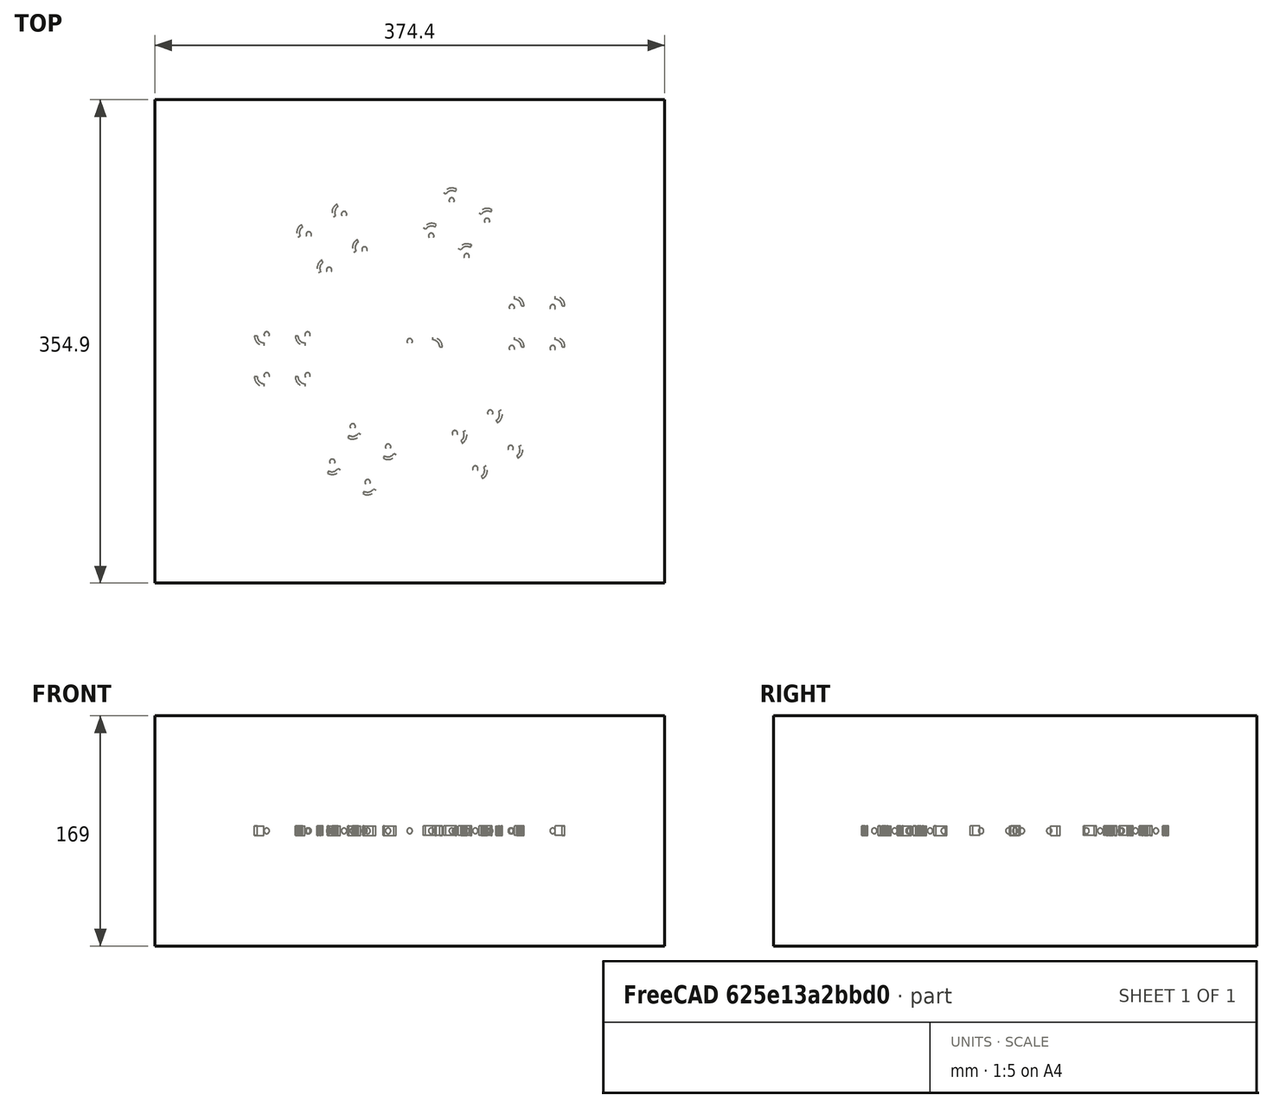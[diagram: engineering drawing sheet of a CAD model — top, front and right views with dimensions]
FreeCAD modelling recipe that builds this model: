
FCSTD DOCUMENT  (FreeCAD 1.0R39109 (Git))
Label: polarArrray-of-orthoArray-of-Assembly
License: All rights reserved
LicenseURL: http://en.wikipedia.org/wiki/All_rights_reserved
objects: App::DocumentObjectGroupPython×1251, App::Part×6, Part::FeaturePython×5
note: 5 computed .brp shape members not serialized (recipe doc carries the construction recipe); baked Part::Feature solids carry a one-line shape summary decoded from their .brp

FEATURE [App::DocumentObjectGroupPython] HALFPI  # scripted group (container) (typed FeaturePython)
  name = HALFPI
  value = pi/2.
FEATURE [App::DocumentObjectGroupPython] PI  # scripted group (container) (typed FeaturePython)
  name = PI
  value = 1.*pi
FEATURE [App::DocumentObjectGroupPython] TWOPI  # scripted group (container) (typed FeaturePython)
  name = TWOPI
  value = 2.*pi
FEATURE [App::DocumentObjectGroupPython] Constants  # scripted group (container) (typed FeaturePython)
  Group = -> [HALFPI,PI,TWOPI]
FEATURE [App::DocumentObjectGroupPython] Variables  # scripted group (container) (typed FeaturePython)
FEATURE [App::DocumentObjectGroupPython] Quantities  # scripted group (container) (typed FeaturePython)
FEATURE [App::DocumentObjectGroupPython] Isotopes  # scripted group (container) (typed FeaturePython)
FEATURE [App::DocumentObjectGroupPython] Elements  # scripted group (container) (typed FeaturePython)
FEATURE [App::DocumentObjectGroupPython] Matrix  # scripted group (container) (typed FeaturePython)
FEATURE [App::DocumentObjectGroupPython] Surfaces  # scripted group (container) (typed FeaturePython)
FEATURE [App::DocumentObjectGroupPython] Opticals  # scripted group (container) (typed FeaturePython)
  Group = -> [Matrix,Surfaces]
FEATURE [App::DocumentObjectGroupPython] G4Isotopes  # scripted group (container) (typed FeaturePython)
FEATURE [App::DocumentObjectGroupPython] H_element  # scripted group (container) (typed FeaturePython)
  Z = 1
  atom_value = 1.008
  formula = H
  name = H_element
FEATURE [App::DocumentObjectGroupPython] He_element  # scripted group (container) (typed FeaturePython)
  Z = 2
  atom_value = 4.0026
  formula = He
  name = He_element
FEATURE [App::DocumentObjectGroupPython] Li_element  # scripted group (container) (typed FeaturePython)
  Z = 3
  atom_value = 6.94
  formula = Li
  name = Li_element
FEATURE [App::DocumentObjectGroupPython] Be_element  # scripted group (container) (typed FeaturePython)
  Z = 4
  atom_value = 9.01218
  formula = Be
  name = Be_element
FEATURE [App::DocumentObjectGroupPython] B_element  # scripted group (container) (typed FeaturePython)
  Z = 5
  atom_value = 10.81
  formula = B
  name = B_element
FEATURE [App::DocumentObjectGroupPython] C_element  # scripted group (container) (typed FeaturePython)
  Z = 6
  atom_value = 12.011
  formula = C
  name = C_element
FEATURE [App::DocumentObjectGroupPython] N_element  # scripted group (container) (typed FeaturePython)
  Z = 7
  atom_value = 14.007
  formula = N
  name = N_element
FEATURE [App::DocumentObjectGroupPython] O_element  # scripted group (container) (typed FeaturePython)
  Z = 8
  atom_value = 15.999
  formula = O
  name = O_element
FEATURE [App::DocumentObjectGroupPython] F_element  # scripted group (container) (typed FeaturePython)
  Z = 9
  atom_value = 18.9984
  formula = F
  name = F_element
FEATURE [App::DocumentObjectGroupPython] Ne_element  # scripted group (container) (typed FeaturePython)
  Z = 10
  atom_value = 20.1797
  formula = Ne
  name = Ne_element
FEATURE [App::DocumentObjectGroupPython] Na_element  # scripted group (container) (typed FeaturePython)
  Z = 11
  atom_value = 22.9898
  formula = Na
  name = Na_element
FEATURE [App::DocumentObjectGroupPython] Mg_element  # scripted group (container) (typed FeaturePython)
  Z = 12
  atom_value = 24.305
  formula = Mg
  name = Mg_element
FEATURE [App::DocumentObjectGroupPython] Al_element  # scripted group (container) (typed FeaturePython)
  Z = 13
  atom_value = 26.9815
  formula = Al
  name = Al_element
FEATURE [App::DocumentObjectGroupPython] Si_element  # scripted group (container) (typed FeaturePython)
  Z = 14
  atom_value = 28.085
  formula = Si
  name = Si_element
FEATURE [App::DocumentObjectGroupPython] P_element  # scripted group (container) (typed FeaturePython)
  Z = 15
  atom_value = 30.9738
  formula = P
  name = P_element
FEATURE [App::DocumentObjectGroupPython] S_element  # scripted group (container) (typed FeaturePython)
  Z = 16
  atom_value = 32.06
  formula = S
  name = S_element
FEATURE [App::DocumentObjectGroupPython] Cl_element  # scripted group (container) (typed FeaturePython)
  Z = 17
  atom_value = 35.45
  formula = Cl
  name = Cl_element
FEATURE [App::DocumentObjectGroupPython] Ar_element  # scripted group (container) (typed FeaturePython)
  Z = 18
  atom_value = 39.95
  formula = Ar
  name = Ar_element
FEATURE [App::DocumentObjectGroupPython] K_element  # scripted group (container) (typed FeaturePython)
  Z = 19
  atom_value = 39.0983
  formula = K
  name = K_element
FEATURE [App::DocumentObjectGroupPython] Ca_element  # scripted group (container) (typed FeaturePython)
  Z = 20
  atom_value = 40.078
  formula = Ca
  name = Ca_element
FEATURE [App::DocumentObjectGroupPython] Sc_element  # scripted group (container) (typed FeaturePython)
  Z = 21
  atom_value = 44.9559
  formula = Sc
  name = Sc_element
FEATURE [App::DocumentObjectGroupPython] Ti_element  # scripted group (container) (typed FeaturePython)
  Z = 22
  atom_value = 47.867
  formula = Ti
  name = Ti_element
FEATURE [App::DocumentObjectGroupPython] V_element  # scripted group (container) (typed FeaturePython)
  Z = 23
  atom_value = 50.9415
  formula = V
  name = V_element
FEATURE [App::DocumentObjectGroupPython] Cr_element  # scripted group (container) (typed FeaturePython)
  Z = 24
  atom_value = 51.9961
  formula = Cr
  name = Cr_element
FEATURE [App::DocumentObjectGroupPython] Mn_element  # scripted group (container) (typed FeaturePython)
  Z = 25
  atom_value = 54.938
  formula = Mn
  name = Mn_element
FEATURE [App::DocumentObjectGroupPython] Fe_element  # scripted group (container) (typed FeaturePython)
  Z = 26
  atom_value = 55.845
  formula = Fe
  name = Fe_element
FEATURE [App::DocumentObjectGroupPython] Co_element  # scripted group (container) (typed FeaturePython)
  Z = 27
  atom_value = 58.9332
  formula = Co
  name = Co_element
FEATURE [App::DocumentObjectGroupPython] Ni_element  # scripted group (container) (typed FeaturePython)
  Z = 28
  atom_value = 58.6934
  formula = Ni
  name = Ni_element
FEATURE [App::DocumentObjectGroupPython] Cu_element  # scripted group (container) (typed FeaturePython)
  Z = 29
  atom_value = 63.546
  formula = Cu
  name = Cu_element
FEATURE [App::DocumentObjectGroupPython] Zn_element  # scripted group (container) (typed FeaturePython)
  Z = 30
  atom_value = 65.38
  formula = Zn
  name = Zn_element
FEATURE [App::DocumentObjectGroupPython] Ga_element  # scripted group (container) (typed FeaturePython)
  Z = 31
  atom_value = 69.723
  formula = Ga
  name = Ga_element
FEATURE [App::DocumentObjectGroupPython] Ge_element  # scripted group (container) (typed FeaturePython)
  Z = 32
  atom_value = 72.63
  formula = Ge
  name = Ge_element
FEATURE [App::DocumentObjectGroupPython] As_element  # scripted group (container) (typed FeaturePython)
  Z = 33
  atom_value = 74.9216
  formula = As
  name = As_element
FEATURE [App::DocumentObjectGroupPython] Se_element  # scripted group (container) (typed FeaturePython)
  Z = 34
  atom_value = 78.971
  formula = Se
  name = Se_element
FEATURE [App::DocumentObjectGroupPython] Br_element  # scripted group (container) (typed FeaturePython)
  Z = 35
  atom_value = 79.904
  formula = Br
  name = Br_element
FEATURE [App::DocumentObjectGroupPython] Kr_element  # scripted group (container) (typed FeaturePython)
  Z = 36
  atom_value = 83.798
  formula = Kr
  name = Kr_element
FEATURE [App::DocumentObjectGroupPython] Rb_element  # scripted group (container) (typed FeaturePython)
  Z = 37
  atom_value = 85.4678
  formula = Rb
  name = Rb_element
FEATURE [App::DocumentObjectGroupPython] Sr_element  # scripted group (container) (typed FeaturePython)
  Z = 38
  atom_value = 87.62
  formula = Sr
  name = Sr_element
FEATURE [App::DocumentObjectGroupPython] Y_element  # scripted group (container) (typed FeaturePython)
  Z = 39
  atom_value = 88.9058
  formula = Y
  name = Y_element
FEATURE [App::DocumentObjectGroupPython] Zr_element  # scripted group (container) (typed FeaturePython)
  Z = 40
  atom_value = 91.224
  formula = Zr
  name = Zr_element
FEATURE [App::DocumentObjectGroupPython] Nb_element  # scripted group (container) (typed FeaturePython)
  Z = 41
  atom_value = 92.9064
  formula = Nb
  name = Nb_element
FEATURE [App::DocumentObjectGroupPython] Mo_element  # scripted group (container) (typed FeaturePython)
  Z = 42
  atom_value = 95.95
  formula = Mo
  name = Mo_element
FEATURE [App::DocumentObjectGroupPython] Tc_element  # scripted group (container) (typed FeaturePython)
  Z = 43
  atom_value = 97
  formula = Tc
  name = Tc_element
FEATURE [App::DocumentObjectGroupPython] Ru_element  # scripted group (container) (typed FeaturePython)
  Z = 44
  atom_value = 101.07
  formula = Ru
  name = Ru_element
FEATURE [App::DocumentObjectGroupPython] Rh_element  # scripted group (container) (typed FeaturePython)
  Z = 45
  atom_value = 102.905
  formula = Rh
  name = Rh_element
FEATURE [App::DocumentObjectGroupPython] Pd_element  # scripted group (container) (typed FeaturePython)
  Z = 46
  atom_value = 106.42
  formula = Pd
  name = Pd_element
FEATURE [App::DocumentObjectGroupPython] Ag_element  # scripted group (container) (typed FeaturePython)
  Z = 47
  atom_value = 107.868
  formula = Ag
  name = Ag_element
FEATURE [App::DocumentObjectGroupPython] Cd_element  # scripted group (container) (typed FeaturePython)
  Z = 48
  atom_value = 112.414
  formula = Cd
  name = Cd_element
FEATURE [App::DocumentObjectGroupPython] In_element  # scripted group (container) (typed FeaturePython)
  Z = 49
  atom_value = 114.818
  formula = In
  name = In_element
FEATURE [App::DocumentObjectGroupPython] Sn_element  # scripted group (container) (typed FeaturePython)
  Z = 50
  atom_value = 118.71
  formula = Sn
  name = Sn_element
FEATURE [App::DocumentObjectGroupPython] Sb_element  # scripted group (container) (typed FeaturePython)
  Z = 51
  atom_value = 121.76
  formula = Sb
  name = Sb_element
FEATURE [App::DocumentObjectGroupPython] Te_element  # scripted group (container) (typed FeaturePython)
  Z = 52
  atom_value = 127.6
  formula = Te
  name = Te_element
FEATURE [App::DocumentObjectGroupPython] I_element  # scripted group (container) (typed FeaturePython)
  Z = 53
  atom_value = 126.904
  formula = I
  name = I_element
FEATURE [App::DocumentObjectGroupPython] Xe_element  # scripted group (container) (typed FeaturePython)
  Z = 54
  atom_value = 131.293
  formula = Xe
  name = Xe_element
FEATURE [App::DocumentObjectGroupPython] Cs_element  # scripted group (container) (typed FeaturePython)
  Z = 55
  atom_value = 132.905
  formula = Cs
  name = Cs_element
FEATURE [App::DocumentObjectGroupPython] Ba_element  # scripted group (container) (typed FeaturePython)
  Z = 56
  atom_value = 137.327
  formula = Ba
  name = Ba_element
FEATURE [App::DocumentObjectGroupPython] La_element  # scripted group (container) (typed FeaturePython)
  Z = 57
  atom_value = 138.905
  formula = La
  name = La_element
FEATURE [App::DocumentObjectGroupPython] Ce_element  # scripted group (container) (typed FeaturePython)
  Z = 58
  atom_value = 140.116
  formula = Ce
  name = Ce_element
FEATURE [App::DocumentObjectGroupPython] Pr_element  # scripted group (container) (typed FeaturePython)
  Z = 59
  atom_value = 140.908
  formula = Pr
  name = Pr_element
FEATURE [App::DocumentObjectGroupPython] Nd_element  # scripted group (container) (typed FeaturePython)
  Z = 60
  atom_value = 144.242
  formula = Nd
  name = Nd_element
FEATURE [App::DocumentObjectGroupPython] Pm_element  # scripted group (container) (typed FeaturePython)
  Z = 61
  atom_value = 145
  formula = Pm
  name = Pm_element
FEATURE [App::DocumentObjectGroupPython] Sm_element  # scripted group (container) (typed FeaturePython)
  Z = 62
  atom_value = 150.36
  formula = Sm
  name = Sm_element
FEATURE [App::DocumentObjectGroupPython] Eu_element  # scripted group (container) (typed FeaturePython)
  Z = 63
  atom_value = 151.964
  formula = Eu
  name = Eu_element
FEATURE [App::DocumentObjectGroupPython] Gd_element  # scripted group (container) (typed FeaturePython)
  Z = 64
  atom_value = 157.25
  formula = Gd
  name = Gd_element
FEATURE [App::DocumentObjectGroupPython] Tb_element  # scripted group (container) (typed FeaturePython)
  Z = 65
  atom_value = 158.925
  formula = Tb
  name = Tb_element
FEATURE [App::DocumentObjectGroupPython] Dy_element  # scripted group (container) (typed FeaturePython)
  Z = 66
  atom_value = 162.5
  formula = Dy
  name = Dy_element
FEATURE [App::DocumentObjectGroupPython] Ho_element  # scripted group (container) (typed FeaturePython)
  Z = 67
  atom_value = 164.93
  formula = Ho
  name = Ho_element
FEATURE [App::DocumentObjectGroupPython] Er_element  # scripted group (container) (typed FeaturePython)
  Z = 68
  atom_value = 167.259
  formula = Er
  name = Er_element
FEATURE [App::DocumentObjectGroupPython] Tm_element  # scripted group (container) (typed FeaturePython)
  Z = 69
  atom_value = 168.934
  formula = Tm
  name = Tm_element
FEATURE [App::DocumentObjectGroupPython] Yb_element  # scripted group (container) (typed FeaturePython)
  Z = 70
  atom_value = 173.045
  formula = Yb
  name = Yb_element
FEATURE [App::DocumentObjectGroupPython] Lu_element  # scripted group (container) (typed FeaturePython)
  Z = 71
  atom_value = 174.967
  formula = Lu
  name = Lu_element
FEATURE [App::DocumentObjectGroupPython] Hf_element  # scripted group (container) (typed FeaturePython)
  Z = 72
  atom_value = 178.49
  formula = Hf
  name = Hf_element
FEATURE [App::DocumentObjectGroupPython] Ta_element  # scripted group (container) (typed FeaturePython)
  Z = 73
  atom_value = 180.948
  formula = Ta
  name = Ta_element
FEATURE [App::DocumentObjectGroupPython] W_element  # scripted group (container) (typed FeaturePython)
  Z = 74
  atom_value = 183.84
  formula = W
  name = W_element
FEATURE [App::DocumentObjectGroupPython] Re_element  # scripted group (container) (typed FeaturePython)
  Z = 75
  atom_value = 186.207
  formula = Re
  name = Re_element
FEATURE [App::DocumentObjectGroupPython] Os_element  # scripted group (container) (typed FeaturePython)
  Z = 76
  atom_value = 190.23
  formula = Os
  name = Os_element
FEATURE [App::DocumentObjectGroupPython] Ir_element  # scripted group (container) (typed FeaturePython)
  Z = 77
  atom_value = 192.217
  formula = Ir
  name = Ir_element
FEATURE [App::DocumentObjectGroupPython] Pt_element  # scripted group (container) (typed FeaturePython)
  Z = 78
  atom_value = 195.084
  formula = Pt
  name = Pt_element
FEATURE [App::DocumentObjectGroupPython] Au_element  # scripted group (container) (typed FeaturePython)
  Z = 79
  atom_value = 196.967
  formula = Au
  name = Au_element
FEATURE [App::DocumentObjectGroupPython] Hg_element  # scripted group (container) (typed FeaturePython)
  Z = 80
  atom_value = 200.592
  formula = Hg
  name = Hg_element
FEATURE [App::DocumentObjectGroupPython] Tl_element  # scripted group (container) (typed FeaturePython)
  Z = 81
  atom_value = 204.38
  formula = Tl
  name = Tl_element
FEATURE [App::DocumentObjectGroupPython] Pb_element  # scripted group (container) (typed FeaturePython)
  Z = 82
  atom_value = 207.2
  formula = Pb
  name = Pb_element
FEATURE [App::DocumentObjectGroupPython] Bi_element  # scripted group (container) (typed FeaturePython)
  Z = 83
  atom_value = 208.98
  formula = Bi
  name = Bi_element
FEATURE [App::DocumentObjectGroupPython] Po_element  # scripted group (container) (typed FeaturePython)
  Z = 84
  atom_value = 209
  formula = Po
  name = Po_element
FEATURE [App::DocumentObjectGroupPython] At_element  # scripted group (container) (typed FeaturePython)
  Z = 85
  atom_value = 210
  formula = At
  name = At_element
FEATURE [App::DocumentObjectGroupPython] Rn_element  # scripted group (container) (typed FeaturePython)
  Z = 86
  atom_value = 222
  formula = Rn
  name = Rn_element
FEATURE [App::DocumentObjectGroupPython] Fr_element  # scripted group (container) (typed FeaturePython)
  Z = 87
  atom_value = 223
  formula = Fr
  name = Fr_element
FEATURE [App::DocumentObjectGroupPython] Ra_element  # scripted group (container) (typed FeaturePython)
  Z = 88
  atom_value = 226
  formula = Ra
  name = Ra_element
FEATURE [App::DocumentObjectGroupPython] Ac_element  # scripted group (container) (typed FeaturePython)
  Z = 89
  atom_value = 227
  formula = Ac
  name = Ac_element
FEATURE [App::DocumentObjectGroupPython] Th_element  # scripted group (container) (typed FeaturePython)
  Z = 90
  atom_value = 232.038
  formula = Th
  name = Th_element
FEATURE [App::DocumentObjectGroupPython] Pa_element  # scripted group (container) (typed FeaturePython)
  Z = 91
  atom_value = 231.036
  formula = Pa
  name = Pa_element
FEATURE [App::DocumentObjectGroupPython] U_element  # scripted group (container) (typed FeaturePython)
  Z = 92
  atom_value = 238.029
  formula = U
  name = U_element
FEATURE [App::DocumentObjectGroupPython] Np_element  # scripted group (container) (typed FeaturePython)
  Z = 93
  atom_value = 237
  formula = Np
  name = Np_element
FEATURE [App::DocumentObjectGroupPython] Pu_element  # scripted group (container) (typed FeaturePython)
  Z = 94
  atom_value = 244
  formula = Pu
  name = Pu_element
FEATURE [App::DocumentObjectGroupPython] Am_element  # scripted group (container) (typed FeaturePython)
  Z = 95
  atom_value = 243
  formula = Am
  name = Am_element
FEATURE [App::DocumentObjectGroupPython] Cm_element  # scripted group (container) (typed FeaturePython)
  Z = 96
  atom_value = 247
  formula = Cm
  name = Cm_element
FEATURE [App::DocumentObjectGroupPython] Bk_element  # scripted group (container) (typed FeaturePython)
  Z = 97
  atom_value = 247
  formula = Bk
  name = Bk_element
FEATURE [App::DocumentObjectGroupPython] Cf_element  # scripted group (container) (typed FeaturePython)
  Z = 98
  atom_value = 251
  formula = Cf
  name = Cf_element
FEATURE [App::DocumentObjectGroupPython] G4Elements  # scripted group (container) (typed FeaturePython)
  Group = -> [H_element,He_element,Li_element,Be_element,B_element,C_element,N_element,O_element,F_element,Ne_element,Na_element,Mg_element,Al_element,Si_element,P_element,S_element,Cl_element,Ar_element,K_element,Ca_element,Sc_element,Ti_element,V_element,Cr_element,Mn_element,Fe_element,Co_element,Ni_element,Cu_element,Zn_element,Ga_element,Ge_element,As_element,Se_element,Br_element,Kr_element,Rb_element,+61 more]
FEATURE [App::DocumentObjectGroupPython] H_element001  label="H_element : 0.101"  # scripted group (container) (typed FeaturePython)
  n = 0.101327
FEATURE [App::DocumentObjectGroupPython] C_element001  label="C_element : 0.775"  # scripted group (container) (typed FeaturePython)
  n = 0.7755
FEATURE [App::DocumentObjectGroupPython] N_element001  label="N_element : 0.035"  # scripted group (container) (typed FeaturePython)
  n = 0.035057
FEATURE [App::DocumentObjectGroupPython] O_element001  label="O_element : 0.052"  # scripted group (container) (typed FeaturePython)
  n = 0.0523159
FEATURE [App::DocumentObjectGroupPython] F_element001  label="F_element : 0.017"  # scripted group (container) (typed FeaturePython)
  n = 0.017422
FEATURE [App::DocumentObjectGroupPython] Ca_element001  label="Ca_element : 0.018"  # scripted group (container) (typed FeaturePython)
  n = 0.018378
FEATURE [App::DocumentObjectGroupPython] G4_A_150_TISSUE  label="G4_A-150_TISSUE"  # scripted group (container) (typed FeaturePython)
  Dunit = g/cm3
  Dvalue = 1.127
  Group = -> [H_element001,C_element001,N_element001,O_element001,F_element001,Ca_element001]
  conduct = 2
  density = 1
  expand = 3
  formula = G4_A-150_TISSUE
  name = G4_A-150_TISSUE
  specific = 4
FEATURE [App::DocumentObjectGroupPython] C_element002  label="C_element : 3"  # scripted group (container) (typed FeaturePython)
  n = 3
  ref = C_element
FEATURE [App::DocumentObjectGroupPython] H_element002  label="H_element : 6"  # scripted group (container) (typed FeaturePython)
  n = 6
  ref = H_element
FEATURE [App::DocumentObjectGroupPython] O_element002  label="O_element : 1"  # scripted group (container) (typed FeaturePython)
  n = 1
  ref = O_element
FEATURE [App::DocumentObjectGroupPython] G4_ACETONE  # scripted group (container) (typed FeaturePython)
  Dunit = g/cm3
  Dvalue = 0.7899
  Group = -> [C_element002,H_element002,O_element002]
  conduct = 2
  density = 1
  expand = 3
  formula = G4_ACETONE
  name = G4_ACETONE
  specific = 4
FEATURE [App::DocumentObjectGroupPython] C_element003  label="C_element : 2"  # scripted group (container) (typed FeaturePython)
  n = 2
  ref = C_element
FEATURE [App::DocumentObjectGroupPython] H_element003  label="H_element : 2"  # scripted group (container) (typed FeaturePython)
  n = 2
  ref = H_element
FEATURE [App::DocumentObjectGroupPython] G4_ACETYLENE  # scripted group (container) (typed FeaturePython)
  Dunit = g/cm3
  Dvalue = 0.0010967
  Group = -> [C_element003,H_element003]
  conduct = 2
  density = 1
  expand = 3
  formula = G4_ACETYLENE
  name = G4_ACETYLENE
  specific = 4
FEATURE [App::DocumentObjectGroupPython] C_element004  label="C_element : 5"  # scripted group (container) (typed FeaturePython)
  n = 5
  ref = C_element
FEATURE [App::DocumentObjectGroupPython] H_element004  label="H_element : 5"  # scripted group (container) (typed FeaturePython)
  n = 5
  ref = H_element
FEATURE [App::DocumentObjectGroupPython] N_element002  label="N_element : 5"  # scripted group (container) (typed FeaturePython)
  n = 5
  ref = N_element
FEATURE [App::DocumentObjectGroupPython] G4_ADENINE  # scripted group (container) (typed FeaturePython)
  Dunit = g/cm3
  Dvalue = 1.6
  Group = -> [C_element004,H_element004,N_element002]
  conduct = 2
  density = 1
  expand = 3
  formula = G4_ADENINE
  name = G4_ADENINE
  specific = 4
FEATURE [App::DocumentObjectGroupPython] H_element005  label="H_element : 0.114"  # scripted group (container) (typed FeaturePython)
  n = 0.114
FEATURE [App::DocumentObjectGroupPython] C_element005  label="C_element : 0.598"  # scripted group (container) (typed FeaturePython)
  n = 0.598
FEATURE [App::DocumentObjectGroupPython] N_element003  label="N_element : 0.007"  # scripted group (container) (typed FeaturePython)
  n = 0.007
FEATURE [App::DocumentObjectGroupPython] O_element003  label="O_element : 0.278"  # scripted group (container) (typed FeaturePython)
  n = 0.278
FEATURE [App::DocumentObjectGroupPython] Na_element001  label="Na_element : 0.001"  # scripted group (container) (typed FeaturePython)
  n = 0.001
FEATURE [App::DocumentObjectGroupPython] S_element001  label="S_element : 0.001"  # scripted group (container) (typed FeaturePython)
  n = 0.001
FEATURE [App::DocumentObjectGroupPython] Cl_element001  label="Cl_element : 0.001"  # scripted group (container) (typed FeaturePython)
  n = 0.001
FEATURE [App::DocumentObjectGroupPython] G4_ADIPOSE_TISSUE_ICRP  # scripted group (container) (typed FeaturePython)
  Dunit = g/cm3
  Dvalue = 0.95
  Group = -> [H_element005,C_element005,N_element003,O_element003,Na_element001,S_element001,Cl_element001]
  conduct = 2
  density = 1
  expand = 3
  formula = G4_ADIPOSE_TISSUE_ICRP
  name = G4_ADIPOSE_TISSUE_ICRP
  specific = 4
FEATURE [App::DocumentObjectGroupPython] C_element006  label="C_element : 0.000"  # scripted group (container) (typed FeaturePython)
  n = 0.000124
FEATURE [App::DocumentObjectGroupPython] N_element004  label="N_element : 0.755"  # scripted group (container) (typed FeaturePython)
  n = 0.755268
FEATURE [App::DocumentObjectGroupPython] O_element004  label="O_element : 0.232"  # scripted group (container) (typed FeaturePython)
  n = 0.231781
FEATURE [App::DocumentObjectGroupPython] Ar_element001  label="Ar_element : 0.013"  # scripted group (container) (typed FeaturePython)
  n = 0.012827
FEATURE [App::DocumentObjectGroupPython] G4_AIR  # scripted group (container) (typed FeaturePython)
  Dunit = g/cm3
  Dvalue = 0.00120479
  Group = -> [C_element006,N_element004,O_element004,Ar_element001]
  conduct = 2
  density = 1
  expand = 3
  formula = G4_AIR
  name = G4_AIR
  specific = 4
FEATURE [App::DocumentObjectGroupPython] C_element007  label="C_element : 006"  # scripted group (container) (typed FeaturePython)
  n = 3
  ref = C_element
FEATURE [App::DocumentObjectGroupPython] H_element006  label="H_element : 7"  # scripted group (container) (typed FeaturePython)
  n = 7
  ref = H_element
FEATURE [App::DocumentObjectGroupPython] N_element005  label="N_element : 1"  # scripted group (container) (typed FeaturePython)
  n = 1
  ref = N_element
FEATURE [App::DocumentObjectGroupPython] O_element005  label="O_element : 2"  # scripted group (container) (typed FeaturePython)
  n = 2
  ref = O_element
FEATURE [App::DocumentObjectGroupPython] G4_ALANINE  # scripted group (container) (typed FeaturePython)
  Dunit = g/cm3
  Dvalue = 1.42
  Group = -> [C_element007,H_element006,N_element005,O_element005]
  conduct = 2
  density = 1
  expand = 3
  formula = G4_ALANINE
  name = G4_ALANINE
  specific = 4
FEATURE [App::DocumentObjectGroupPython] Al_element001  label="Al_element : 2"  # scripted group (container) (typed FeaturePython)
  n = 2
  ref = Al_element
FEATURE [App::DocumentObjectGroupPython] O_element006  label="O_element : 3"  # scripted group (container) (typed FeaturePython)
  n = 3
  ref = O_element
FEATURE [App::DocumentObjectGroupPython] G4_ALUMINUM_OXIDE  # scripted group (container) (typed FeaturePython)
  Dunit = g/cm3
  Dvalue = 3.97
  Group = -> [Al_element001,O_element006]
  conduct = 2
  density = 1
  expand = 3
  formula = G4_ALUMINUM_OXIDE
  name = G4_ALUMINUM_OXIDE
  specific = 4
FEATURE [App::DocumentObjectGroupPython] H_element007  label="H_element : 0.106"  # scripted group (container) (typed FeaturePython)
  n = 0.10593
FEATURE [App::DocumentObjectGroupPython] C_element008  label="C_element : 0.789"  # scripted group (container) (typed FeaturePython)
  n = 0.788974
FEATURE [App::DocumentObjectGroupPython] O_element007  label="O_element : 0.105"  # scripted group (container) (typed FeaturePython)
  n = 0.105096
FEATURE [App::DocumentObjectGroupPython] G4_AMBER  # scripted group (container) (typed FeaturePython)
  Dunit = g/cm3
  Dvalue = 1.1
  Group = -> [H_element007,C_element008,O_element007]
  conduct = 2
  density = 1
  expand = 3
  formula = G4_AMBER
  name = G4_AMBER
  specific = 4
FEATURE [App::DocumentObjectGroupPython] N_element006  label="N_element : 006"  # scripted group (container) (typed FeaturePython)
  n = 1
  ref = N_element
FEATURE [App::DocumentObjectGroupPython] H_element008  label="H_element : 3"  # scripted group (container) (typed FeaturePython)
  n = 3
  ref = H_element
FEATURE [App::DocumentObjectGroupPython] G4_AMMONIA  # scripted group (container) (typed FeaturePython)
  Dunit = g/cm3
  Dvalue = 0.000826019
  Group = -> [N_element006,H_element008]
  conduct = 2
  density = 1
  expand = 3
  formula = G4_AMMONIA
  name = G4_AMMONIA
  specific = 4
FEATURE [App::DocumentObjectGroupPython] C_element009  label="C_element : 6"  # scripted group (container) (typed FeaturePython)
  n = 6
  ref = C_element
FEATURE [App::DocumentObjectGroupPython] H_element009  label="H_element : 008"  # scripted group (container) (typed FeaturePython)
  n = 7
  ref = H_element
FEATURE [App::DocumentObjectGroupPython] N_element007  label="N_element : 007"  # scripted group (container) (typed FeaturePython)
  n = 1
  ref = N_element
FEATURE [App::DocumentObjectGroupPython] G4_ANILINE  # scripted group (container) (typed FeaturePython)
  Dunit = g/cm3
  Dvalue = 1.0235
  Group = -> [C_element009,H_element009,N_element007]
  conduct = 2
  density = 1
  expand = 3
  formula = G4_ANILINE
  name = G4_ANILINE
  specific = 4
FEATURE [App::DocumentObjectGroupPython] C_element010  label="C_element : 14"  # scripted group (container) (typed FeaturePython)
  n = 14
  ref = C_element
FEATURE [App::DocumentObjectGroupPython] H_element010  label="H_element : 10"  # scripted group (container) (typed FeaturePython)
  n = 10
  ref = H_element
FEATURE [App::DocumentObjectGroupPython] G4_ANTHRACENE  # scripted group (container) (typed FeaturePython)
  Dunit = g/cm3
  Dvalue = 1.283
  Group = -> [C_element010,H_element010]
  conduct = 2
  density = 1
  expand = 3
  formula = G4_ANTHRACENE
  name = G4_ANTHRACENE
  specific = 4
FEATURE [App::DocumentObjectGroupPython] H_element011  label="H_element : 0.065"  # scripted group (container) (typed FeaturePython)
  n = 0.0654709
FEATURE [App::DocumentObjectGroupPython] C_element011  label="C_element : 0.537"  # scripted group (container) (typed FeaturePython)
  n = 0.536944
FEATURE [App::DocumentObjectGroupPython] N_element008  label="N_element : 0.021"  # scripted group (container) (typed FeaturePython)
  n = 0.0215
FEATURE [App::DocumentObjectGroupPython] O_element008  label="O_element : 0.032"  # scripted group (container) (typed FeaturePython)
  n = 0.032085
FEATURE [App::DocumentObjectGroupPython] F_element002  label="F_element : 0.167"  # scripted group (container) (typed FeaturePython)
  n = 0.167411
FEATURE [App::DocumentObjectGroupPython] Ca_element002  label="Ca_element : 0.177"  # scripted group (container) (typed FeaturePython)
  n = 0.176589
FEATURE [App::DocumentObjectGroupPython] G4_B_100_BONE  label="G4_B-100_BONE"  # scripted group (container) (typed FeaturePython)
  Dunit = g/cm3
  Dvalue = 1.45
  Group = -> [H_element011,C_element011,N_element008,O_element008,F_element002,Ca_element002]
  conduct = 2
  density = 1
  expand = 3
  formula = G4_B-100_BONE
  name = G4_B-100_BONE
  specific = 4
FEATURE [App::DocumentObjectGroupPython] H_element012  label="H_element : 0.057"  # scripted group (container) (typed FeaturePython)
  n = 0.057441
FEATURE [App::DocumentObjectGroupPython] C_element012  label="C_element : 0.790"  # scripted group (container) (typed FeaturePython)
  n = 0.774591
FEATURE [App::DocumentObjectGroupPython] O_element009  label="O_element : 0.168"  # scripted group (container) (typed FeaturePython)
  n = 0.167968
FEATURE [App::DocumentObjectGroupPython] G4_BAKELITE  # scripted group (container) (typed FeaturePython)
  Dunit = g/cm3
  Dvalue = 1.25
  Group = -> [H_element012,C_element012,O_element009]
  conduct = 2
  density = 1
  expand = 3
  formula = G4_BAKELITE
  name = G4_BAKELITE
  specific = 4
FEATURE [App::DocumentObjectGroupPython] Ba_element001  label="Ba_element : 1"  # scripted group (container) (typed FeaturePython)
  n = 1
  ref = Ba_element
FEATURE [App::DocumentObjectGroupPython] F_element003  label="F_element : 2"  # scripted group (container) (typed FeaturePython)
  n = 2
  ref = F_element
FEATURE [App::DocumentObjectGroupPython] G4_BARIUM_FLUORIDE  # scripted group (container) (typed FeaturePython)
  Dunit = g/cm3
  Dvalue = 4.89
  Group = -> [Ba_element001,F_element003]
  conduct = 2
  density = 1
  expand = 3
  formula = G4_BARIUM_FLUORIDE
  name = G4_BARIUM_FLUORIDE
  specific = 4
FEATURE [App::DocumentObjectGroupPython] Ba_element002  label="Ba_element : 002"  # scripted group (container) (typed FeaturePython)
  n = 1
  ref = Ba_element
FEATURE [App::DocumentObjectGroupPython] S_element002  label="S_element : 1"  # scripted group (container) (typed FeaturePython)
  n = 1
  ref = S_element
FEATURE [App::DocumentObjectGroupPython] O_element010  label="O_element : 4"  # scripted group (container) (typed FeaturePython)
  n = 4
  ref = O_element
FEATURE [App::DocumentObjectGroupPython] G4_BARIUM_SULFATE  # scripted group (container) (typed FeaturePython)
  Dunit = g/cm3
  Dvalue = 4.5
  Group = -> [Ba_element002,S_element002,O_element010]
  conduct = 2
  density = 1
  expand = 3
  formula = G4_BARIUM_SULFATE
  name = G4_BARIUM_SULFATE
  specific = 4
FEATURE [App::DocumentObjectGroupPython] C_element013  label="C_element : 007"  # scripted group (container) (typed FeaturePython)
  n = 6
  ref = C_element
FEATURE [App::DocumentObjectGroupPython] H_element013  label="H_element : 009"  # scripted group (container) (typed FeaturePython)
  n = 6
  ref = H_element
FEATURE [App::DocumentObjectGroupPython] G4_BENZENE  # scripted group (container) (typed FeaturePython)
  Dunit = g/cm3
  Dvalue = 0.87865
  Group = -> [C_element013,H_element013]
  conduct = 2
  density = 1
  expand = 3
  formula = G4_BENZENE
  name = G4_BENZENE
  specific = 4
FEATURE [App::DocumentObjectGroupPython] Be_element001  label="Be_element : 1"  # scripted group (container) (typed FeaturePython)
  n = 1
  ref = Be_element
FEATURE [App::DocumentObjectGroupPython] O_element011  label="O_element : 005"  # scripted group (container) (typed FeaturePython)
  n = 1
  ref = O_element
FEATURE [App::DocumentObjectGroupPython] G4_BERYLLIUM_OXIDE  # scripted group (container) (typed FeaturePython)
  Dunit = g/cm3
  Dvalue = 3.01
  Group = -> [Be_element001,O_element011]
  conduct = 2
  density = 1
  expand = 3
  formula = G4_BERYLLIUM_OXIDE
  name = G4_BERYLLIUM_OXIDE
  specific = 4
FEATURE [App::DocumentObjectGroupPython] Bi_element001  label="Bi_element : 4"  # scripted group (container) (typed FeaturePython)
  n = 4
  ref = Bi_element
FEATURE [App::DocumentObjectGroupPython] Ge_element001  label="Ge_element : 3"  # scripted group (container) (typed FeaturePython)
  n = 3
  ref = Ge_element
FEATURE [App::DocumentObjectGroupPython] O_element012  label="O_element : 12"  # scripted group (container) (typed FeaturePython)
  n = 12
  ref = O_element
FEATURE [App::DocumentObjectGroupPython] G4_BGO  # scripted group (container) (typed FeaturePython)
  Dunit = g/cm3
  Dvalue = 7.13
  Group = -> [Bi_element001,Ge_element001,O_element012]
  conduct = 2
  density = 1
  expand = 3
  formula = G4_BGO
  name = G4_BGO
  specific = 4
FEATURE [App::DocumentObjectGroupPython] H_element014  label="H_element : 0.102"  # scripted group (container) (typed FeaturePython)
  n = 0.102
FEATURE [App::DocumentObjectGroupPython] C_element014  label="C_element : 0.110"  # scripted group (container) (typed FeaturePython)
  n = 0.11
FEATURE [App::DocumentObjectGroupPython] N_element009  label="N_element : 0.033"  # scripted group (container) (typed FeaturePython)
  n = 0.033
FEATURE [App::DocumentObjectGroupPython] O_element013  label="O_element : 0.745"  # scripted group (container) (typed FeaturePython)
  n = 0.745
FEATURE [App::DocumentObjectGroupPython] Na_element002  label="Na_element : 0.002"  # scripted group (container) (typed FeaturePython)
  n = 0.001
FEATURE [App::DocumentObjectGroupPython] P_element001  label="P_element : 0.001"  # scripted group (container) (typed FeaturePython)
  n = 0.001
FEATURE [App::DocumentObjectGroupPython] S_element003  label="S_element : 0.002"  # scripted group (container) (typed FeaturePython)
  n = 0.002
FEATURE [App::DocumentObjectGroupPython] Cl_element002  label="Cl_element : 0.003"  # scripted group (container) (typed FeaturePython)
  n = 0.003
FEATURE [App::DocumentObjectGroupPython] K_element001  label="K_element : 0.002"  # scripted group (container) (typed FeaturePython)
  n = 0.002
FEATURE [App::DocumentObjectGroupPython] Fe_element001  label="Fe_element : 0.001"  # scripted group (container) (typed FeaturePython)
  n = 0.001
FEATURE [App::DocumentObjectGroupPython] G4_BLOOD_ICRP  # scripted group (container) (typed FeaturePython)
  Dunit = g/cm3
  Dvalue = 1.06
  Group = -> [H_element014,C_element014,N_element009,O_element013,Na_element002,P_element001,S_element003,Cl_element002,K_element001,Fe_element001]
  conduct = 2
  density = 1
  expand = 3
  formula = G4_BLOOD_ICRP
  name = G4_BLOOD_ICRP
  specific = 4
FEATURE [App::DocumentObjectGroupPython] H_element015  label="H_element : 0.064"  # scripted group (container) (typed FeaturePython)
  n = 0.064
FEATURE [App::DocumentObjectGroupPython] C_element015  label="C_element : 0.278"  # scripted group (container) (typed FeaturePython)
  n = 0.278
FEATURE [App::DocumentObjectGroupPython] N_element010  label="N_element : 0.027"  # scripted group (container) (typed FeaturePython)
  n = 0.027
FEATURE [App::DocumentObjectGroupPython] O_element014  label="O_element : 0.410"  # scripted group (container) (typed FeaturePython)
  n = 0.41
FEATURE [App::DocumentObjectGroupPython] Mg_element001  label="Mg_element : 0.002"  # scripted group (container) (typed FeaturePython)
  n = 0.002
FEATURE [App::DocumentObjectGroupPython] P_element002  label="P_element : 0.070"  # scripted group (container) (typed FeaturePython)
  n = 0.07
FEATURE [App::DocumentObjectGroupPython] S_element004  label="S_element : 0.003"  # scripted group (container) (typed FeaturePython)
  n = 0.002
FEATURE [App::DocumentObjectGroupPython] Ca_element003  label="Ca_element : 0.147"  # scripted group (container) (typed FeaturePython)
  n = 0.147
FEATURE [App::DocumentObjectGroupPython] G4_BONE_COMPACT_ICRU  # scripted group (container) (typed FeaturePython)
  Dunit = g/cm3
  Dvalue = 1.85
  Group = -> [H_element015,C_element015,N_element010,O_element014,Mg_element001,P_element002,S_element004,Ca_element003]
  conduct = 2
  density = 1
  expand = 3
  formula = G4_BONE_COMPACT_ICRU
  name = G4_BONE_COMPACT_ICRU
  specific = 4
FEATURE [App::DocumentObjectGroupPython] H_element016  label="H_element : 0.034"  # scripted group (container) (typed FeaturePython)
  n = 0.034
FEATURE [App::DocumentObjectGroupPython] C_element016  label="C_element : 0.155"  # scripted group (container) (typed FeaturePython)
  n = 0.155
FEATURE [App::DocumentObjectGroupPython] N_element011  label="N_element : 0.042"  # scripted group (container) (typed FeaturePython)
  n = 0.042
FEATURE [App::DocumentObjectGroupPython] O_element015  label="O_element : 0.435"  # scripted group (container) (typed FeaturePython)
  n = 0.435
FEATURE [App::DocumentObjectGroupPython] Na_element003  label="Na_element : 0.003"  # scripted group (container) (typed FeaturePython)
  n = 0.001
FEATURE [App::DocumentObjectGroupPython] Mg_element002  label="Mg_element : 0.003"  # scripted group (container) (typed FeaturePython)
  n = 0.002
FEATURE [App::DocumentObjectGroupPython] P_element003  label="P_element : 0.103"  # scripted group (container) (typed FeaturePython)
  n = 0.103
FEATURE [App::DocumentObjectGroupPython] S_element005  label="S_element : 0.004"  # scripted group (container) (typed FeaturePython)
  n = 0.003
FEATURE [App::DocumentObjectGroupPython] Ca_element004  label="Ca_element : 0.225"  # scripted group (container) (typed FeaturePython)
  n = 0.225
FEATURE [App::DocumentObjectGroupPython] G4_BONE_CORTICAL_ICRP  # scripted group (container) (typed FeaturePython)
  Dunit = g/cm3
  Dvalue = 1.92
  Group = -> [H_element016,C_element016,N_element011,O_element015,Na_element003,Mg_element002,P_element003,S_element005,Ca_element004]
  conduct = 2
  density = 1
  expand = 3
  formula = G4_BONE_CORTICAL_ICRP
  name = G4_BONE_CORTICAL_ICRP
  specific = 4
FEATURE [App::DocumentObjectGroupPython] B_element001  label="B_element : 4"  # scripted group (container) (typed FeaturePython)
  n = 4
  ref = B_element
FEATURE [App::DocumentObjectGroupPython] C_element017  label="C_element : 1"  # scripted group (container) (typed FeaturePython)
  n = 1
  ref = C_element
FEATURE [App::DocumentObjectGroupPython] G4_BORON_CARBIDE  # scripted group (container) (typed FeaturePython)
  Dunit = g/cm3
  Dvalue = 2.52
  Group = -> [B_element001,C_element017]
  conduct = 2
  density = 1
  expand = 3
  formula = G4_BORON_CARBIDE
  name = G4_BORON_CARBIDE
  specific = 4
FEATURE [App::DocumentObjectGroupPython] B_element002  label="B_element : 2"  # scripted group (container) (typed FeaturePython)
  n = 2
  ref = B_element
FEATURE [App::DocumentObjectGroupPython] O_element016  label="O_element : 006"  # scripted group (container) (typed FeaturePython)
  n = 3
  ref = O_element
FEATURE [App::DocumentObjectGroupPython] G4_BORON_OXIDE  # scripted group (container) (typed FeaturePython)
  Dunit = g/cm3
  Dvalue = 1.812
  Group = -> [B_element002,O_element016]
  conduct = 2
  density = 1
  expand = 3
  formula = G4_BORON_OXIDE
  name = G4_BORON_OXIDE
  specific = 4
FEATURE [App::DocumentObjectGroupPython] H_element017  label="H_element : 0.107"  # scripted group (container) (typed FeaturePython)
  n = 0.107
FEATURE [App::DocumentObjectGroupPython] C_element018  label="C_element : 0.145"  # scripted group (container) (typed FeaturePython)
  n = 0.145
FEATURE [App::DocumentObjectGroupPython] N_element012  label="N_element : 0.022"  # scripted group (container) (typed FeaturePython)
  n = 0.022
FEATURE [App::DocumentObjectGroupPython] O_element017  label="O_element : 0.712"  # scripted group (container) (typed FeaturePython)
  n = 0.712
FEATURE [App::DocumentObjectGroupPython] Na_element004  label="Na_element : 0.004"  # scripted group (container) (typed FeaturePython)
  n = 0.002
FEATURE [App::DocumentObjectGroupPython] P_element004  label="P_element : 0.004"  # scripted group (container) (typed FeaturePython)
  n = 0.004
FEATURE [App::DocumentObjectGroupPython] S_element006  label="S_element : 0.005"  # scripted group (container) (typed FeaturePython)
  n = 0.002
FEATURE [App::DocumentObjectGroupPython] Cl_element003  label="Cl_element : 0.004"  # scripted group (container) (typed FeaturePython)
  n = 0.003
FEATURE [App::DocumentObjectGroupPython] K_element002  label="K_element : 0.003"  # scripted group (container) (typed FeaturePython)
  n = 0.003
FEATURE [App::DocumentObjectGroupPython] G4_BRAIN_ICRP  # scripted group (container) (typed FeaturePython)
  Dunit = g/cm3
  Dvalue = 1.04
  Group = -> [H_element017,C_element018,N_element012,O_element017,Na_element004,P_element004,S_element006,Cl_element003,K_element002]
  conduct = 2
  density = 1
  expand = 3
  formula = G4_BRAIN_ICRP
  name = G4_BRAIN_ICRP
  specific = 4
FEATURE [App::DocumentObjectGroupPython] C_element019  label="C_element : 4"  # scripted group (container) (typed FeaturePython)
  n = 4
  ref = C_element
FEATURE [App::DocumentObjectGroupPython] H_element018  label="H_element : 010"  # scripted group (container) (typed FeaturePython)
  n = 10
  ref = H_element
FEATURE [App::DocumentObjectGroupPython] G4_BUTANE  # scripted group (container) (typed FeaturePython)
  Dunit = g/cm3
  Dvalue = 0.00249343
  Group = -> [C_element019,H_element018]
  conduct = 2
  density = 1
  expand = 3
  formula = G4_BUTANE
  name = G4_BUTANE
  specific = 4
FEATURE [App::DocumentObjectGroupPython] C_element020  label="C_element : 008"  # scripted group (container) (typed FeaturePython)
  n = 4
  ref = C_element
FEATURE [App::DocumentObjectGroupPython] H_element019  label="H_element : 011"  # scripted group (container) (typed FeaturePython)
  n = 10
  ref = H_element
FEATURE [App::DocumentObjectGroupPython] O_element018  label="O_element : 007"  # scripted group (container) (typed FeaturePython)
  n = 1
  ref = O_element
FEATURE [App::DocumentObjectGroupPython] G4_N_BUTYL_ALCOHOL  label="G4_N-BUTYL_ALCOHOL"  # scripted group (container) (typed FeaturePython)
  Dunit = g/cm3
  Dvalue = 0.8098
  Group = -> [C_element020,H_element019,O_element018]
  conduct = 2
  density = 1
  expand = 3
  formula = G4_N-BUTYL_ALCOHOL
  name = G4_N-BUTYL_ALCOHOL
  specific = 4
FEATURE [App::DocumentObjectGroupPython] H_element020  label="H_element : 0.025"  # scripted group (container) (typed FeaturePython)
  n = 0.02468
FEATURE [App::DocumentObjectGroupPython] C_element021  label="C_element : 0.502"  # scripted group (container) (typed FeaturePython)
  n = 0.501611
FEATURE [App::DocumentObjectGroupPython] O_element019  label="O_element : 0.005"  # scripted group (container) (typed FeaturePython)
  n = 0.004527
FEATURE [App::DocumentObjectGroupPython] F_element004  label="F_element : 0.465"  # scripted group (container) (typed FeaturePython)
  n = 0.465209
FEATURE [App::DocumentObjectGroupPython] Si_element001  label="Si_element : 0.004"  # scripted group (container) (typed FeaturePython)
  n = 0.003973
FEATURE [App::DocumentObjectGroupPython] G4_C_552  label="G4_C-552"  # scripted group (container) (typed FeaturePython)
  Dunit = g/cm3
  Dvalue = 1.76
  Group = -> [H_element020,C_element021,O_element019,F_element004,Si_element001]
  conduct = 2
  density = 1
  expand = 3
  formula = G4_C-552
  name = G4_C-552
  specific = 4
FEATURE [App::DocumentObjectGroupPython] Cd_element001  label="Cd_element : 1"  # scripted group (container) (typed FeaturePython)
  n = 1
  ref = Cd_element
FEATURE [App::DocumentObjectGroupPython] Te_element001  label="Te_element : 1"  # scripted group (container) (typed FeaturePython)
  n = 1
  ref = Te_element
FEATURE [App::DocumentObjectGroupPython] G4_CADMIUM_TELLURIDE  # scripted group (container) (typed FeaturePython)
  Dunit = g/cm3
  Dvalue = 6.2
  Group = -> [Cd_element001,Te_element001]
  conduct = 2
  density = 1
  expand = 3
  formula = G4_CADMIUM_TELLURIDE
  name = G4_CADMIUM_TELLURIDE
  specific = 4
FEATURE [App::DocumentObjectGroupPython] Cd_element002  label="Cd_element : 002"  # scripted group (container) (typed FeaturePython)
  n = 1
  ref = Cd_element
FEATURE [App::DocumentObjectGroupPython] W_element001  label="W_element : 1"  # scripted group (container) (typed FeaturePython)
  n = 1
  ref = W_element
FEATURE [App::DocumentObjectGroupPython] O_element020  label="O_element : 008"  # scripted group (container) (typed FeaturePython)
  n = 4
  ref = O_element
FEATURE [App::DocumentObjectGroupPython] G4_CADMIUM_TUNGSTATE  # scripted group (container) (typed FeaturePython)
  Dunit = g/cm3
  Dvalue = 7.9
  Group = -> [Cd_element002,W_element001,O_element020]
  conduct = 2
  density = 1
  expand = 3
  formula = G4_CADMIUM_TUNGSTATE
  name = G4_CADMIUM_TUNGSTATE
  specific = 4
FEATURE [App::DocumentObjectGroupPython] Ca_element005  label="Ca_element : 1"  # scripted group (container) (typed FeaturePython)
  n = 1
  ref = Ca_element
FEATURE [App::DocumentObjectGroupPython] C_element022  label="C_element : 009"  # scripted group (container) (typed FeaturePython)
  n = 1
  ref = C_element
FEATURE [App::DocumentObjectGroupPython] O_element021  label="O_element : 009"  # scripted group (container) (typed FeaturePython)
  n = 3
  ref = O_element
FEATURE [App::DocumentObjectGroupPython] G4_CALCIUM_CARBONATE  # scripted group (container) (typed FeaturePython)
  Dunit = g/cm3
  Dvalue = 2.8
  Group = -> [Ca_element005,C_element022,O_element021]
  conduct = 2
  density = 1
  expand = 3
  formula = G4_CALCIUM_CARBONATE
  name = G4_CALCIUM_CARBONATE
  specific = 4
FEATURE [App::DocumentObjectGroupPython] Ca_element006  label="Ca_element : 002"  # scripted group (container) (typed FeaturePython)
  n = 1
  ref = Ca_element
FEATURE [App::DocumentObjectGroupPython] F_element005  label="F_element : 003"  # scripted group (container) (typed FeaturePython)
  n = 2
  ref = F_element
FEATURE [App::DocumentObjectGroupPython] G4_CALCIUM_FLUORIDE  # scripted group (container) (typed FeaturePython)
  Dunit = g/cm3
  Dvalue = 3.18
  Group = -> [Ca_element006,F_element005]
  conduct = 2
  density = 1
  expand = 3
  formula = G4_CALCIUM_FLUORIDE
  name = G4_CALCIUM_FLUORIDE
  specific = 4
FEATURE [App::DocumentObjectGroupPython] Ca_element007  label="Ca_element : 003"  # scripted group (container) (typed FeaturePython)
  n = 1
  ref = Ca_element
FEATURE [App::DocumentObjectGroupPython] O_element022  label="O_element : 010"  # scripted group (container) (typed FeaturePython)
  n = 1
  ref = O_element
FEATURE [App::DocumentObjectGroupPython] G4_CALCIUM_OXIDE  # scripted group (container) (typed FeaturePython)
  Dunit = g/cm3
  Dvalue = 3.3
  Group = -> [Ca_element007,O_element022]
  conduct = 2
  density = 1
  expand = 3
  formula = G4_CALCIUM_OXIDE
  name = G4_CALCIUM_OXIDE
  specific = 4
FEATURE [App::DocumentObjectGroupPython] Ca_element008  label="Ca_element : 004"  # scripted group (container) (typed FeaturePython)
  n = 1
  ref = Ca_element
FEATURE [App::DocumentObjectGroupPython] S_element007  label="S_element : 002"  # scripted group (container) (typed FeaturePython)
  n = 1
  ref = S_element
FEATURE [App::DocumentObjectGroupPython] O_element023  label="O_element : 011"  # scripted group (container) (typed FeaturePython)
  n = 4
  ref = O_element
FEATURE [App::DocumentObjectGroupPython] G4_CALCIUM_SULFATE  # scripted group (container) (typed FeaturePython)
  Dunit = g/cm3
  Dvalue = 2.96
  Group = -> [Ca_element008,S_element007,O_element023]
  conduct = 2
  density = 1
  expand = 3
  formula = G4_CALCIUM_SULFATE
  name = G4_CALCIUM_SULFATE
  specific = 4
FEATURE [App::DocumentObjectGroupPython] Ca_element009  label="Ca_element : 005"  # scripted group (container) (typed FeaturePython)
  n = 1
  ref = Ca_element
FEATURE [App::DocumentObjectGroupPython] W_element002  label="W_element : 002"  # scripted group (container) (typed FeaturePython)
  n = 1
  ref = W_element
FEATURE [App::DocumentObjectGroupPython] O_element024  label="O_element : 012"  # scripted group (container) (typed FeaturePython)
  n = 4
  ref = O_element
FEATURE [App::DocumentObjectGroupPython] G4_CALCIUM_TUNGSTATE  # scripted group (container) (typed FeaturePython)
  Dunit = g/cm3
  Dvalue = 6.062
  Group = -> [Ca_element009,W_element002,O_element024]
  conduct = 2
  density = 1
  expand = 3
  formula = G4_CALCIUM_TUNGSTATE
  name = G4_CALCIUM_TUNGSTATE
  specific = 4
FEATURE [App::DocumentObjectGroupPython] C_element023  label="C_element : 010"  # scripted group (container) (typed FeaturePython)
  n = 1
  ref = C_element
FEATURE [App::DocumentObjectGroupPython] O_element025  label="O_element : 013"  # scripted group (container) (typed FeaturePython)
  n = 2
  ref = O_element
FEATURE [App::DocumentObjectGroupPython] G4_CARBON_DIOXIDE  # scripted group (container) (typed FeaturePython)
  Dunit = g/cm3
  Dvalue = 0.00184212
  Group = -> [C_element023,O_element025]
  conduct = 2
  density = 1
  expand = 3
  formula = G4_CARBON_DIOXIDE
  name = G4_CARBON_DIOXIDE
  specific = 4
FEATURE [App::DocumentObjectGroupPython] C_element024  label="C_element : 011"  # scripted group (container) (typed FeaturePython)
  n = 1
  ref = C_element
FEATURE [App::DocumentObjectGroupPython] Cl_element004  label="Cl_element : 4"  # scripted group (container) (typed FeaturePython)
  n = 4
  ref = Cl_element
FEATURE [App::DocumentObjectGroupPython] G4_CARBON_TETRACHLORIDE  # scripted group (container) (typed FeaturePython)
  Dunit = g/cm3
  Dvalue = 1.594
  Group = -> [C_element024,Cl_element004]
  conduct = 2
  density = 1
  expand = 3
  formula = G4_CARBON_TETRACHLORIDE
  name = G4_CARBON_TETRACHLORIDE
  specific = 4
FEATURE [App::DocumentObjectGroupPython] C_element025  label="C_element : 012"  # scripted group (container) (typed FeaturePython)
  n = 6
  ref = C_element
FEATURE [App::DocumentObjectGroupPython] H_element021  label="H_element : 012"  # scripted group (container) (typed FeaturePython)
  n = 10
  ref = H_element
FEATURE [App::DocumentObjectGroupPython] O_element026  label="O_element : 5"  # scripted group (container) (typed FeaturePython)
  n = 5
  ref = O_element
FEATURE [App::DocumentObjectGroupPython] G4_CELLULOSE_CELLOPHANE  # scripted group (container) (typed FeaturePython)
  Dunit = g/cm3
  Dvalue = 1.42
  Group = -> [C_element025,H_element021,O_element026]
  conduct = 2
  density = 1
  expand = 3
  formula = G4_CELLULOSE_CELLOPHANE
  name = G4_CELLULOSE_CELLOPHANE
  specific = 4
FEATURE [App::DocumentObjectGroupPython] H_element022  label="H_element : 0.067"  # scripted group (container) (typed FeaturePython)
  n = 0.067125
FEATURE [App::DocumentObjectGroupPython] C_element026  label="C_element : 0.545"  # scripted group (container) (typed FeaturePython)
  n = 0.545403
FEATURE [App::DocumentObjectGroupPython] O_element027  label="O_element : 0.387"  # scripted group (container) (typed FeaturePython)
  n = 0.387472
FEATURE [App::DocumentObjectGroupPython] G4_CELLULOSE_BUTYRATE  # scripted group (container) (typed FeaturePython)
  Dunit = g/cm3
  Dvalue = 1.2
  Group = -> [H_element022,C_element026,O_element027]
  conduct = 2
  density = 1
  expand = 3
  formula = G4_CELLULOSE_BUTYRATE
  name = G4_CELLULOSE_BUTYRATE
  specific = 4
FEATURE [App::DocumentObjectGroupPython] H_element023  label="H_element : 0.029"  # scripted group (container) (typed FeaturePython)
  n = 0.029216
FEATURE [App::DocumentObjectGroupPython] C_element027  label="C_element : 0.271"  # scripted group (container) (typed FeaturePython)
  n = 0.271296
FEATURE [App::DocumentObjectGroupPython] N_element013  label="N_element : 0.121"  # scripted group (container) (typed FeaturePython)
  n = 0.121276
FEATURE [App::DocumentObjectGroupPython] O_element028  label="O_element : 0.578"  # scripted group (container) (typed FeaturePython)
  n = 0.578212
FEATURE [App::DocumentObjectGroupPython] G4_CELLULOSE_NITRATE  # scripted group (container) (typed FeaturePython)
  Dunit = g/cm3
  Dvalue = 1.49
  Group = -> [H_element023,C_element027,N_element013,O_element028]
  conduct = 2
  density = 1
  expand = 3
  formula = G4_CELLULOSE_NITRATE
  name = G4_CELLULOSE_NITRATE
  specific = 4
FEATURE [App::DocumentObjectGroupPython] H_element024  label="H_element : 0.108"  # scripted group (container) (typed FeaturePython)
  n = 0.107596
FEATURE [App::DocumentObjectGroupPython] N_element014  label="N_element : 0.001"  # scripted group (container) (typed FeaturePython)
  n = 0.0008
FEATURE [App::DocumentObjectGroupPython] O_element029  label="O_element : 0.875"  # scripted group (container) (typed FeaturePython)
  n = 0.874976
FEATURE [App::DocumentObjectGroupPython] S_element008  label="S_element : 0.015"  # scripted group (container) (typed FeaturePython)
  n = 0.014627
FEATURE [App::DocumentObjectGroupPython] Ce_element001  label="Ce_element : 0.002"  # scripted group (container) (typed FeaturePython)
  n = 0.002001
FEATURE [App::DocumentObjectGroupPython] G4_CERIC_SULFATE  # scripted group (container) (typed FeaturePython)
  Dunit = g/cm3
  Dvalue = 1.03
  Group = -> [H_element024,N_element014,O_element029,S_element008,Ce_element001]
  conduct = 2
  density = 1
  expand = 3
  formula = G4_CERIC_SULFATE
  name = G4_CERIC_SULFATE
  specific = 4
FEATURE [App::DocumentObjectGroupPython] Cs_element001  label="Cs_element : 1"  # scripted group (container) (typed FeaturePython)
  n = 1
  ref = Cs_element
FEATURE [App::DocumentObjectGroupPython] F_element006  label="F_element : 1"  # scripted group (container) (typed FeaturePython)
  n = 1
  ref = F_element
FEATURE [App::DocumentObjectGroupPython] G4_CESIUM_FLUORIDE  # scripted group (container) (typed FeaturePython)
  Dunit = g/cm3
  Dvalue = 4.115
  Group = -> [Cs_element001,F_element006]
  conduct = 2
  density = 1
  expand = 3
  formula = G4_CESIUM_FLUORIDE
  name = G4_CESIUM_FLUORIDE
  specific = 4
FEATURE [App::DocumentObjectGroupPython] Cs_element002  label="Cs_element : 002"  # scripted group (container) (typed FeaturePython)
  n = 1
  ref = Cs_element
FEATURE [App::DocumentObjectGroupPython] I_element001  label="I_element : 1"  # scripted group (container) (typed FeaturePython)
  n = 1
  ref = I_element
FEATURE [App::DocumentObjectGroupPython] G4_CESIUM_IODIDE  # scripted group (container) (typed FeaturePython)
  Dunit = g/cm3
  Dvalue = 4.51
  Group = -> [Cs_element002,I_element001]
  conduct = 2
  density = 1
  expand = 3
  formula = G4_CESIUM_IODIDE
  name = G4_CESIUM_IODIDE
  specific = 4
FEATURE [App::DocumentObjectGroupPython] C_element028  label="C_element : 013"  # scripted group (container) (typed FeaturePython)
  n = 6
  ref = C_element
FEATURE [App::DocumentObjectGroupPython] H_element025  label="H_element : 013"  # scripted group (container) (typed FeaturePython)
  n = 5
  ref = H_element
FEATURE [App::DocumentObjectGroupPython] Cl_element005  label="Cl_element : 1"  # scripted group (container) (typed FeaturePython)
  n = 1
  ref = Cl_element
FEATURE [App::DocumentObjectGroupPython] G4_CHLOROBENZENE  # scripted group (container) (typed FeaturePython)
  Dunit = g/cm3
  Dvalue = 1.1058
  Group = -> [C_element028,H_element025,Cl_element005]
  conduct = 2
  density = 1
  expand = 3
  formula = G4_CHLOROBENZENE
  name = G4_CHLOROBENZENE
  specific = 4
FEATURE [App::DocumentObjectGroupPython] C_element029  label="C_element : 014"  # scripted group (container) (typed FeaturePython)
  n = 1
  ref = C_element
FEATURE [App::DocumentObjectGroupPython] H_element026  label="H_element : 1"  # scripted group (container) (typed FeaturePython)
  n = 1
  ref = H_element
FEATURE [App::DocumentObjectGroupPython] Cl_element006  label="Cl_element : 3"  # scripted group (container) (typed FeaturePython)
  n = 3
  ref = Cl_element
FEATURE [App::DocumentObjectGroupPython] G4_CHLOROFORM  # scripted group (container) (typed FeaturePython)
  Dunit = g/cm3
  Dvalue = 1.4832
  Group = -> [C_element029,H_element026,Cl_element006]
  conduct = 2
  density = 1
  expand = 3
  formula = G4_CHLOROFORM
  name = G4_CHLOROFORM
  specific = 4
FEATURE [App::DocumentObjectGroupPython] H_element027  label="H_element : 0.010"  # scripted group (container) (typed FeaturePython)
  n = 0.01
FEATURE [App::DocumentObjectGroupPython] C_element030  label="C_element : 0.001"  # scripted group (container) (typed FeaturePython)
  n = 0.001
FEATURE [App::DocumentObjectGroupPython] O_element030  label="O_element : 0.529"  # scripted group (container) (typed FeaturePython)
  n = 0.529107
FEATURE [App::DocumentObjectGroupPython] Na_element005  label="Na_element : 0.016"  # scripted group (container) (typed FeaturePython)
  n = 0.016
FEATURE [App::DocumentObjectGroupPython] Mg_element003  label="Mg_element : 0.004"  # scripted group (container) (typed FeaturePython)
  n = 0.002
FEATURE [App::DocumentObjectGroupPython] Al_element002  label="Al_element : 0.034"  # scripted group (container) (typed FeaturePython)
  n = 0.033872
FEATURE [App::DocumentObjectGroupPython] Si_element002  label="Si_element : 0.337"  # scripted group (container) (typed FeaturePython)
  n = 0.337021
FEATURE [App::DocumentObjectGroupPython] K_element003  label="K_element : 0.013"  # scripted group (container) (typed FeaturePython)
  n = 0.013
FEATURE [App::DocumentObjectGroupPython] Ca_element010  label="Ca_element : 0.044"  # scripted group (container) (typed FeaturePython)
  n = 0.044
FEATURE [App::DocumentObjectGroupPython] Fe_element002  label="Fe_element : 0.014"  # scripted group (container) (typed FeaturePython)
  n = 0.014
FEATURE [App::DocumentObjectGroupPython] G4_CONCRETE  # scripted group (container) (typed FeaturePython)
  Dunit = g/cm3
  Dvalue = 2.3
  Group = -> [H_element027,C_element030,O_element030,Na_element005,Mg_element003,Al_element002,Si_element002,K_element003,Ca_element010,Fe_element002]
  conduct = 2
  density = 1
  expand = 3
  formula = G4_CONCRETE
  name = G4_CONCRETE
  specific = 4
FEATURE [App::DocumentObjectGroupPython] C_element031  label="C_element : 015"  # scripted group (container) (typed FeaturePython)
  n = 6
  ref = C_element
FEATURE [App::DocumentObjectGroupPython] H_element028  label="H_element : 12"  # scripted group (container) (typed FeaturePython)
  n = 12
  ref = H_element
FEATURE [App::DocumentObjectGroupPython] G4_CYCLOHEXANE  # scripted group (container) (typed FeaturePython)
  Dunit = g/cm3
  Dvalue = 0.779
  Group = -> [C_element031,H_element028]
  conduct = 2
  density = 1
  expand = 3
  formula = G4_CYCLOHEXANE
  name = G4_CYCLOHEXANE
  specific = 4
FEATURE [App::DocumentObjectGroupPython] C_element032  label="C_element : 016"  # scripted group (container) (typed FeaturePython)
  n = 6
  ref = C_element
FEATURE [App::DocumentObjectGroupPython] H_element029  label="H_element : 4"  # scripted group (container) (typed FeaturePython)
  n = 4
  ref = H_element
FEATURE [App::DocumentObjectGroupPython] Cl_element007  label="Cl_element : 2"  # scripted group (container) (typed FeaturePython)
  n = 2
  ref = Cl_element
FEATURE [App::DocumentObjectGroupPython] G4_1_2_DICHLOROBENZENE  label="G4_1.2-DICHLOROBENZENE"  # scripted group (container) (typed FeaturePython)
  Dunit = g/cm3
  Dvalue = 1.3048
  Group = -> [C_element032,H_element029,Cl_element007]
  conduct = 2
  density = 1
  expand = 3
  formula = G4_1.2-DICHLOROBENZENE
  name = G4_1.2-DICHLOROBENZENE
  specific = 4
FEATURE [App::DocumentObjectGroupPython] C_element033  label="C_element : 017"  # scripted group (container) (typed FeaturePython)
  n = 4
  ref = C_element
FEATURE [App::DocumentObjectGroupPython] H_element030  label="H_element : 8"  # scripted group (container) (typed FeaturePython)
  n = 8
  ref = H_element
FEATURE [App::DocumentObjectGroupPython] O_element031  label="O_element : 014"  # scripted group (container) (typed FeaturePython)
  n = 1
  ref = O_element
FEATURE [App::DocumentObjectGroupPython] Cl_element008  label="Cl_element : 005"  # scripted group (container) (typed FeaturePython)
  n = 2
  ref = Cl_element
FEATURE [App::DocumentObjectGroupPython] G4_DICHLORODIETHYL_ETHER  # scripted group (container) (typed FeaturePython)
  Dunit = g/cm3
  Dvalue = 1.2199
  Group = -> [C_element033,H_element030,O_element031,Cl_element008]
  conduct = 2
  density = 1
  expand = 3
  formula = G4_DICHLORODIETHYL_ETHER
  name = G4_DICHLORODIETHYL_ETHER
  specific = 4
FEATURE [App::DocumentObjectGroupPython] C_element034  label="C_element : 018"  # scripted group (container) (typed FeaturePython)
  n = 2
  ref = C_element
FEATURE [App::DocumentObjectGroupPython] H_element031  label="H_element : 014"  # scripted group (container) (typed FeaturePython)
  n = 4
  ref = H_element
FEATURE [App::DocumentObjectGroupPython] Cl_element009  label="Cl_element : 006"  # scripted group (container) (typed FeaturePython)
  n = 2
  ref = Cl_element
FEATURE [App::DocumentObjectGroupPython] G4_1_2_DICHLOROETHANE  label="G4_1.2-DICHLOROETHANE"  # scripted group (container) (typed FeaturePython)
  Dunit = g/cm3
  Dvalue = 1.2351
  Group = -> [C_element034,H_element031,Cl_element009]
  conduct = 2
  density = 1
  expand = 3
  formula = G4_1.2-DICHLOROETHANE
  name = G4_1.2-DICHLOROETHANE
  specific = 4
FEATURE [App::DocumentObjectGroupPython] C_element035  label="C_element : 019"  # scripted group (container) (typed FeaturePython)
  n = 4
  ref = C_element
FEATURE [App::DocumentObjectGroupPython] H_element032  label="H_element : 015"  # scripted group (container) (typed FeaturePython)
  n = 10
  ref = H_element
FEATURE [App::DocumentObjectGroupPython] O_element032  label="O_element : 015"  # scripted group (container) (typed FeaturePython)
  n = 1
  ref = O_element
FEATURE [App::DocumentObjectGroupPython] G4_DIETHYL_ETHER  # scripted group (container) (typed FeaturePython)
  Dunit = g/cm3
  Dvalue = 0.71378
  Group = -> [C_element035,H_element032,O_element032]
  conduct = 2
  density = 1
  expand = 3
  formula = G4_DIETHYL_ETHER
  name = G4_DIETHYL_ETHER
  specific = 4
FEATURE [App::DocumentObjectGroupPython] C_element036  label="C_element : 020"  # scripted group (container) (typed FeaturePython)
  n = 3
  ref = C_element
FEATURE [App::DocumentObjectGroupPython] H_element033  label="H_element : 016"  # scripted group (container) (typed FeaturePython)
  n = 7
  ref = H_element
FEATURE [App::DocumentObjectGroupPython] N_element015  label="N_element : 008"  # scripted group (container) (typed FeaturePython)
  n = 1
  ref = N_element
FEATURE [App::DocumentObjectGroupPython] O_element033  label="O_element : 016"  # scripted group (container) (typed FeaturePython)
  n = 1
  ref = O_element
FEATURE [App::DocumentObjectGroupPython] G4_N_N_DIMETHYL_FORMAMIDE  label="G4_N.N-DIMETHYL_FORMAMIDE"  # scripted group (container) (typed FeaturePython)
  Dunit = g/cm3
  Dvalue = 0.9487
  Group = -> [C_element036,H_element033,N_element015,O_element033]
  conduct = 2
  density = 1
  expand = 3
  formula = G4_N.N-DIMETHYL_FORMAMIDE
  name = G4_N.N-DIMETHYL_FORMAMIDE
  specific = 4
FEATURE [App::DocumentObjectGroupPython] C_element037  label="C_element : 021"  # scripted group (container) (typed FeaturePython)
  n = 2
  ref = C_element
FEATURE [App::DocumentObjectGroupPython] H_element034  label="H_element : 017"  # scripted group (container) (typed FeaturePython)
  n = 6
  ref = H_element
FEATURE [App::DocumentObjectGroupPython] O_element034  label="O_element : 017"  # scripted group (container) (typed FeaturePython)
  n = 1
  ref = O_element
FEATURE [App::DocumentObjectGroupPython] S_element009  label="S_element : 003"  # scripted group (container) (typed FeaturePython)
  n = 1
  ref = S_element
FEATURE [App::DocumentObjectGroupPython] G4_DIMETHYL_SULFOXIDE  # scripted group (container) (typed FeaturePython)
  Dunit = g/cm3
  Dvalue = 1.1014
  Group = -> [C_element037,H_element034,O_element034,S_element009]
  conduct = 2
  density = 1
  expand = 3
  formula = G4_DIMETHYL_SULFOXIDE
  name = G4_DIMETHYL_SULFOXIDE
  specific = 4
FEATURE [App::DocumentObjectGroupPython] C_element038  label="C_element : 022"  # scripted group (container) (typed FeaturePython)
  n = 2
  ref = C_element
FEATURE [App::DocumentObjectGroupPython] H_element035  label="H_element : 018"  # scripted group (container) (typed FeaturePython)
  n = 6
  ref = H_element
FEATURE [App::DocumentObjectGroupPython] G4_ETHANE  # scripted group (container) (typed FeaturePython)
  Dunit = g/cm3
  Dvalue = 0.00125324
  Group = -> [C_element038,H_element035]
  conduct = 2
  density = 1
  expand = 3
  formula = G4_ETHANE
  name = G4_ETHANE
  specific = 4
FEATURE [App::DocumentObjectGroupPython] C_element039  label="C_element : 023"  # scripted group (container) (typed FeaturePython)
  n = 2
  ref = C_element
FEATURE [App::DocumentObjectGroupPython] H_element036  label="H_element : 019"  # scripted group (container) (typed FeaturePython)
  n = 6
  ref = H_element
FEATURE [App::DocumentObjectGroupPython] O_element035  label="O_element : 018"  # scripted group (container) (typed FeaturePython)
  n = 1
  ref = O_element
FEATURE [App::DocumentObjectGroupPython] G4_ETHYL_ALCOHOL  # scripted group (container) (typed FeaturePython)
  Dunit = g/cm3
  Dvalue = 0.7893
  Group = -> [C_element039,H_element036,O_element035]
  conduct = 2
  density = 1
  expand = 3
  formula = G4_ETHYL_ALCOHOL
  name = G4_ETHYL_ALCOHOL
  specific = 4
FEATURE [App::DocumentObjectGroupPython] H_element037  label="H_element : 0.090"  # scripted group (container) (typed FeaturePython)
  n = 0.090027
FEATURE [App::DocumentObjectGroupPython] C_element040  label="C_element : 0.585"  # scripted group (container) (typed FeaturePython)
  n = 0.585182
FEATURE [App::DocumentObjectGroupPython] O_element036  label="O_element : 0.325"  # scripted group (container) (typed FeaturePython)
  n = 0.324791
FEATURE [App::DocumentObjectGroupPython] G4_ETHYL_CELLULOSE  # scripted group (container) (typed FeaturePython)
  Dunit = g/cm3
  Dvalue = 1.13
  Group = -> [H_element037,C_element040,O_element036]
  conduct = 2
  density = 1
  expand = 3
  formula = G4_ETHYL_CELLULOSE
  name = G4_ETHYL_CELLULOSE
  specific = 4
FEATURE [App::DocumentObjectGroupPython] C_element041  label="C_element : 024"  # scripted group (container) (typed FeaturePython)
  n = 2
  ref = C_element
FEATURE [App::DocumentObjectGroupPython] H_element038  label="H_element : 020"  # scripted group (container) (typed FeaturePython)
  n = 4
  ref = H_element
FEATURE [App::DocumentObjectGroupPython] G4_ETHYLENE  # scripted group (container) (typed FeaturePython)
  Dunit = g/cm3
  Dvalue = 0.00117497
  Group = -> [C_element041,H_element038]
  conduct = 2
  density = 1
  expand = 3
  formula = G4_ETHYLENE
  name = G4_ETHYLENE
  specific = 4
FEATURE [App::DocumentObjectGroupPython] H_element039  label="H_element : 0.096"  # scripted group (container) (typed FeaturePython)
  n = 0.096
FEATURE [App::DocumentObjectGroupPython] C_element042  label="C_element : 0.195"  # scripted group (container) (typed FeaturePython)
  n = 0.195
FEATURE [App::DocumentObjectGroupPython] N_element016  label="N_element : 0.057"  # scripted group (container) (typed FeaturePython)
  n = 0.057
FEATURE [App::DocumentObjectGroupPython] O_element037  label="O_element : 0.646"  # scripted group (container) (typed FeaturePython)
  n = 0.646
FEATURE [App::DocumentObjectGroupPython] Na_element006  label="Na_element : 0.017"  # scripted group (container) (typed FeaturePython)
  n = 0.001
FEATURE [App::DocumentObjectGroupPython] P_element005  label="P_element : 0.104"  # scripted group (container) (typed FeaturePython)
  n = 0.001
FEATURE [App::DocumentObjectGroupPython] S_element010  label="S_element : 0.016"  # scripted group (container) (typed FeaturePython)
  n = 0.003
FEATURE [App::DocumentObjectGroupPython] Cl_element010  label="Cl_element : 0.005"  # scripted group (container) (typed FeaturePython)
  n = 0.001
FEATURE [App::DocumentObjectGroupPython] G4_EYE_LENS_ICRP  # scripted group (container) (typed FeaturePython)
  Dunit = g/cm3
  Dvalue = 1.07
  Group = -> [H_element039,C_element042,N_element016,O_element037,Na_element006,P_element005,S_element010,Cl_element010]
  conduct = 2
  density = 1
  expand = 3
  formula = G4_EYE_LENS_ICRP
  name = G4_EYE_LENS_ICRP
  specific = 4
FEATURE [App::DocumentObjectGroupPython] Fe_element003  label="Fe_element : 2"  # scripted group (container) (typed FeaturePython)
  n = 2
  ref = Fe_element
FEATURE [App::DocumentObjectGroupPython] O_element038  label="O_element : 019"  # scripted group (container) (typed FeaturePython)
  n = 3
  ref = O_element
FEATURE [App::DocumentObjectGroupPython] G4_FERRIC_OXIDE  # scripted group (container) (typed FeaturePython)
  Dunit = g/cm3
  Dvalue = 5.2
  Group = -> [Fe_element003,O_element038]
  conduct = 2
  density = 1
  expand = 3
  formula = G4_FERRIC_OXIDE
  name = G4_FERRIC_OXIDE
  specific = 4
FEATURE [App::DocumentObjectGroupPython] Fe_element004  label="Fe_element : 1"  # scripted group (container) (typed FeaturePython)
  n = 1
  ref = Fe_element
FEATURE [App::DocumentObjectGroupPython] B_element003  label="B_element : 1"  # scripted group (container) (typed FeaturePython)
  n = 1
  ref = B_element
FEATURE [App::DocumentObjectGroupPython] G4_FERROBORIDE  # scripted group (container) (typed FeaturePython)
  Dunit = g/cm3
  Dvalue = 7.15
  Group = -> [Fe_element004,B_element003]
  conduct = 2
  density = 1
  expand = 3
  formula = G4_FERROBORIDE
  name = G4_FERROBORIDE
  specific = 4
FEATURE [App::DocumentObjectGroupPython] Fe_element005  label="Fe_element : 003"  # scripted group (container) (typed FeaturePython)
  n = 1
  ref = Fe_element
FEATURE [App::DocumentObjectGroupPython] O_element039  label="O_element : 020"  # scripted group (container) (typed FeaturePython)
  n = 1
  ref = O_element
FEATURE [App::DocumentObjectGroupPython] G4_FERROUS_OXIDE  # scripted group (container) (typed FeaturePython)
  Dunit = g/cm3
  Dvalue = 5.7
  Group = -> [Fe_element005,O_element039]
  conduct = 2
  density = 1
  expand = 3
  formula = G4_FERROUS_OXIDE
  name = G4_FERROUS_OXIDE
  specific = 4
FEATURE [App::DocumentObjectGroupPython] H_element040  label="H_element : 0.115"  # scripted group (container) (typed FeaturePython)
  n = 0.108259
FEATURE [App::DocumentObjectGroupPython] N_element017  label="N_element : 0.000"  # scripted group (container) (typed FeaturePython)
  n = 2.7e-05
FEATURE [App::DocumentObjectGroupPython] O_element040  label="O_element : 0.879"  # scripted group (container) (typed FeaturePython)
  n = 0.878636
FEATURE [App::DocumentObjectGroupPython] Na_element007  label="Na_element : 0.000"  # scripted group (container) (typed FeaturePython)
  n = 2.2e-05
FEATURE [App::DocumentObjectGroupPython] S_element011  label="S_element : 0.013"  # scripted group (container) (typed FeaturePython)
  n = 0.012968
FEATURE [App::DocumentObjectGroupPython] Cl_element011  label="Cl_element : 0.000"  # scripted group (container) (typed FeaturePython)
  n = 3.4e-05
FEATURE [App::DocumentObjectGroupPython] Fe_element006  label="Fe_element : 0.000"  # scripted group (container) (typed FeaturePython)
  n = 5.4e-05
FEATURE [App::DocumentObjectGroupPython] G4_FERROUS_SULFATE  # scripted group (container) (typed FeaturePython)
  Dunit = g/cm3
  Dvalue = 1.024
  Group = -> [H_element040,N_element017,O_element040,Na_element007,S_element011,Cl_element011,Fe_element006]
  conduct = 2
  density = 1
  expand = 3
  formula = G4_FERROUS_SULFATE
  name = G4_FERROUS_SULFATE
  specific = 4
FEATURE [App::DocumentObjectGroupPython] C_element043  label="C_element : 0.099"  # scripted group (container) (typed FeaturePython)
  n = 0.099335
FEATURE [App::DocumentObjectGroupPython] F_element007  label="F_element : 0.314"  # scripted group (container) (typed FeaturePython)
  n = 0.314247
FEATURE [App::DocumentObjectGroupPython] Cl_element012  label="Cl_element : 0.586"  # scripted group (container) (typed FeaturePython)
  n = 0.586418
FEATURE [App::DocumentObjectGroupPython] G4_FREON_12  label="G4_FREON-12"  # scripted group (container) (typed FeaturePython)
  Dunit = g/cm3
  Dvalue = 1.12
  Group = -> [C_element043,F_element007,Cl_element012]
  conduct = 2
  density = 1
  expand = 3
  formula = G4_FREON-12
  name = G4_FREON-12
  specific = 4
FEATURE [App::DocumentObjectGroupPython] C_element044  label="C_element : 0.057"  # scripted group (container) (typed FeaturePython)
  n = 0.057245
FEATURE [App::DocumentObjectGroupPython] F_element008  label="F_element : 0.181"  # scripted group (container) (typed FeaturePython)
  n = 0.181096
FEATURE [App::DocumentObjectGroupPython] Br_element001  label="Br_element : 0.762"  # scripted group (container) (typed FeaturePython)
  n = 0.761659
FEATURE [App::DocumentObjectGroupPython] G4_FREON_12B2  label="G4_FREON-12B2"  # scripted group (container) (typed FeaturePython)
  Dunit = g/cm3
  Dvalue = 1.8
  Group = -> [C_element044,F_element008,Br_element001]
  conduct = 2
  density = 1
  expand = 3
  formula = G4_FREON-12B2
  name = G4_FREON-12B2
  specific = 4
FEATURE [App::DocumentObjectGroupPython] C_element045  label="C_element : 0.115"  # scripted group (container) (typed FeaturePython)
  n = 0.114983
FEATURE [App::DocumentObjectGroupPython] F_element009  label="F_element : 0.546"  # scripted group (container) (typed FeaturePython)
  n = 0.545621
FEATURE [App::DocumentObjectGroupPython] Cl_element013  label="Cl_element : 0.339"  # scripted group (container) (typed FeaturePython)
  n = 0.339396
FEATURE [App::DocumentObjectGroupPython] G4_FREON_13  label="G4_FREON-13"  # scripted group (container) (typed FeaturePython)
  Dunit = g/cm3
  Dvalue = 0.95
  Group = -> [C_element045,F_element009,Cl_element013]
  conduct = 2
  density = 1
  expand = 3
  formula = G4_FREON-13
  name = G4_FREON-13
  specific = 4
FEATURE [App::DocumentObjectGroupPython] C_element046  label="C_element : 025"  # scripted group (container) (typed FeaturePython)
  n = 1
  ref = C_element
FEATURE [App::DocumentObjectGroupPython] F_element010  label="F_element : 3"  # scripted group (container) (typed FeaturePython)
  n = 3
  ref = F_element
FEATURE [App::DocumentObjectGroupPython] Br_element002  label="Br_element : 1"  # scripted group (container) (typed FeaturePython)
  n = 1
  ref = Br_element
FEATURE [App::DocumentObjectGroupPython] G4_FREON_13B1  label="G4_FREON-13B1"  # scripted group (container) (typed FeaturePython)
  Dunit = g/cm3
  Dvalue = 1.5
  Group = -> [C_element046,F_element010,Br_element002]
  conduct = 2
  density = 1
  expand = 3
  formula = G4_FREON-13B1
  name = G4_FREON-13B1
  specific = 4
FEATURE [App::DocumentObjectGroupPython] C_element047  label="C_element : 0.061"  # scripted group (container) (typed FeaturePython)
  n = 0.061309
FEATURE [App::DocumentObjectGroupPython] F_element011  label="F_element : 0.291"  # scripted group (container) (typed FeaturePython)
  n = 0.290924
FEATURE [App::DocumentObjectGroupPython] I_element002  label="I_element : 0.648"  # scripted group (container) (typed FeaturePython)
  n = 0.647767
FEATURE [App::DocumentObjectGroupPython] G4_FREON_13I1  label="G4_FREON-13I1"  # scripted group (container) (typed FeaturePython)
  Dunit = g/cm3
  Dvalue = 1.8
  Group = -> [C_element047,F_element011,I_element002]
  conduct = 2
  density = 1
  expand = 3
  formula = G4_FREON-13I1
  name = G4_FREON-13I1
  specific = 4
FEATURE [App::DocumentObjectGroupPython] Gd_element001  label="Gd_element : 2"  # scripted group (container) (typed FeaturePython)
  n = 2
  ref = Gd_element
FEATURE [App::DocumentObjectGroupPython] O_element041  label="O_element : 021"  # scripted group (container) (typed FeaturePython)
  n = 2
  ref = O_element
FEATURE [App::DocumentObjectGroupPython] S_element012  label="S_element : 004"  # scripted group (container) (typed FeaturePython)
  n = 1
  ref = S_element
FEATURE [App::DocumentObjectGroupPython] G4_GADOLINIUM_OXYSULFIDE  # scripted group (container) (typed FeaturePython)
  Dunit = g/cm3
  Dvalue = 7.44
  Group = -> [Gd_element001,O_element041,S_element012]
  conduct = 2
  density = 1
  expand = 3
  formula = G4_GADOLINIUM_OXYSULFIDE
  name = G4_GADOLINIUM_OXYSULFIDE
  specific = 4
FEATURE [App::DocumentObjectGroupPython] Ga_element001  label="Ga_element : 1"  # scripted group (container) (typed FeaturePython)
  n = 1
  ref = Ga_element
FEATURE [App::DocumentObjectGroupPython] As_element001  label="As_element : 1"  # scripted group (container) (typed FeaturePython)
  n = 1
  ref = As_element
FEATURE [App::DocumentObjectGroupPython] G4_GALLIUM_ARSENIDE  # scripted group (container) (typed FeaturePython)
  Dunit = g/cm3
  Dvalue = 5.31
  Group = -> [Ga_element001,As_element001]
  conduct = 2
  density = 1
  expand = 3
  formula = G4_GALLIUM_ARSENIDE
  name = G4_GALLIUM_ARSENIDE
  specific = 4
FEATURE [App::DocumentObjectGroupPython] H_element041  label="H_element : 0.081"  # scripted group (container) (typed FeaturePython)
  n = 0.08118
FEATURE [App::DocumentObjectGroupPython] C_element048  label="C_element : 0.416"  # scripted group (container) (typed FeaturePython)
  n = 0.41606
FEATURE [App::DocumentObjectGroupPython] N_element018  label="N_element : 0.111"  # scripted group (container) (typed FeaturePython)
  n = 0.11124
FEATURE [App::DocumentObjectGroupPython] O_element042  label="O_element : 0.381"  # scripted group (container) (typed FeaturePython)
  n = 0.38064
FEATURE [App::DocumentObjectGroupPython] S_element013  label="S_element : 0.011"  # scripted group (container) (typed FeaturePython)
  n = 0.01088
FEATURE [App::DocumentObjectGroupPython] G4_GEL_PHOTO_EMULSION  # scripted group (container) (typed FeaturePython)
  Dunit = g/cm3
  Dvalue = 1.2914
  Group = -> [H_element041,C_element048,N_element018,O_element042,S_element013]
  conduct = 2
  density = 1
  expand = 3
  formula = G4_GEL_PHOTO_EMULSION
  name = G4_GEL_PHOTO_EMULSION
  specific = 4
FEATURE [App::DocumentObjectGroupPython] B_element004  label="B_element : 0.040"  # scripted group (container) (typed FeaturePython)
  n = 0.0400639
FEATURE [App::DocumentObjectGroupPython] O_element043  label="O_element : 0.540"  # scripted group (container) (typed FeaturePython)
  n = 0.539561
FEATURE [App::DocumentObjectGroupPython] Na_element008  label="Na_element : 0.028"  # scripted group (container) (typed FeaturePython)
  n = 0.0281909
FEATURE [App::DocumentObjectGroupPython] Al_element003  label="Al_element : 0.012"  # scripted group (container) (typed FeaturePython)
  n = 0.011644
FEATURE [App::DocumentObjectGroupPython] Si_element003  label="Si_element : 0.377"  # scripted group (container) (typed FeaturePython)
  n = 0.377219
FEATURE [App::DocumentObjectGroupPython] K_element004  label="K_element : 0.014"  # scripted group (container) (typed FeaturePython)
  n = 0.00332099
FEATURE [App::DocumentObjectGroupPython] G4_Pyrex_Glass  # scripted group (container) (typed FeaturePython)
  Dunit = g/cm3
  Dvalue = 2.23
  Group = -> [B_element004,O_element043,Na_element008,Al_element003,Si_element003,K_element004]
  conduct = 2
  density = 1
  expand = 3
  formula = G4_Pyrex_Glass
  name = G4_Pyrex_Glass
  specific = 4
FEATURE [App::DocumentObjectGroupPython] O_element044  label="O_element : 0.156"  # scripted group (container) (typed FeaturePython)
  n = 0.156453
FEATURE [App::DocumentObjectGroupPython] Si_element004  label="Si_element : 0.081"  # scripted group (container) (typed FeaturePython)
  n = 0.080866
FEATURE [App::DocumentObjectGroupPython] Ti_element001  label="Ti_element : 0.008"  # scripted group (container) (typed FeaturePython)
  n = 0.008092
FEATURE [App::DocumentObjectGroupPython] As_element002  label="As_element : 0.003"  # scripted group (container) (typed FeaturePython)
  n = 0.002651
FEATURE [App::DocumentObjectGroupPython] Pb_element001  label="Pb_element : 0.752"  # scripted group (container) (typed FeaturePython)
  n = 0.751938
FEATURE [App::DocumentObjectGroupPython] G4_GLASS_LEAD  # scripted group (container) (typed FeaturePython)
  Dunit = g/cm3
  Dvalue = 6.22
  Group = -> [O_element044,Si_element004,Ti_element001,As_element002,Pb_element001]
  conduct = 2
  density = 1
  expand = 3
  formula = G4_GLASS_LEAD
  name = G4_GLASS_LEAD
  specific = 4
FEATURE [App::DocumentObjectGroupPython] O_element045  label="O_element : 0.460"  # scripted group (container) (typed FeaturePython)
  n = 0.4598
FEATURE [App::DocumentObjectGroupPython] Na_element009  label="Na_element : 0.096"  # scripted group (container) (typed FeaturePython)
  n = 0.0964411
FEATURE [App::DocumentObjectGroupPython] Si_element005  label="Si_element : 0.378"  # scripted group (container) (typed FeaturePython)
  n = 0.336553
FEATURE [App::DocumentObjectGroupPython] Ca_element011  label="Ca_element : 0.107"  # scripted group (container) (typed FeaturePython)
  n = 0.107205
FEATURE [App::DocumentObjectGroupPython] G4_GLASS_PLATE  # scripted group (container) (typed FeaturePython)
  Dunit = g/cm3
  Dvalue = 2.4
  Group = -> [O_element045,Na_element009,Si_element005,Ca_element011]
  conduct = 2
  density = 1
  expand = 3
  formula = G4_GLASS_PLATE
  name = G4_GLASS_PLATE
  specific = 4
FEATURE [App::DocumentObjectGroupPython] C_element049  label="C_element : 026"  # scripted group (container) (typed FeaturePython)
  n = 5
  ref = C_element
FEATURE [App::DocumentObjectGroupPython] H_element042  label="H_element : 021"  # scripted group (container) (typed FeaturePython)
  n = 10
  ref = H_element
FEATURE [App::DocumentObjectGroupPython] N_element019  label="N_element : 2"  # scripted group (container) (typed FeaturePython)
  n = 2
  ref = N_element
FEATURE [App::DocumentObjectGroupPython] O_element046  label="O_element : 022"  # scripted group (container) (typed FeaturePython)
  n = 3
  ref = O_element
FEATURE [App::DocumentObjectGroupPython] G4_GLUTAMINE  # scripted group (container) (typed FeaturePython)
  Dunit = g/cm3
  Dvalue = 1.46
  Group = -> [C_element049,H_element042,N_element019,O_element046]
  conduct = 2
  density = 1
  expand = 3
  formula = G4_GLUTAMINE
  name = G4_GLUTAMINE
  specific = 4
FEATURE [App::DocumentObjectGroupPython] C_element050  label="C_element : 027"  # scripted group (container) (typed FeaturePython)
  n = 3
  ref = C_element
FEATURE [App::DocumentObjectGroupPython] H_element043  label="H_element : 022"  # scripted group (container) (typed FeaturePython)
  n = 8
  ref = H_element
FEATURE [App::DocumentObjectGroupPython] O_element047  label="O_element : 023"  # scripted group (container) (typed FeaturePython)
  n = 3
  ref = O_element
FEATURE [App::DocumentObjectGroupPython] G4_GLYCEROL  # scripted group (container) (typed FeaturePython)
  Dunit = g/cm3
  Dvalue = 1.2613
  Group = -> [C_element050,H_element043,O_element047]
  conduct = 2
  density = 1
  expand = 3
  formula = G4_GLYCEROL
  name = G4_GLYCEROL
  specific = 4
FEATURE [App::DocumentObjectGroupPython] C_element051  label="C_element : 028"  # scripted group (container) (typed FeaturePython)
  n = 5
  ref = C_element
FEATURE [App::DocumentObjectGroupPython] H_element044  label="H_element : 023"  # scripted group (container) (typed FeaturePython)
  n = 5
  ref = H_element
FEATURE [App::DocumentObjectGroupPython] N_element020  label="N_element : 009"  # scripted group (container) (typed FeaturePython)
  n = 5
  ref = N_element
FEATURE [App::DocumentObjectGroupPython] O_element048  label="O_element : 024"  # scripted group (container) (typed FeaturePython)
  n = 1
  ref = O_element
FEATURE [App::DocumentObjectGroupPython] G4_GUANINE  # scripted group (container) (typed FeaturePython)
  Dunit = g/cm3
  Dvalue = 2.2
  Group = -> [C_element051,H_element044,N_element020,O_element048]
  conduct = 2
  density = 1
  expand = 3
  formula = G4_GUANINE
  name = G4_GUANINE
  specific = 4
FEATURE [App::DocumentObjectGroupPython] Ca_element012  label="Ca_element : 006"  # scripted group (container) (typed FeaturePython)
  n = 1
  ref = Ca_element
FEATURE [App::DocumentObjectGroupPython] S_element014  label="S_element : 005"  # scripted group (container) (typed FeaturePython)
  n = 1
  ref = S_element
FEATURE [App::DocumentObjectGroupPython] O_element049  label="O_element : 6"  # scripted group (container) (typed FeaturePython)
  n = 6
  ref = O_element
FEATURE [App::DocumentObjectGroupPython] H_element045  label="H_element : 024"  # scripted group (container) (typed FeaturePython)
  n = 4
  ref = H_element
FEATURE [App::DocumentObjectGroupPython] G4_GYPSUM  # scripted group (container) (typed FeaturePython)
  Dunit = g/cm3
  Dvalue = 2.32
  Group = -> [Ca_element012,S_element014,O_element049,H_element045]
  conduct = 2
  density = 1
  expand = 3
  formula = G4_GYPSUM
  name = G4_GYPSUM
  specific = 4
FEATURE [App::DocumentObjectGroupPython] C_element052  label="C_element : 7"  # scripted group (container) (typed FeaturePython)
  n = 7
  ref = C_element
FEATURE [App::DocumentObjectGroupPython] H_element046  label="H_element : 16"  # scripted group (container) (typed FeaturePython)
  n = 16
  ref = H_element
FEATURE [App::DocumentObjectGroupPython] G4_N_HEPTANE  label="G4_N-HEPTANE"  # scripted group (container) (typed FeaturePython)
  Dunit = g/cm3
  Dvalue = 0.68376
  Group = -> [C_element052,H_element046]
  conduct = 2
  density = 1
  expand = 3
  formula = G4_N-HEPTANE
  name = G4_N-HEPTANE
  specific = 4
FEATURE [App::DocumentObjectGroupPython] C_element053  label="C_element : 029"  # scripted group (container) (typed FeaturePython)
  n = 6
  ref = C_element
FEATURE [App::DocumentObjectGroupPython] H_element047  label="H_element : 14"  # scripted group (container) (typed FeaturePython)
  n = 14
  ref = H_element
FEATURE [App::DocumentObjectGroupPython] G4_N_HEXANE  label="G4_N-HEXANE"  # scripted group (container) (typed FeaturePython)
  Dunit = g/cm3
  Dvalue = 0.6603
  Group = -> [C_element053,H_element047]
  conduct = 2
  density = 1
  expand = 3
  formula = G4_N-HEXANE
  name = G4_N-HEXANE
  specific = 4
FEATURE [App::DocumentObjectGroupPython] C_element054  label="C_element : 22"  # scripted group (container) (typed FeaturePython)
  n = 22
  ref = C_element
FEATURE [App::DocumentObjectGroupPython] H_element048  label="H_element : 025"  # scripted group (container) (typed FeaturePython)
  n = 10
  ref = H_element
FEATURE [App::DocumentObjectGroupPython] N_element021  label="N_element : 010"  # scripted group (container) (typed FeaturePython)
  n = 2
  ref = N_element
FEATURE [App::DocumentObjectGroupPython] O_element050  label="O_element : 025"  # scripted group (container) (typed FeaturePython)
  n = 5
  ref = O_element
FEATURE [App::DocumentObjectGroupPython] G4_KAPTON  # scripted group (container) (typed FeaturePython)
  Dunit = g/cm3
  Dvalue = 1.42
  Group = -> [C_element054,H_element048,N_element021,O_element050]
  conduct = 2
  density = 1
  expand = 3
  formula = G4_KAPTON
  name = G4_KAPTON
  specific = 4
FEATURE [App::DocumentObjectGroupPython] La_element001  label="La_element : 1"  # scripted group (container) (typed FeaturePython)
  n = 1
  ref = La_element
FEATURE [App::DocumentObjectGroupPython] Br_element003  label="Br_element : 002"  # scripted group (container) (typed FeaturePython)
  n = 1
  ref = Br_element
FEATURE [App::DocumentObjectGroupPython] O_element051  label="O_element : 026"  # scripted group (container) (typed FeaturePython)
  n = 1
  ref = O_element
FEATURE [App::DocumentObjectGroupPython] G4_LANTHANUM_OXYBROMIDE  # scripted group (container) (typed FeaturePython)
  Dunit = g/cm3
  Dvalue = 6.28
  Group = -> [La_element001,Br_element003,O_element051]
  conduct = 2
  density = 1
  expand = 3
  formula = G4_LANTHANUM_OXYBROMIDE
  name = G4_LANTHANUM_OXYBROMIDE
  specific = 4
FEATURE [App::DocumentObjectGroupPython] La_element002  label="La_element : 2"  # scripted group (container) (typed FeaturePython)
  n = 2
  ref = La_element
FEATURE [App::DocumentObjectGroupPython] O_element052  label="O_element : 027"  # scripted group (container) (typed FeaturePython)
  n = 2
  ref = O_element
FEATURE [App::DocumentObjectGroupPython] S_element015  label="S_element : 006"  # scripted group (container) (typed FeaturePython)
  n = 1
  ref = S_element
FEATURE [App::DocumentObjectGroupPython] G4_LANTHANUM_OXYSULFIDE  # scripted group (container) (typed FeaturePython)
  Dunit = g/cm3
  Dvalue = 5.86
  Group = -> [La_element002,O_element052,S_element015]
  conduct = 2
  density = 1
  expand = 3
  formula = G4_LANTHANUM_OXYSULFIDE
  name = G4_LANTHANUM_OXYSULFIDE
  specific = 4
FEATURE [App::DocumentObjectGroupPython] O_element053  label="O_element : 0.072"  # scripted group (container) (typed FeaturePython)
  n = 0.071682
FEATURE [App::DocumentObjectGroupPython] Pb_element002  label="Pb_element : 0.928"  # scripted group (container) (typed FeaturePython)
  n = 0.928318
FEATURE [App::DocumentObjectGroupPython] G4_LEAD_OXIDE  # scripted group (container) (typed FeaturePython)
  Dunit = g/cm3
  Dvalue = 9.53
  Group = -> [O_element053,Pb_element002]
  conduct = 2
  density = 1
  expand = 3
  formula = G4_LEAD_OXIDE
  name = G4_LEAD_OXIDE
  specific = 4
FEATURE [App::DocumentObjectGroupPython] Li_element001  label="Li_element : 1"  # scripted group (container) (typed FeaturePython)
  n = 1
  ref = Li_element
FEATURE [App::DocumentObjectGroupPython] N_element022  label="N_element : 011"  # scripted group (container) (typed FeaturePython)
  n = 1
  ref = N_element
FEATURE [App::DocumentObjectGroupPython] H_element049  label="H_element : 026"  # scripted group (container) (typed FeaturePython)
  n = 2
  ref = H_element
FEATURE [App::DocumentObjectGroupPython] G4_LITHIUM_AMIDE  # scripted group (container) (typed FeaturePython)
  Dunit = g/cm3
  Dvalue = 1.178
  Group = -> [Li_element001,N_element022,H_element049]
  conduct = 2
  density = 1
  expand = 3
  formula = G4_LITHIUM_AMIDE
  name = G4_LITHIUM_AMIDE
  specific = 4
FEATURE [App::DocumentObjectGroupPython] Li_element002  label="Li_element : 2"  # scripted group (container) (typed FeaturePython)
  n = 2
  ref = Li_element
FEATURE [App::DocumentObjectGroupPython] C_element055  label="C_element : 030"  # scripted group (container) (typed FeaturePython)
  n = 1
  ref = C_element
FEATURE [App::DocumentObjectGroupPython] O_element054  label="O_element : 028"  # scripted group (container) (typed FeaturePython)
  n = 3
  ref = O_element
FEATURE [App::DocumentObjectGroupPython] G4_LITHIUM_CARBONATE  # scripted group (container) (typed FeaturePython)
  Dunit = g/cm3
  Dvalue = 2.11
  Group = -> [Li_element002,C_element055,O_element054]
  conduct = 2
  density = 1
  expand = 3
  formula = G4_LITHIUM_CARBONATE
  name = G4_LITHIUM_CARBONATE
  specific = 4
FEATURE [App::DocumentObjectGroupPython] Li_element003  label="Li_element : 003"  # scripted group (container) (typed FeaturePython)
  n = 1
  ref = Li_element
FEATURE [App::DocumentObjectGroupPython] F_element012  label="F_element : 004"  # scripted group (container) (typed FeaturePython)
  n = 1
  ref = F_element
FEATURE [App::DocumentObjectGroupPython] G4_LITHIUM_FLUORIDE  # scripted group (container) (typed FeaturePython)
  Dunit = g/cm3
  Dvalue = 2.635
  Group = -> [Li_element003,F_element012]
  conduct = 2
  density = 1
  expand = 3
  formula = G4_LITHIUM_FLUORIDE
  name = G4_LITHIUM_FLUORIDE
  specific = 4
FEATURE [App::DocumentObjectGroupPython] Li_element004  label="Li_element : 004"  # scripted group (container) (typed FeaturePython)
  n = 1
  ref = Li_element
FEATURE [App::DocumentObjectGroupPython] H_element050  label="H_element : 027"  # scripted group (container) (typed FeaturePython)
  n = 1
  ref = H_element
FEATURE [App::DocumentObjectGroupPython] G4_LITHIUM_HYDRIDE  # scripted group (container) (typed FeaturePython)
  Dunit = g/cm3
  Dvalue = 0.82
  Group = -> [Li_element004,H_element050]
  conduct = 2
  density = 1
  expand = 3
  formula = G4_LITHIUM_HYDRIDE
  name = G4_LITHIUM_HYDRIDE
  specific = 4
FEATURE [App::DocumentObjectGroupPython] Li_element005  label="Li_element : 005"  # scripted group (container) (typed FeaturePython)
  n = 1
  ref = Li_element
FEATURE [App::DocumentObjectGroupPython] I_element003  label="I_element : 002"  # scripted group (container) (typed FeaturePython)
  n = 1
  ref = I_element
FEATURE [App::DocumentObjectGroupPython] G4_LITHIUM_IODIDE  # scripted group (container) (typed FeaturePython)
  Dunit = g/cm3
  Dvalue = 3.494
  Group = -> [Li_element005,I_element003]
  conduct = 2
  density = 1
  expand = 3
  formula = G4_LITHIUM_IODIDE
  name = G4_LITHIUM_IODIDE
  specific = 4
FEATURE [App::DocumentObjectGroupPython] Li_element006  label="Li_element : 006"  # scripted group (container) (typed FeaturePython)
  n = 2
  ref = Li_element
FEATURE [App::DocumentObjectGroupPython] O_element055  label="O_element : 029"  # scripted group (container) (typed FeaturePython)
  n = 1
  ref = O_element
FEATURE [App::DocumentObjectGroupPython] G4_LITHIUM_OXIDE  # scripted group (container) (typed FeaturePython)
  Dunit = g/cm3
  Dvalue = 2.013
  Group = -> [Li_element006,O_element055]
  conduct = 2
  density = 1
  expand = 3
  formula = G4_LITHIUM_OXIDE
  name = G4_LITHIUM_OXIDE
  specific = 4
FEATURE [App::DocumentObjectGroupPython] Li_element007  label="Li_element : 007"  # scripted group (container) (typed FeaturePython)
  n = 2
  ref = Li_element
FEATURE [App::DocumentObjectGroupPython] B_element005  label="B_element : 005"  # scripted group (container) (typed FeaturePython)
  n = 4
  ref = B_element
FEATURE [App::DocumentObjectGroupPython] O_element056  label="O_element : 7"  # scripted group (container) (typed FeaturePython)
  n = 7
  ref = O_element
FEATURE [App::DocumentObjectGroupPython] G4_LITHIUM_TETRABORATE  # scripted group (container) (typed FeaturePython)
  Dunit = g/cm3
  Dvalue = 2.44
  Group = -> [Li_element007,B_element005,O_element056]
  conduct = 2
  density = 1
  expand = 3
  formula = G4_LITHIUM_TETRABORATE
  name = G4_LITHIUM_TETRABORATE
  specific = 4
FEATURE [App::DocumentObjectGroupPython] H_element051  label="H_element : 0.105"  # scripted group (container) (typed FeaturePython)
  n = 0.105
FEATURE [App::DocumentObjectGroupPython] C_element056  label="C_element : 0.083"  # scripted group (container) (typed FeaturePython)
  n = 0.083
FEATURE [App::DocumentObjectGroupPython] N_element023  label="N_element : 0.023"  # scripted group (container) (typed FeaturePython)
  n = 0.023
FEATURE [App::DocumentObjectGroupPython] O_element057  label="O_element : 0.779"  # scripted group (container) (typed FeaturePython)
  n = 0.779
FEATURE [App::DocumentObjectGroupPython] Na_element010  label="Na_element : 0.097"  # scripted group (container) (typed FeaturePython)
  n = 0.002
FEATURE [App::DocumentObjectGroupPython] P_element006  label="P_element : 0.105"  # scripted group (container) (typed FeaturePython)
  n = 0.001
FEATURE [App::DocumentObjectGroupPython] S_element016  label="S_element : 0.017"  # scripted group (container) (typed FeaturePython)
  n = 0.002
FEATURE [App::DocumentObjectGroupPython] Cl_element014  label="Cl_element : 0.587"  # scripted group (container) (typed FeaturePython)
  n = 0.003
FEATURE [App::DocumentObjectGroupPython] K_element005  label="K_element : 0.015"  # scripted group (container) (typed FeaturePython)
  n = 0.002
FEATURE [App::DocumentObjectGroupPython] G4_LUNG_ICRP  # scripted group (container) (typed FeaturePython)
  Dunit = g/cm3
  Dvalue = 1.04
  Group = -> [H_element051,C_element056,N_element023,O_element057,Na_element010,P_element006,S_element016,Cl_element014,K_element005]
  conduct = 2
  density = 1
  expand = 3
  formula = G4_LUNG_ICRP
  name = G4_LUNG_ICRP
  specific = 4
FEATURE [App::DocumentObjectGroupPython] H_element052  label="H_element : 0.116"  # scripted group (container) (typed FeaturePython)
  n = 0.114318
FEATURE [App::DocumentObjectGroupPython] C_element057  label="C_element : 0.656"  # scripted group (container) (typed FeaturePython)
  n = 0.655824
FEATURE [App::DocumentObjectGroupPython] O_element058  label="O_element : 0.092"  # scripted group (container) (typed FeaturePython)
  n = 0.0921831
FEATURE [App::DocumentObjectGroupPython] Mg_element004  label="Mg_element : 0.135"  # scripted group (container) (typed FeaturePython)
  n = 0.134792
FEATURE [App::DocumentObjectGroupPython] Ca_element013  label="Ca_element : 0.003"  # scripted group (container) (typed FeaturePython)
  n = 0.002883
FEATURE [App::DocumentObjectGroupPython] G4_M3_WAX  # scripted group (container) (typed FeaturePython)
  Dunit = g/cm3
  Dvalue = 1.05
  Group = -> [H_element052,C_element057,O_element058,Mg_element004,Ca_element013]
  conduct = 2
  density = 1
  expand = 3
  formula = G4_M3_WAX
  name = G4_M3_WAX
  specific = 4
FEATURE [App::DocumentObjectGroupPython] Mg_element005  label="Mg_element : 1"  # scripted group (container) (typed FeaturePython)
  n = 1
  ref = Mg_element
FEATURE [App::DocumentObjectGroupPython] C_element058  label="C_element : 031"  # scripted group (container) (typed FeaturePython)
  n = 1
  ref = C_element
FEATURE [App::DocumentObjectGroupPython] O_element059  label="O_element : 030"  # scripted group (container) (typed FeaturePython)
  n = 3
  ref = O_element
FEATURE [App::DocumentObjectGroupPython] G4_MAGNESIUM_CARBONATE  # scripted group (container) (typed FeaturePython)
  Dunit = g/cm3
  Dvalue = 2.958
  Group = -> [Mg_element005,C_element058,O_element059]
  conduct = 2
  density = 1
  expand = 3
  formula = G4_MAGNESIUM_CARBONATE
  name = G4_MAGNESIUM_CARBONATE
  specific = 4
FEATURE [App::DocumentObjectGroupPython] Mg_element006  label="Mg_element : 002"  # scripted group (container) (typed FeaturePython)
  n = 1
  ref = Mg_element
FEATURE [App::DocumentObjectGroupPython] F_element013  label="F_element : 005"  # scripted group (container) (typed FeaturePython)
  n = 2
  ref = F_element
FEATURE [App::DocumentObjectGroupPython] G4_MAGNESIUM_FLUORIDE  # scripted group (container) (typed FeaturePython)
  Dunit = g/cm3
  Dvalue = 3
  Group = -> [Mg_element006,F_element013]
  conduct = 2
  density = 1
  expand = 3
  formula = G4_MAGNESIUM_FLUORIDE
  name = G4_MAGNESIUM_FLUORIDE
  specific = 4
FEATURE [App::DocumentObjectGroupPython] Mg_element007  label="Mg_element : 003"  # scripted group (container) (typed FeaturePython)
  n = 1
  ref = Mg_element
FEATURE [App::DocumentObjectGroupPython] O_element060  label="O_element : 031"  # scripted group (container) (typed FeaturePython)
  n = 1
  ref = O_element
FEATURE [App::DocumentObjectGroupPython] G4_MAGNESIUM_OXIDE  # scripted group (container) (typed FeaturePython)
  Dunit = g/cm3
  Dvalue = 3.58
  Group = -> [Mg_element007,O_element060]
  conduct = 2
  density = 1
  expand = 3
  formula = G4_MAGNESIUM_OXIDE
  name = G4_MAGNESIUM_OXIDE
  specific = 4
FEATURE [App::DocumentObjectGroupPython] Mg_element008  label="Mg_element : 004"  # scripted group (container) (typed FeaturePython)
  n = 1
  ref = Mg_element
FEATURE [App::DocumentObjectGroupPython] B_element006  label="B_element : 006"  # scripted group (container) (typed FeaturePython)
  n = 4
  ref = B_element
FEATURE [App::DocumentObjectGroupPython] O_element061  label="O_element : 032"  # scripted group (container) (typed FeaturePython)
  n = 7
  ref = O_element
FEATURE [App::DocumentObjectGroupPython] G4_MAGNESIUM_TETRABORATE  # scripted group (container) (typed FeaturePython)
  Dunit = g/cm3
  Dvalue = 2.53
  Group = -> [Mg_element008,B_element006,O_element061]
  conduct = 2
  density = 1
  expand = 3
  formula = G4_MAGNESIUM_TETRABORATE
  name = G4_MAGNESIUM_TETRABORATE
  specific = 4
FEATURE [App::DocumentObjectGroupPython] Hg_element001  label="Hg_element : 1"  # scripted group (container) (typed FeaturePython)
  n = 1
  ref = Hg_element
FEATURE [App::DocumentObjectGroupPython] I_element004  label="I_element : 2"  # scripted group (container) (typed FeaturePython)
  n = 2
  ref = I_element
FEATURE [App::DocumentObjectGroupPython] G4_MERCURIC_IODIDE  # scripted group (container) (typed FeaturePython)
  Dunit = g/cm3
  Dvalue = 6.36
  Group = -> [Hg_element001,I_element004]
  conduct = 2
  density = 1
  expand = 3
  formula = G4_MERCURIC_IODIDE
  name = G4_MERCURIC_IODIDE
  specific = 4
FEATURE [App::DocumentObjectGroupPython] C_element059  label="C_element : 032"  # scripted group (container) (typed FeaturePython)
  n = 1
  ref = C_element
FEATURE [App::DocumentObjectGroupPython] H_element053  label="H_element : 028"  # scripted group (container) (typed FeaturePython)
  n = 4
  ref = H_element
FEATURE [App::DocumentObjectGroupPython] G4_METHANE  # scripted group (container) (typed FeaturePython)
  Dunit = g/cm3
  Dvalue = 0.000667151
  Group = -> [C_element059,H_element053]
  conduct = 2
  density = 1
  expand = 3
  formula = G4_METHANE
  name = G4_METHANE
  specific = 4
FEATURE [App::DocumentObjectGroupPython] C_element060  label="C_element : 033"  # scripted group (container) (typed FeaturePython)
  n = 1
  ref = C_element
FEATURE [App::DocumentObjectGroupPython] H_element054  label="H_element : 029"  # scripted group (container) (typed FeaturePython)
  n = 4
  ref = H_element
FEATURE [App::DocumentObjectGroupPython] O_element062  label="O_element : 033"  # scripted group (container) (typed FeaturePython)
  n = 1
  ref = O_element
FEATURE [App::DocumentObjectGroupPython] G4_METHANOL  # scripted group (container) (typed FeaturePython)
  Dunit = g/cm3
  Dvalue = 0.7914
  Group = -> [C_element060,H_element054,O_element062]
  conduct = 2
  density = 1
  expand = 3
  formula = G4_METHANOL
  name = G4_METHANOL
  specific = 4
FEATURE [App::DocumentObjectGroupPython] H_element055  label="H_element : 0.134"  # scripted group (container) (typed FeaturePython)
  n = 0.13404
FEATURE [App::DocumentObjectGroupPython] C_element061  label="C_element : 0.778"  # scripted group (container) (typed FeaturePython)
  n = 0.77796
FEATURE [App::DocumentObjectGroupPython] O_element063  label="O_element : 0.035"  # scripted group (container) (typed FeaturePython)
  n = 0.03502
FEATURE [App::DocumentObjectGroupPython] Mg_element009  label="Mg_element : 0.039"  # scripted group (container) (typed FeaturePython)
  n = 0.038594
FEATURE [App::DocumentObjectGroupPython] Ti_element002  label="Ti_element : 0.014"  # scripted group (container) (typed FeaturePython)
  n = 0.014386
FEATURE [App::DocumentObjectGroupPython] G4_MIX_D_WAX  # scripted group (container) (typed FeaturePython)
  Dunit = g/cm3
  Dvalue = 0.99
  Group = -> [H_element055,C_element061,O_element063,Mg_element009,Ti_element002]
  conduct = 2
  density = 1
  expand = 3
  formula = G4_MIX_D_WAX
  name = G4_MIX_D_WAX
  specific = 4
FEATURE [App::DocumentObjectGroupPython] H_element056  label="H_element : 0.135"  # scripted group (container) (typed FeaturePython)
  n = 0.081192
FEATURE [App::DocumentObjectGroupPython] C_element062  label="C_element : 0.583"  # scripted group (container) (typed FeaturePython)
  n = 0.583442
FEATURE [App::DocumentObjectGroupPython] N_element024  label="N_element : 0.018"  # scripted group (container) (typed FeaturePython)
  n = 0.017798
FEATURE [App::DocumentObjectGroupPython] O_element064  label="O_element : 0.186"  # scripted group (container) (typed FeaturePython)
  n = 0.186381
FEATURE [App::DocumentObjectGroupPython] Mg_element010  label="Mg_element : 0.130"  # scripted group (container) (typed FeaturePython)
  n = 0.130287
FEATURE [App::DocumentObjectGroupPython] Cl_element015  label="Cl_element : 0.588"  # scripted group (container) (typed FeaturePython)
  n = 0.0009
FEATURE [App::DocumentObjectGroupPython] G4_MS20_TISSUE  # scripted group (container) (typed FeaturePython)
  Dunit = g/cm3
  Dvalue = 1
  Group = -> [H_element056,C_element062,N_element024,O_element064,Mg_element010,Cl_element015]
  conduct = 2
  density = 1
  expand = 3
  formula = G4_MS20_TISSUE
  name = G4_MS20_TISSUE
  specific = 4
FEATURE [App::DocumentObjectGroupPython] H_element057  label="H_element : 0.136"  # scripted group (container) (typed FeaturePython)
  n = 0.102
FEATURE [App::DocumentObjectGroupPython] C_element063  label="C_element : 0.143"  # scripted group (container) (typed FeaturePython)
  n = 0.143
FEATURE [App::DocumentObjectGroupPython] N_element025  label="N_element : 0.034"  # scripted group (container) (typed FeaturePython)
  n = 0.034
FEATURE [App::DocumentObjectGroupPython] O_element065  label="O_element : 0.710"  # scripted group (container) (typed FeaturePython)
  n = 0.71
FEATURE [App::DocumentObjectGroupPython] Na_element011  label="Na_element : 0.098"  # scripted group (container) (typed FeaturePython)
  n = 0.001
FEATURE [App::DocumentObjectGroupPython] P_element007  label="P_element : 0.002"  # scripted group (container) (typed FeaturePython)
  n = 0.002
FEATURE [App::DocumentObjectGroupPython] S_element017  label="S_element : 0.018"  # scripted group (container) (typed FeaturePython)
  n = 0.003
FEATURE [App::DocumentObjectGroupPython] Cl_element016  label="Cl_element : 0.589"  # scripted group (container) (typed FeaturePython)
  n = 0.001
FEATURE [App::DocumentObjectGroupPython] K_element006  label="K_element : 0.004"  # scripted group (container) (typed FeaturePython)
  n = 0.004
FEATURE [App::DocumentObjectGroupPython] G4_MUSCLE_SKELETAL_ICRP  # scripted group (container) (typed FeaturePython)
  Dunit = g/cm3
  Dvalue = 1.05
  Group = -> [H_element057,C_element063,N_element025,O_element065,Na_element011,P_element007,S_element017,Cl_element016,K_element006]
  conduct = 2
  density = 1
  expand = 3
  formula = G4_MUSCLE_SKELETAL_ICRP
  name = G4_MUSCLE_SKELETAL_ICRP
  specific = 4
FEATURE [App::DocumentObjectGroupPython] H_element058  label="H_element : 0.137"  # scripted group (container) (typed FeaturePython)
  n = 0.102102
FEATURE [App::DocumentObjectGroupPython] C_element064  label="C_element : 0.123"  # scripted group (container) (typed FeaturePython)
  n = 0.123123
FEATURE [App::DocumentObjectGroupPython] N_element026  label="N_element : 0.756"  # scripted group (container) (typed FeaturePython)
  n = 0.035035
FEATURE [App::DocumentObjectGroupPython] O_element066  label="O_element : 0.730"  # scripted group (container) (typed FeaturePython)
  n = 0.72973
FEATURE [App::DocumentObjectGroupPython] Na_element012  label="Na_element : 0.099"  # scripted group (container) (typed FeaturePython)
  n = 0.001001
FEATURE [App::DocumentObjectGroupPython] P_element008  label="P_element : 0.106"  # scripted group (container) (typed FeaturePython)
  n = 0.002002
FEATURE [App::DocumentObjectGroupPython] S_element018  label="S_element : 0.019"  # scripted group (container) (typed FeaturePython)
  n = 0.004004
FEATURE [App::DocumentObjectGroupPython] K_element007  label="K_element : 0.016"  # scripted group (container) (typed FeaturePython)
  n = 0.003003
FEATURE [App::DocumentObjectGroupPython] G4_MUSCLE_STRIATED_ICRU  # scripted group (container) (typed FeaturePython)
  Dunit = g/cm3
  Dvalue = 1.04
  Group = -> [H_element058,C_element064,N_element026,O_element066,Na_element012,P_element008,S_element018,K_element007]
  conduct = 2
  density = 1
  expand = 3
  formula = G4_MUSCLE_STRIATED_ICRU
  name = G4_MUSCLE_STRIATED_ICRU
  specific = 4
FEATURE [App::DocumentObjectGroupPython] H_element059  label="H_element : 0.098"  # scripted group (container) (typed FeaturePython)
  n = 0.0982341
FEATURE [App::DocumentObjectGroupPython] C_element065  label="C_element : 0.156"  # scripted group (container) (typed FeaturePython)
  n = 0.156214
FEATURE [App::DocumentObjectGroupPython] N_element027  label="N_element : 0.757"  # scripted group (container) (typed FeaturePython)
  n = 0.035451
FEATURE [App::DocumentObjectGroupPython] O_element067  label="O_element : 0.880"  # scripted group (container) (typed FeaturePython)
  n = 0.710101
FEATURE [App::DocumentObjectGroupPython] G4_MUSCLE_WITH_SUCROSE  # scripted group (container) (typed FeaturePython)
  Dunit = g/cm3
  Dvalue = 1.11
  Group = -> [H_element059,C_element065,N_element027,O_element067]
  conduct = 2
  density = 1
  expand = 3
  formula = G4_MUSCLE_WITH_SUCROSE
  name = G4_MUSCLE_WITH_SUCROSE
  specific = 4
FEATURE [App::DocumentObjectGroupPython] H_element060  label="H_element : 0.138"  # scripted group (container) (typed FeaturePython)
  n = 0.101969
FEATURE [App::DocumentObjectGroupPython] C_element066  label="C_element : 0.120"  # scripted group (container) (typed FeaturePython)
  n = 0.120058
FEATURE [App::DocumentObjectGroupPython] N_element028  label="N_element : 0.758"  # scripted group (container) (typed FeaturePython)
  n = 0.035451
FEATURE [App::DocumentObjectGroupPython] O_element068  label="O_element : 0.743"  # scripted group (container) (typed FeaturePython)
  n = 0.742522
FEATURE [App::DocumentObjectGroupPython] G4_MUSCLE_WITHOUT_SUCROSE  # scripted group (container) (typed FeaturePython)
  Dunit = g/cm3
  Dvalue = 1.07
  Group = -> [H_element060,C_element066,N_element028,O_element068]
  conduct = 2
  density = 1
  expand = 3
  formula = G4_MUSCLE_WITHOUT_SUCROSE
  name = G4_MUSCLE_WITHOUT_SUCROSE
  specific = 4
FEATURE [App::DocumentObjectGroupPython] C_element067  label="C_element : 10"  # scripted group (container) (typed FeaturePython)
  n = 10
  ref = C_element
FEATURE [App::DocumentObjectGroupPython] H_element061  label="H_element : 030"  # scripted group (container) (typed FeaturePython)
  n = 8
  ref = H_element
FEATURE [App::DocumentObjectGroupPython] G4_NAPHTHALENE  # scripted group (container) (typed FeaturePython)
  Dunit = g/cm3
  Dvalue = 1.145
  Group = -> [C_element067,H_element061]
  conduct = 2
  density = 1
  expand = 3
  formula = G4_NAPHTHALENE
  name = G4_NAPHTHALENE
  specific = 4
FEATURE [App::DocumentObjectGroupPython] C_element068  label="C_element : 034"  # scripted group (container) (typed FeaturePython)
  n = 6
  ref = C_element
FEATURE [App::DocumentObjectGroupPython] H_element062  label="H_element : 031"  # scripted group (container) (typed FeaturePython)
  n = 5
  ref = H_element
FEATURE [App::DocumentObjectGroupPython] N_element029  label="N_element : 012"  # scripted group (container) (typed FeaturePython)
  n = 1
  ref = N_element
FEATURE [App::DocumentObjectGroupPython] O_element069  label="O_element : 034"  # scripted group (container) (typed FeaturePython)
  n = 2
  ref = O_element
FEATURE [App::DocumentObjectGroupPython] G4_NITROBENZENE  # scripted group (container) (typed FeaturePython)
  Dunit = g/cm3
  Dvalue = 1.19867
  Group = -> [C_element068,H_element062,N_element029,O_element069]
  conduct = 2
  density = 1
  expand = 3
  formula = G4_NITROBENZENE
  name = G4_NITROBENZENE
  specific = 4
FEATURE [App::DocumentObjectGroupPython] N_element030  label="N_element : 013"  # scripted group (container) (typed FeaturePython)
  n = 2
  ref = N_element
FEATURE [App::DocumentObjectGroupPython] O_element070  label="O_element : 035"  # scripted group (container) (typed FeaturePython)
  n = 1
  ref = O_element
FEATURE [App::DocumentObjectGroupPython] G4_NITROUS_OXIDE  # scripted group (container) (typed FeaturePython)
  Dunit = g/cm3
  Dvalue = 0.00183094
  Group = -> [N_element030,O_element070]
  conduct = 2
  density = 1
  expand = 3
  formula = G4_NITROUS_OXIDE
  name = G4_NITROUS_OXIDE
  specific = 4
FEATURE [App::DocumentObjectGroupPython] H_element063  label="H_element : 0.104"  # scripted group (container) (typed FeaturePython)
  n = 0.103509
FEATURE [App::DocumentObjectGroupPython] C_element069  label="C_element : 0.648"  # scripted group (container) (typed FeaturePython)
  n = 0.648416
FEATURE [App::DocumentObjectGroupPython] N_element031  label="N_element : 0.100"  # scripted group (container) (typed FeaturePython)
  n = 0.0995361
FEATURE [App::DocumentObjectGroupPython] O_element071  label="O_element : 0.149"  # scripted group (container) (typed FeaturePython)
  n = 0.148539
FEATURE [App::DocumentObjectGroupPython] G4_NYLON_8062  label="G4_NYLON-8062"  # scripted group (container) (typed FeaturePython)
  Dunit = g/cm3
  Dvalue = 1.08
  Group = -> [H_element063,C_element069,N_element031,O_element071]
  conduct = 2
  density = 1
  expand = 3
  formula = G4_NYLON-8062
  name = G4_NYLON-8062
  specific = 4
FEATURE [App::DocumentObjectGroupPython] C_element070  label="C_element : 035"  # scripted group (container) (typed FeaturePython)
  n = 6
  ref = C_element
FEATURE [App::DocumentObjectGroupPython] H_element064  label="H_element : 11"  # scripted group (container) (typed FeaturePython)
  n = 11
  ref = H_element
FEATURE [App::DocumentObjectGroupPython] N_element032  label="N_element : 014"  # scripted group (container) (typed FeaturePython)
  n = 1
  ref = N_element
FEATURE [App::DocumentObjectGroupPython] O_element072  label="O_element : 036"  # scripted group (container) (typed FeaturePython)
  n = 1
  ref = O_element
FEATURE [App::DocumentObjectGroupPython] G4_NYLON_6_6  label="G4_NYLON-6-6"  # scripted group (container) (typed FeaturePython)
  Dunit = g/cm3
  Dvalue = 1.14
  Group = -> [C_element070,H_element064,N_element032,O_element072]
  conduct = 2
  density = 1
  expand = 3
  formula = G4_NYLON-6-6
  name = G4_NYLON-6-6
  specific = 4
FEATURE [App::DocumentObjectGroupPython] H_element065  label="H_element : 0.139"  # scripted group (container) (typed FeaturePython)
  n = 0.107062
FEATURE [App::DocumentObjectGroupPython] C_element071  label="C_element : 0.680"  # scripted group (container) (typed FeaturePython)
  n = 0.680449
FEATURE [App::DocumentObjectGroupPython] N_element033  label="N_element : 0.099"  # scripted group (container) (typed FeaturePython)
  n = 0.099189
FEATURE [App::DocumentObjectGroupPython] O_element073  label="O_element : 0.113"  # scripted group (container) (typed FeaturePython)
  n = 0.1133
FEATURE [App::DocumentObjectGroupPython] G4_NYLON_6_10  label="G4_NYLON-6-10"  # scripted group (container) (typed FeaturePython)
  Dunit = g/cm3
  Dvalue = 1.14
  Group = -> [H_element065,C_element071,N_element033,O_element073]
  conduct = 2
  density = 1
  expand = 3
  formula = G4_NYLON-6-10
  name = G4_NYLON-6-10
  specific = 4
FEATURE [App::DocumentObjectGroupPython] H_element066  label="H_element : 0.140"  # scripted group (container) (typed FeaturePython)
  n = 0.115476
FEATURE [App::DocumentObjectGroupPython] C_element072  label="C_element : 0.721"  # scripted group (container) (typed FeaturePython)
  n = 0.720818
FEATURE [App::DocumentObjectGroupPython] N_element034  label="N_element : 0.076"  # scripted group (container) (typed FeaturePython)
  n = 0.0764169
FEATURE [App::DocumentObjectGroupPython] O_element074  label="O_element : 0.087"  # scripted group (container) (typed FeaturePython)
  n = 0.0872889
FEATURE [App::DocumentObjectGroupPython] G4_NYLON_11_RILSAN  label="G4_NYLON-11_RILSAN"  # scripted group (container) (typed FeaturePython)
  Dunit = g/cm3
  Dvalue = 1.425
  Group = -> [H_element066,C_element072,N_element034,O_element074]
  conduct = 2
  density = 1
  expand = 3
  formula = G4_NYLON-11_RILSAN
  name = G4_NYLON-11_RILSAN
  specific = 4
FEATURE [App::DocumentObjectGroupPython] C_element073  label="C_element : 8"  # scripted group (container) (typed FeaturePython)
  n = 8
  ref = C_element
FEATURE [App::DocumentObjectGroupPython] H_element067  label="H_element : 18"  # scripted group (container) (typed FeaturePython)
  n = 18
  ref = H_element
FEATURE [App::DocumentObjectGroupPython] G4_OCTANE  # scripted group (container) (typed FeaturePython)
  Dunit = g/cm3
  Dvalue = 0.7026
  Group = -> [C_element073,H_element067]
  conduct = 2
  density = 1
  expand = 3
  formula = G4_OCTANE
  name = G4_OCTANE
  specific = 4
FEATURE [App::DocumentObjectGroupPython] C_element074  label="C_element : 25"  # scripted group (container) (typed FeaturePython)
  n = 25
  ref = C_element
FEATURE [App::DocumentObjectGroupPython] H_element068  label="H_element : 52"  # scripted group (container) (typed FeaturePython)
  n = 52
  ref = H_element
FEATURE [App::DocumentObjectGroupPython] G4_PARAFFIN  # scripted group (container) (typed FeaturePython)
  Dunit = g/cm3
  Dvalue = 0.93
  Group = -> [C_element074,H_element068]
  conduct = 2
  density = 1
  expand = 3
  formula = G4_PARAFFIN
  name = G4_PARAFFIN
  specific = 4
FEATURE [App::DocumentObjectGroupPython] C_element075  label="C_element : 036"  # scripted group (container) (typed FeaturePython)
  n = 5
  ref = C_element
FEATURE [App::DocumentObjectGroupPython] H_element069  label="H_element : 032"  # scripted group (container) (typed FeaturePython)
  n = 12
  ref = H_element
FEATURE [App::DocumentObjectGroupPython] G4_N_PENTANE  label="G4_N-PENTANE"  # scripted group (container) (typed FeaturePython)
  Dunit = g/cm3
  Dvalue = 0.6262
  Group = -> [C_element075,H_element069]
  conduct = 2
  density = 1
  expand = 3
  formula = G4_N-PENTANE
  name = G4_N-PENTANE
  specific = 4
FEATURE [App::DocumentObjectGroupPython] H_element070  label="H_element : 0.014"  # scripted group (container) (typed FeaturePython)
  n = 0.0141
FEATURE [App::DocumentObjectGroupPython] C_element076  label="C_element : 0.072"  # scripted group (container) (typed FeaturePython)
  n = 0.072261
FEATURE [App::DocumentObjectGroupPython] N_element035  label="N_element : 0.019"  # scripted group (container) (typed FeaturePython)
  n = 0.01932
FEATURE [App::DocumentObjectGroupPython] O_element075  label="O_element : 0.066"  # scripted group (container) (typed FeaturePython)
  n = 0.066101
FEATURE [App::DocumentObjectGroupPython] S_element019  label="S_element : 0.020"  # scripted group (container) (typed FeaturePython)
  n = 0.00189
FEATURE [App::DocumentObjectGroupPython] Br_element004  label="Br_element : 0.349"  # scripted group (container) (typed FeaturePython)
  n = 0.349103
FEATURE [App::DocumentObjectGroupPython] Ag_element001  label="Ag_element : 0.474"  # scripted group (container) (typed FeaturePython)
  n = 0.474105
FEATURE [App::DocumentObjectGroupPython] I_element005  label="I_element : 0.003"  # scripted group (container) (typed FeaturePython)
  n = 0.00312
FEATURE [App::DocumentObjectGroupPython] G4_PHOTO_EMULSION  # scripted group (container) (typed FeaturePython)
  Dunit = g/cm3
  Dvalue = 3.815
  Group = -> [H_element070,C_element076,N_element035,O_element075,S_element019,Br_element004,Ag_element001,I_element005]
  conduct = 2
  density = 1
  expand = 3
  formula = G4_PHOTO_EMULSION
  name = G4_PHOTO_EMULSION
  specific = 4
FEATURE [App::DocumentObjectGroupPython] C_element077  label="C_element : 9"  # scripted group (container) (typed FeaturePython)
  n = 9
  ref = C_element
FEATURE [App::DocumentObjectGroupPython] H_element071  label="H_element : 033"  # scripted group (container) (typed FeaturePython)
  n = 10
  ref = H_element
FEATURE [App::DocumentObjectGroupPython] G4_PLASTIC_SC_VINYLTOLUENE  # scripted group (container) (typed FeaturePython)
  Dunit = g/cm3
  Dvalue = 1.032
  Group = -> [C_element077,H_element071]
  conduct = 2
  density = 1
  expand = 3
  formula = G4_PLASTIC_SC_VINYLTOLUENE
  name = G4_PLASTIC_SC_VINYLTOLUENE
  specific = 4
FEATURE [App::DocumentObjectGroupPython] Pu_element001  label="Pu_element : 1"  # scripted group (container) (typed FeaturePython)
  n = 1
  ref = Pu_element
FEATURE [App::DocumentObjectGroupPython] O_element076  label="O_element : 037"  # scripted group (container) (typed FeaturePython)
  n = 2
  ref = O_element
FEATURE [App::DocumentObjectGroupPython] G4_PLUTONIUM_DIOXIDE  # scripted group (container) (typed FeaturePython)
  Dunit = g/cm3
  Dvalue = 11.46
  Group = -> [Pu_element001,O_element076]
  conduct = 2
  density = 1
  expand = 3
  formula = G4_PLUTONIUM_DIOXIDE
  name = G4_PLUTONIUM_DIOXIDE
  specific = 4
FEATURE [App::DocumentObjectGroupPython] C_element078  label="C_element : 037"  # scripted group (container) (typed FeaturePython)
  n = 3
  ref = C_element
FEATURE [App::DocumentObjectGroupPython] H_element072  label="H_element : 034"  # scripted group (container) (typed FeaturePython)
  n = 3
  ref = H_element
FEATURE [App::DocumentObjectGroupPython] N_element036  label="N_element : 015"  # scripted group (container) (typed FeaturePython)
  n = 1
  ref = N_element
FEATURE [App::DocumentObjectGroupPython] G4_POLYACRYLONITRILE  # scripted group (container) (typed FeaturePython)
  Dunit = g/cm3
  Dvalue = 1.17
  Group = -> [C_element078,H_element072,N_element036]
  conduct = 2
  density = 1
  expand = 3
  formula = G4_POLYACRYLONITRILE
  name = G4_POLYACRYLONITRILE
  specific = 4
FEATURE [App::DocumentObjectGroupPython] C_element079  label="C_element : 16"  # scripted group (container) (typed FeaturePython)
  n = 16
  ref = C_element
FEATURE [App::DocumentObjectGroupPython] H_element073  label="H_element : 035"  # scripted group (container) (typed FeaturePython)
  n = 14
  ref = H_element
FEATURE [App::DocumentObjectGroupPython] O_element077  label="O_element : 038"  # scripted group (container) (typed FeaturePython)
  n = 3
  ref = O_element
FEATURE [App::DocumentObjectGroupPython] G4_POLYCARBONATE  # scripted group (container) (typed FeaturePython)
  Dunit = g/cm3
  Dvalue = 1.2
  Group = -> [C_element079,H_element073,O_element077]
  conduct = 2
  density = 1
  expand = 3
  formula = G4_POLYCARBONATE
  name = G4_POLYCARBONATE
  specific = 4
FEATURE [App::DocumentObjectGroupPython] C_element080  label="C_element : 038"  # scripted group (container) (typed FeaturePython)
  n = 8
  ref = C_element
FEATURE [App::DocumentObjectGroupPython] H_element074  label="H_element : 036"  # scripted group (container) (typed FeaturePython)
  n = 7
  ref = H_element
FEATURE [App::DocumentObjectGroupPython] Cl_element017  label="Cl_element : 007"  # scripted group (container) (typed FeaturePython)
  n = 1
  ref = Cl_element
FEATURE [App::DocumentObjectGroupPython] G4_POLYCHLOROSTYRENE  # scripted group (container) (typed FeaturePython)
  Dunit = g/cm3
  Dvalue = 1.3
  Group = -> [C_element080,H_element074,Cl_element017]
  conduct = 2
  density = 1
  expand = 3
  formula = G4_POLYCHLOROSTYRENE
  name = G4_POLYCHLOROSTYRENE
  specific = 4
FEATURE [App::DocumentObjectGroupPython] C_element081  label="C_element : 039"  # scripted group (container) (typed FeaturePython)
  n = 1
  ref = C_element
FEATURE [App::DocumentObjectGroupPython] H_element075  label="H_element : 037"  # scripted group (container) (typed FeaturePython)
  n = 2
  ref = H_element
FEATURE [App::DocumentObjectGroupPython] G4_POLYETHYLENE  # scripted group (container) (typed FeaturePython)
  Dunit = g/cm3
  Dvalue = 0.94
  Group = -> [C_element081,H_element075]
  conduct = 2
  density = 1
  expand = 3
  formula = G4_POLYETHYLENE
  name = G4_POLYETHYLENE
  specific = 4
FEATURE [App::DocumentObjectGroupPython] C_element082  label="C_element : 040"  # scripted group (container) (typed FeaturePython)
  n = 10
  ref = C_element
FEATURE [App::DocumentObjectGroupPython] H_element076  label="H_element : 038"  # scripted group (container) (typed FeaturePython)
  n = 8
  ref = H_element
FEATURE [App::DocumentObjectGroupPython] O_element078  label="O_element : 039"  # scripted group (container) (typed FeaturePython)
  n = 4
  ref = O_element
FEATURE [App::DocumentObjectGroupPython] G4_MYLAR  # scripted group (container) (typed FeaturePython)
  Dunit = g/cm3
  Dvalue = 1.4
  Group = -> [C_element082,H_element076,O_element078]
  conduct = 2
  density = 1
  expand = 3
  formula = G4_MYLAR
  name = G4_MYLAR
  specific = 4
FEATURE [App::DocumentObjectGroupPython] C_element083  label="C_element : 041"  # scripted group (container) (typed FeaturePython)
  n = 5
  ref = C_element
FEATURE [App::DocumentObjectGroupPython] H_element077  label="H_element : 039"  # scripted group (container) (typed FeaturePython)
  n = 8
  ref = H_element
FEATURE [App::DocumentObjectGroupPython] O_element079  label="O_element : 040"  # scripted group (container) (typed FeaturePython)
  n = 2
  ref = O_element
FEATURE [App::DocumentObjectGroupPython] G4_PLEXIGLASS  # scripted group (container) (typed FeaturePython)
  Dunit = g/cm3
  Dvalue = 1.19
  Group = -> [C_element083,H_element077,O_element079]
  conduct = 2
  density = 1
  expand = 3
  formula = G4_PLEXIGLASS
  name = G4_PLEXIGLASS
  specific = 4
FEATURE [App::DocumentObjectGroupPython] C_element084  label="C_element : 042"  # scripted group (container) (typed FeaturePython)
  n = 1
  ref = C_element
FEATURE [App::DocumentObjectGroupPython] H_element078  label="H_element : 040"  # scripted group (container) (typed FeaturePython)
  n = 2
  ref = H_element
FEATURE [App::DocumentObjectGroupPython] O_element080  label="O_element : 041"  # scripted group (container) (typed FeaturePython)
  n = 1
  ref = O_element
FEATURE [App::DocumentObjectGroupPython] G4_POLYOXYMETHYLENE  # scripted group (container) (typed FeaturePython)
  Dunit = g/cm3
  Dvalue = 1.425
  Group = -> [C_element084,H_element078,O_element080]
  conduct = 2
  density = 1
  expand = 3
  formula = G4_POLYOXYMETHYLENE
  name = G4_POLYOXYMETHYLENE
  specific = 4
FEATURE [App::DocumentObjectGroupPython] C_element085  label="C_element : 043"  # scripted group (container) (typed FeaturePython)
  n = 2
  ref = C_element
FEATURE [App::DocumentObjectGroupPython] H_element079  label="H_element : 041"  # scripted group (container) (typed FeaturePython)
  n = 4
  ref = H_element
FEATURE [App::DocumentObjectGroupPython] G4_POLYPROPYLENE  # scripted group (container) (typed FeaturePython)
  Dunit = g/cm3
  Dvalue = 0.9
  Group = -> [C_element085,H_element079]
  conduct = 2
  density = 1
  expand = 3
  formula = G4_POLYPROPYLENE
  name = G4_POLYPROPYLENE
  specific = 4
FEATURE [App::DocumentObjectGroupPython] C_element086  label="C_element : 044"  # scripted group (container) (typed FeaturePython)
  n = 8
  ref = C_element
FEATURE [App::DocumentObjectGroupPython] H_element080  label="H_element : 042"  # scripted group (container) (typed FeaturePython)
  n = 8
  ref = H_element
FEATURE [App::DocumentObjectGroupPython] G4_POLYSTYRENE  # scripted group (container) (typed FeaturePython)
  Dunit = g/cm3
  Dvalue = 1.06
  Group = -> [C_element086,H_element080]
  conduct = 2
  density = 1
  expand = 3
  formula = G4_POLYSTYRENE
  name = G4_POLYSTYRENE
  specific = 4
FEATURE [App::DocumentObjectGroupPython] C_element087  label="C_element : 045"  # scripted group (container) (typed FeaturePython)
  n = 2
  ref = C_element
FEATURE [App::DocumentObjectGroupPython] F_element014  label="F_element : 4"  # scripted group (container) (typed FeaturePython)
  n = 4
  ref = F_element
FEATURE [App::DocumentObjectGroupPython] G4_TEFLON  # scripted group (container) (typed FeaturePython)
  Dunit = g/cm3
  Dvalue = 2.2
  Group = -> [C_element087,F_element014]
  conduct = 2
  density = 1
  expand = 3
  formula = G4_TEFLON
  name = G4_TEFLON
  specific = 4
FEATURE [App::DocumentObjectGroupPython] C_element088  label="C_element : 046"  # scripted group (container) (typed FeaturePython)
  n = 2
  ref = C_element
FEATURE [App::DocumentObjectGroupPython] F_element015  label="F_element : 006"  # scripted group (container) (typed FeaturePython)
  n = 3
  ref = F_element
FEATURE [App::DocumentObjectGroupPython] Cl_element018  label="Cl_element : 008"  # scripted group (container) (typed FeaturePython)
  n = 1
  ref = Cl_element
FEATURE [App::DocumentObjectGroupPython] G4_POLYTRIFLUOROCHLOROETHYLENE  # scripted group (container) (typed FeaturePython)
  Dunit = g/cm3
  Dvalue = 2.1
  Group = -> [C_element088,F_element015,Cl_element018]
  conduct = 2
  density = 1
  expand = 3
  formula = G4_POLYTRIFLUOROCHLOROETHYLENE
  name = G4_POLYTRIFLUOROCHLOROETHYLENE
  specific = 4
FEATURE [App::DocumentObjectGroupPython] C_element089  label="C_element : 047"  # scripted group (container) (typed FeaturePython)
  n = 4
  ref = C_element
FEATURE [App::DocumentObjectGroupPython] H_element081  label="H_element : 043"  # scripted group (container) (typed FeaturePython)
  n = 6
  ref = H_element
FEATURE [App::DocumentObjectGroupPython] O_element081  label="O_element : 042"  # scripted group (container) (typed FeaturePython)
  n = 2
  ref = O_element
FEATURE [App::DocumentObjectGroupPython] G4_POLYVINYL_ACETATE  # scripted group (container) (typed FeaturePython)
  Dunit = g/cm3
  Dvalue = 1.19
  Group = -> [C_element089,H_element081,O_element081]
  conduct = 2
  density = 1
  expand = 3
  formula = G4_POLYVINYL_ACETATE
  name = G4_POLYVINYL_ACETATE
  specific = 4
FEATURE [App::DocumentObjectGroupPython] C_element090  label="C_element : 048"  # scripted group (container) (typed FeaturePython)
  n = 2
  ref = C_element
FEATURE [App::DocumentObjectGroupPython] H_element082  label="H_element : 044"  # scripted group (container) (typed FeaturePython)
  n = 4
  ref = H_element
FEATURE [App::DocumentObjectGroupPython] O_element082  label="O_element : 043"  # scripted group (container) (typed FeaturePython)
  n = 1
  ref = O_element
FEATURE [App::DocumentObjectGroupPython] G4_POLYVINYL_ALCOHOL  # scripted group (container) (typed FeaturePython)
  Dunit = g/cm3
  Dvalue = 1.3
  Group = -> [C_element090,H_element082,O_element082]
  conduct = 2
  density = 1
  expand = 3
  formula = G4_POLYVINYL_ALCOHOL
  name = G4_POLYVINYL_ALCOHOL
  specific = 4
FEATURE [App::DocumentObjectGroupPython] C_element091  label="C_element : 049"  # scripted group (container) (typed FeaturePython)
  n = 8
  ref = C_element
FEATURE [App::DocumentObjectGroupPython] H_element083  label="H_element : 045"  # scripted group (container) (typed FeaturePython)
  n = 14
  ref = H_element
FEATURE [App::DocumentObjectGroupPython] O_element083  label="O_element : 044"  # scripted group (container) (typed FeaturePython)
  n = 2
  ref = O_element
FEATURE [App::DocumentObjectGroupPython] G4_POLYVINYL_BUTYRAL  # scripted group (container) (typed FeaturePython)
  Dunit = g/cm3
  Dvalue = 1.12
  Group = -> [C_element091,H_element083,O_element083]
  conduct = 2
  density = 1
  expand = 3
  formula = G4_POLYVINYL_BUTYRAL
  name = G4_POLYVINYL_BUTYRAL
  specific = 4
FEATURE [App::DocumentObjectGroupPython] C_element092  label="C_element : 050"  # scripted group (container) (typed FeaturePython)
  n = 2
  ref = C_element
FEATURE [App::DocumentObjectGroupPython] H_element084  label="H_element : 046"  # scripted group (container) (typed FeaturePython)
  n = 3
  ref = H_element
FEATURE [App::DocumentObjectGroupPython] Cl_element019  label="Cl_element : 009"  # scripted group (container) (typed FeaturePython)
  n = 1
  ref = Cl_element
FEATURE [App::DocumentObjectGroupPython] G4_POLYVINYL_CHLORIDE  # scripted group (container) (typed FeaturePython)
  Dunit = g/cm3
  Dvalue = 1.3
  Group = -> [C_element092,H_element084,Cl_element019]
  conduct = 2
  density = 1
  expand = 3
  formula = G4_POLYVINYL_CHLORIDE
  name = G4_POLYVINYL_CHLORIDE
  specific = 4
FEATURE [App::DocumentObjectGroupPython] C_element093  label="C_element : 051"  # scripted group (container) (typed FeaturePython)
  n = 2
  ref = C_element
FEATURE [App::DocumentObjectGroupPython] H_element085  label="H_element : 047"  # scripted group (container) (typed FeaturePython)
  n = 2
  ref = H_element
FEATURE [App::DocumentObjectGroupPython] Cl_element020  label="Cl_element : 010"  # scripted group (container) (typed FeaturePython)
  n = 2
  ref = Cl_element
FEATURE [App::DocumentObjectGroupPython] G4_POLYVINYLIDENE_CHLORIDE  # scripted group (container) (typed FeaturePython)
  Dunit = g/cm3
  Dvalue = 1.7
  Group = -> [C_element093,H_element085,Cl_element020]
  conduct = 2
  density = 1
  expand = 3
  formula = G4_POLYVINYLIDENE_CHLORIDE
  name = G4_POLYVINYLIDENE_CHLORIDE
  specific = 4
FEATURE [App::DocumentObjectGroupPython] C_element094  label="C_element : 052"  # scripted group (container) (typed FeaturePython)
  n = 2
  ref = C_element
FEATURE [App::DocumentObjectGroupPython] H_element086  label="H_element : 048"  # scripted group (container) (typed FeaturePython)
  n = 2
  ref = H_element
FEATURE [App::DocumentObjectGroupPython] F_element016  label="F_element : 007"  # scripted group (container) (typed FeaturePython)
  n = 2
  ref = F_element
FEATURE [App::DocumentObjectGroupPython] G4_POLYVINYLIDENE_FLUORIDE  # scripted group (container) (typed FeaturePython)
  Dunit = g/cm3
  Dvalue = 1.76
  Group = -> [C_element094,H_element086,F_element016]
  conduct = 2
  density = 1
  expand = 3
  formula = G4_POLYVINYLIDENE_FLUORIDE
  name = G4_POLYVINYLIDENE_FLUORIDE
  specific = 4
FEATURE [App::DocumentObjectGroupPython] C_element095  label="C_element : 053"  # scripted group (container) (typed FeaturePython)
  n = 6
  ref = C_element
FEATURE [App::DocumentObjectGroupPython] H_element087  label="H_element : 9"  # scripted group (container) (typed FeaturePython)
  n = 9
  ref = H_element
FEATURE [App::DocumentObjectGroupPython] N_element037  label="N_element : 016"  # scripted group (container) (typed FeaturePython)
  n = 1
  ref = N_element
FEATURE [App::DocumentObjectGroupPython] O_element084  label="O_element : 045"  # scripted group (container) (typed FeaturePython)
  n = 1
  ref = O_element
FEATURE [App::DocumentObjectGroupPython] G4_POLYVINYL_PYRROLIDONE  # scripted group (container) (typed FeaturePython)
  Dunit = g/cm3
  Dvalue = 1.25
  Group = -> [C_element095,H_element087,N_element037,O_element084]
  conduct = 2
  density = 1
  expand = 3
  formula = G4_POLYVINYL_PYRROLIDONE
  name = G4_POLYVINYL_PYRROLIDONE
  specific = 4
FEATURE [App::DocumentObjectGroupPython] K_element008  label="K_element : 1"  # scripted group (container) (typed FeaturePython)
  n = 1
  ref = K_element
FEATURE [App::DocumentObjectGroupPython] I_element006  label="I_element : 003"  # scripted group (container) (typed FeaturePython)
  n = 1
  ref = I_element
FEATURE [App::DocumentObjectGroupPython] G4_POTASSIUM_IODIDE  # scripted group (container) (typed FeaturePython)
  Dunit = g/cm3
  Dvalue = 3.13
  Group = -> [K_element008,I_element006]
  conduct = 2
  density = 1
  expand = 3
  formula = G4_POTASSIUM_IODIDE
  name = G4_POTASSIUM_IODIDE
  specific = 4
FEATURE [App::DocumentObjectGroupPython] K_element009  label="K_element : 2"  # scripted group (container) (typed FeaturePython)
  n = 2
  ref = K_element
FEATURE [App::DocumentObjectGroupPython] O_element085  label="O_element : 046"  # scripted group (container) (typed FeaturePython)
  n = 1
  ref = O_element
FEATURE [App::DocumentObjectGroupPython] G4_POTASSIUM_OXIDE  # scripted group (container) (typed FeaturePython)
  Dunit = g/cm3
  Dvalue = 2.32
  Group = -> [K_element009,O_element085]
  conduct = 2
  density = 1
  expand = 3
  formula = G4_POTASSIUM_OXIDE
  name = G4_POTASSIUM_OXIDE
  specific = 4
FEATURE [App::DocumentObjectGroupPython] C_element096  label="C_element : 054"  # scripted group (container) (typed FeaturePython)
  n = 3
  ref = C_element
FEATURE [App::DocumentObjectGroupPython] H_element088  label="H_element : 049"  # scripted group (container) (typed FeaturePython)
  n = 8
  ref = H_element
FEATURE [App::DocumentObjectGroupPython] G4_PROPANE  # scripted group (container) (typed FeaturePython)
  Dunit = g/cm3
  Dvalue = 0.00187939
  Group = -> [C_element096,H_element088]
  conduct = 2
  density = 1
  expand = 3
  formula = G4_PROPANE
  name = G4_PROPANE
  specific = 4
FEATURE [App::DocumentObjectGroupPython] C_element097  label="C_element : 055"  # scripted group (container) (typed FeaturePython)
  n = 3
  ref = C_element
FEATURE [App::DocumentObjectGroupPython] H_element089  label="H_element : 050"  # scripted group (container) (typed FeaturePython)
  n = 8
  ref = H_element
FEATURE [App::DocumentObjectGroupPython] G4_lPROPANE  # scripted group (container) (typed FeaturePython)
  Dunit = g/cm3
  Dvalue = 0.43
  Group = -> [C_element097,H_element089]
  conduct = 2
  density = 1
  expand = 3
  formula = G4_lPROPANE
  name = G4_lPROPANE
  specific = 4
FEATURE [App::DocumentObjectGroupPython] C_element098  label="C_element : 056"  # scripted group (container) (typed FeaturePython)
  n = 3
  ref = C_element
FEATURE [App::DocumentObjectGroupPython] H_element090  label="H_element : 051"  # scripted group (container) (typed FeaturePython)
  n = 8
  ref = H_element
FEATURE [App::DocumentObjectGroupPython] O_element086  label="O_element : 047"  # scripted group (container) (typed FeaturePython)
  n = 1
  ref = O_element
FEATURE [App::DocumentObjectGroupPython] G4_N_PROPYL_ALCOHOL  label="G4_N-PROPYL_ALCOHOL"  # scripted group (container) (typed FeaturePython)
  Dunit = g/cm3
  Dvalue = 0.8035
  Group = -> [C_element098,H_element090,O_element086]
  conduct = 2
  density = 1
  expand = 3
  formula = G4_N-PROPYL_ALCOHOL
  name = G4_N-PROPYL_ALCOHOL
  specific = 4
FEATURE [App::DocumentObjectGroupPython] C_element099  label="C_element : 057"  # scripted group (container) (typed FeaturePython)
  n = 5
  ref = C_element
FEATURE [App::DocumentObjectGroupPython] H_element091  label="H_element : 052"  # scripted group (container) (typed FeaturePython)
  n = 5
  ref = H_element
FEATURE [App::DocumentObjectGroupPython] N_element038  label="N_element : 017"  # scripted group (container) (typed FeaturePython)
  n = 1
  ref = N_element
FEATURE [App::DocumentObjectGroupPython] G4_PYRIDINE  # scripted group (container) (typed FeaturePython)
  Dunit = g/cm3
  Dvalue = 0.9819
  Group = -> [C_element099,H_element091,N_element038]
  conduct = 2
  density = 1
  expand = 3
  formula = G4_PYRIDINE
  name = G4_PYRIDINE
  specific = 4
FEATURE [App::DocumentObjectGroupPython] H_element092  label="H_element : 0.144"  # scripted group (container) (typed FeaturePython)
  n = 0.143711
FEATURE [App::DocumentObjectGroupPython] C_element100  label="C_element : 0.856"  # scripted group (container) (typed FeaturePython)
  n = 0.856289
FEATURE [App::DocumentObjectGroupPython] G4_RUBBER_BUTYL  # scripted group (container) (typed FeaturePython)
  Dunit = g/cm3
  Dvalue = 0.92
  Group = -> [H_element092,C_element100]
  conduct = 2
  density = 1
  expand = 3
  formula = G4_RUBBER_BUTYL
  name = G4_RUBBER_BUTYL
  specific = 4
FEATURE [App::DocumentObjectGroupPython] H_element093  label="H_element : 0.118"  # scripted group (container) (typed FeaturePython)
  n = 0.118371
FEATURE [App::DocumentObjectGroupPython] C_element101  label="C_element : 0.882"  # scripted group (container) (typed FeaturePython)
  n = 0.881629
FEATURE [App::DocumentObjectGroupPython] G4_RUBBER_NATURAL  # scripted group (container) (typed FeaturePython)
  Dunit = g/cm3
  Dvalue = 0.92
  Group = -> [H_element093,C_element101]
  conduct = 2
  density = 1
  expand = 3
  formula = G4_RUBBER_NATURAL
  name = G4_RUBBER_NATURAL
  specific = 4
FEATURE [App::DocumentObjectGroupPython] H_element094  label="H_element : 0.145"  # scripted group (container) (typed FeaturePython)
  n = 0.05692
FEATURE [App::DocumentObjectGroupPython] C_element102  label="C_element : 0.543"  # scripted group (container) (typed FeaturePython)
  n = 0.542646
FEATURE [App::DocumentObjectGroupPython] Cl_element021  label="Cl_element : 0.400"  # scripted group (container) (typed FeaturePython)
  n = 0.400434
FEATURE [App::DocumentObjectGroupPython] G4_RUBBER_NEOPRENE  # scripted group (container) (typed FeaturePython)
  Dunit = g/cm3
  Dvalue = 1.23
  Group = -> [H_element094,C_element102,Cl_element021]
  conduct = 2
  density = 1
  expand = 3
  formula = G4_RUBBER_NEOPRENE
  name = G4_RUBBER_NEOPRENE
  specific = 4
FEATURE [App::DocumentObjectGroupPython] Si_element006  label="Si_element : 1"  # scripted group (container) (typed FeaturePython)
  n = 1
  ref = Si_element
FEATURE [App::DocumentObjectGroupPython] O_element087  label="O_element : 048"  # scripted group (container) (typed FeaturePython)
  n = 2
  ref = O_element
FEATURE [App::DocumentObjectGroupPython] G4_SILICON_DIOXIDE  # scripted group (container) (typed FeaturePython)
  Dunit = g/cm3
  Dvalue = 2.32
  Group = -> [Si_element006,O_element087]
  conduct = 2
  density = 1
  expand = 3
  formula = G4_SILICON_DIOXIDE
  name = G4_SILICON_DIOXIDE
  specific = 4
FEATURE [App::DocumentObjectGroupPython] Ag_element002  label="Ag_element : 1"  # scripted group (container) (typed FeaturePython)
  n = 1
  ref = Ag_element
FEATURE [App::DocumentObjectGroupPython] Br_element005  label="Br_element : 003"  # scripted group (container) (typed FeaturePython)
  n = 1
  ref = Br_element
FEATURE [App::DocumentObjectGroupPython] G4_SILVER_BROMIDE  # scripted group (container) (typed FeaturePython)
  Dunit = g/cm3
  Dvalue = 6.473
  Group = -> [Ag_element002,Br_element005]
  conduct = 2
  density = 1
  expand = 3
  formula = G4_SILVER_BROMIDE
  name = G4_SILVER_BROMIDE
  specific = 4
FEATURE [App::DocumentObjectGroupPython] Ag_element003  label="Ag_element : 002"  # scripted group (container) (typed FeaturePython)
  n = 1
  ref = Ag_element
FEATURE [App::DocumentObjectGroupPython] Cl_element022  label="Cl_element : 011"  # scripted group (container) (typed FeaturePython)
  n = 1
  ref = Cl_element
FEATURE [App::DocumentObjectGroupPython] G4_SILVER_CHLORIDE  # scripted group (container) (typed FeaturePython)
  Dunit = g/cm3
  Dvalue = 5.56
  Group = -> [Ag_element003,Cl_element022]
  conduct = 2
  density = 1
  expand = 3
  formula = G4_SILVER_CHLORIDE
  name = G4_SILVER_CHLORIDE
  specific = 4
FEATURE [App::DocumentObjectGroupPython] Br_element006  label="Br_element : 0.423"  # scripted group (container) (typed FeaturePython)
  n = 0.422895
FEATURE [App::DocumentObjectGroupPython] Ag_element004  label="Ag_element : 0.574"  # scripted group (container) (typed FeaturePython)
  n = 0.573748
FEATURE [App::DocumentObjectGroupPython] I_element007  label="I_element : 0.649"  # scripted group (container) (typed FeaturePython)
  n = 0.003357
FEATURE [App::DocumentObjectGroupPython] G4_SILVER_HALIDES  # scripted group (container) (typed FeaturePython)
  Dunit = g/cm3
  Dvalue = 6.47
  Group = -> [Br_element006,Ag_element004,I_element007]
  conduct = 2
  density = 1
  expand = 3
  formula = G4_SILVER_HALIDES
  name = G4_SILVER_HALIDES
  specific = 4
FEATURE [App::DocumentObjectGroupPython] Ag_element005  label="Ag_element : 003"  # scripted group (container) (typed FeaturePython)
  n = 1
  ref = Ag_element
FEATURE [App::DocumentObjectGroupPython] I_element008  label="I_element : 004"  # scripted group (container) (typed FeaturePython)
  n = 1
  ref = I_element
FEATURE [App::DocumentObjectGroupPython] G4_SILVER_IODIDE  # scripted group (container) (typed FeaturePython)
  Dunit = g/cm3
  Dvalue = 6.01
  Group = -> [Ag_element005,I_element008]
  conduct = 2
  density = 1
  expand = 3
  formula = G4_SILVER_IODIDE
  name = G4_SILVER_IODIDE
  specific = 4
FEATURE [App::DocumentObjectGroupPython] H_element095  label="H_element : 0.100"  # scripted group (container) (typed FeaturePython)
  n = 0.1
FEATURE [App::DocumentObjectGroupPython] C_element103  label="C_element : 0.204"  # scripted group (container) (typed FeaturePython)
  n = 0.204
FEATURE [App::DocumentObjectGroupPython] N_element039  label="N_element : 0.759"  # scripted group (container) (typed FeaturePython)
  n = 0.042
FEATURE [App::DocumentObjectGroupPython] O_element088  label="O_element : 0.645"  # scripted group (container) (typed FeaturePython)
  n = 0.645
FEATURE [App::DocumentObjectGroupPython] Na_element013  label="Na_element : 0.100"  # scripted group (container) (typed FeaturePython)
  n = 0.002
FEATURE [App::DocumentObjectGroupPython] P_element009  label="P_element : 0.107"  # scripted group (container) (typed FeaturePython)
  n = 0.001
FEATURE [App::DocumentObjectGroupPython] S_element020  label="S_element : 0.021"  # scripted group (container) (typed FeaturePython)
  n = 0.002
FEATURE [App::DocumentObjectGroupPython] Cl_element023  label="Cl_element : 0.590"  # scripted group (container) (typed FeaturePython)
  n = 0.003
FEATURE [App::DocumentObjectGroupPython] K_element010  label="K_element : 0.001"  # scripted group (container) (typed FeaturePython)
  n = 0.001
FEATURE [App::DocumentObjectGroupPython] G4_SKIN_ICRP  # scripted group (container) (typed FeaturePython)
  Dunit = g/cm3
  Dvalue = 1.09
  Group = -> [H_element095,C_element103,N_element039,O_element088,Na_element013,P_element009,S_element020,Cl_element023,K_element010]
  conduct = 2
  density = 1
  expand = 3
  formula = G4_SKIN_ICRP
  name = G4_SKIN_ICRP
  specific = 4
FEATURE [App::DocumentObjectGroupPython] Na_element014  label="Na_element : 2"  # scripted group (container) (typed FeaturePython)
  n = 2
  ref = Na_element
FEATURE [App::DocumentObjectGroupPython] C_element104  label="C_element : 058"  # scripted group (container) (typed FeaturePython)
  n = 1
  ref = C_element
FEATURE [App::DocumentObjectGroupPython] O_element089  label="O_element : 049"  # scripted group (container) (typed FeaturePython)
  n = 3
  ref = O_element
FEATURE [App::DocumentObjectGroupPython] G4_SODIUM_CARBONATE  # scripted group (container) (typed FeaturePython)
  Dunit = g/cm3
  Dvalue = 2.532
  Group = -> [Na_element014,C_element104,O_element089]
  conduct = 2
  density = 1
  expand = 3
  formula = G4_SODIUM_CARBONATE
  name = G4_SODIUM_CARBONATE
  specific = 4
FEATURE [App::DocumentObjectGroupPython] Na_element015  label="Na_element : 1"  # scripted group (container) (typed FeaturePython)
  n = 1
  ref = Na_element
FEATURE [App::DocumentObjectGroupPython] I_element009  label="I_element : 005"  # scripted group (container) (typed FeaturePython)
  n = 1
  ref = I_element
FEATURE [App::DocumentObjectGroupPython] G4_SODIUM_IODIDE  # scripted group (container) (typed FeaturePython)
  Dunit = g/cm3
  Dvalue = 3.667
  Group = -> [Na_element015,I_element009]
  conduct = 2
  density = 1
  expand = 3
  formula = G4_SODIUM_IODIDE
  name = G4_SODIUM_IODIDE
  specific = 4
FEATURE [App::DocumentObjectGroupPython] Na_element016  label="Na_element : 003"  # scripted group (container) (typed FeaturePython)
  n = 2
  ref = Na_element
FEATURE [App::DocumentObjectGroupPython] O_element090  label="O_element : 050"  # scripted group (container) (typed FeaturePython)
  n = 1
  ref = O_element
FEATURE [App::DocumentObjectGroupPython] G4_SODIUM_MONOXIDE  # scripted group (container) (typed FeaturePython)
  Dunit = g/cm3
  Dvalue = 2.27
  Group = -> [Na_element016,O_element090]
  conduct = 2
  density = 1
  expand = 3
  formula = G4_SODIUM_MONOXIDE
  name = G4_SODIUM_MONOXIDE
  specific = 4
FEATURE [App::DocumentObjectGroupPython] Na_element017  label="Na_element : 004"  # scripted group (container) (typed FeaturePython)
  n = 1
  ref = Na_element
FEATURE [App::DocumentObjectGroupPython] N_element040  label="N_element : 018"  # scripted group (container) (typed FeaturePython)
  n = 1
  ref = N_element
FEATURE [App::DocumentObjectGroupPython] O_element091  label="O_element : 051"  # scripted group (container) (typed FeaturePython)
  n = 3
  ref = O_element
FEATURE [App::DocumentObjectGroupPython] G4_SODIUM_NITRATE  # scripted group (container) (typed FeaturePython)
  Dunit = g/cm3
  Dvalue = 2.261
  Group = -> [Na_element017,N_element040,O_element091]
  conduct = 2
  density = 1
  expand = 3
  formula = G4_SODIUM_NITRATE
  name = G4_SODIUM_NITRATE
  specific = 4
FEATURE [App::DocumentObjectGroupPython] C_element105  label="C_element : 059"  # scripted group (container) (typed FeaturePython)
  n = 14
  ref = C_element
FEATURE [App::DocumentObjectGroupPython] H_element096  label="H_element : 053"  # scripted group (container) (typed FeaturePython)
  n = 12
  ref = H_element
FEATURE [App::DocumentObjectGroupPython] G4_STILBENE  # scripted group (container) (typed FeaturePython)
  Dunit = g/cm3
  Dvalue = 0.9707
  Group = -> [C_element105,H_element096]
  conduct = 2
  density = 1
  expand = 3
  formula = G4_STILBENE
  name = G4_STILBENE
  specific = 4
FEATURE [App::DocumentObjectGroupPython] C_element106  label="C_element : 12"  # scripted group (container) (typed FeaturePython)
  n = 12
  ref = C_element
FEATURE [App::DocumentObjectGroupPython] H_element097  label="H_element : 22"  # scripted group (container) (typed FeaturePython)
  n = 22
  ref = H_element
FEATURE [App::DocumentObjectGroupPython] O_element092  label="O_element : 11"  # scripted group (container) (typed FeaturePython)
  n = 11
  ref = O_element
FEATURE [App::DocumentObjectGroupPython] G4_SUCROSE  # scripted group (container) (typed FeaturePython)
  Dunit = g/cm3
  Dvalue = 1.5805
  Group = -> [C_element106,H_element097,O_element092]
  conduct = 2
  density = 1
  expand = 3
  formula = G4_SUCROSE
  name = G4_SUCROSE
  specific = 4
FEATURE [App::DocumentObjectGroupPython] C_element107  label="C_element : 18"  # scripted group (container) (typed FeaturePython)
  n = 18
  ref = C_element
FEATURE [App::DocumentObjectGroupPython] H_element098  label="H_element : 054"  # scripted group (container) (typed FeaturePython)
  n = 14
  ref = H_element
FEATURE [App::DocumentObjectGroupPython] G4_TERPHENYL  # scripted group (container) (typed FeaturePython)
  Dunit = g/cm3
  Dvalue = 1.24
  Group = -> [C_element107,H_element098]
  conduct = 2
  density = 1
  expand = 3
  formula = G4_TERPHENYL
  name = G4_TERPHENYL
  specific = 4
FEATURE [App::DocumentObjectGroupPython] H_element099  label="H_element : 0.146"  # scripted group (container) (typed FeaturePython)
  n = 0.106
FEATURE [App::DocumentObjectGroupPython] C_element108  label="C_element : 0.883"  # scripted group (container) (typed FeaturePython)
  n = 0.099
FEATURE [App::DocumentObjectGroupPython] N_element041  label="N_element : 0.020"  # scripted group (container) (typed FeaturePython)
  n = 0.02
FEATURE [App::DocumentObjectGroupPython] O_element093  label="O_element : 0.766"  # scripted group (container) (typed FeaturePython)
  n = 0.766
FEATURE [App::DocumentObjectGroupPython] Na_element018  label="Na_element : 0.101"  # scripted group (container) (typed FeaturePython)
  n = 0.002
FEATURE [App::DocumentObjectGroupPython] P_element010  label="P_element : 0.108"  # scripted group (container) (typed FeaturePython)
  n = 0.001
FEATURE [App::DocumentObjectGroupPython] S_element021  label="S_element : 0.022"  # scripted group (container) (typed FeaturePython)
  n = 0.002
FEATURE [App::DocumentObjectGroupPython] Cl_element024  label="Cl_element : 0.002"  # scripted group (container) (typed FeaturePython)
  n = 0.002
FEATURE [App::DocumentObjectGroupPython] K_element011  label="K_element : 0.017"  # scripted group (container) (typed FeaturePython)
  n = 0.002
FEATURE [App::DocumentObjectGroupPython] G4_TESTIS_ICRP  # scripted group (container) (typed FeaturePython)
  Dunit = g/cm3
  Dvalue = 1.04
  Group = -> [H_element099,C_element108,N_element041,O_element093,Na_element018,P_element010,S_element021,Cl_element024,K_element011]
  conduct = 2
  density = 1
  expand = 3
  formula = G4_TESTIS_ICRP
  name = G4_TESTIS_ICRP
  specific = 4
FEATURE [App::DocumentObjectGroupPython] C_element109  label="C_element : 060"  # scripted group (container) (typed FeaturePython)
  n = 2
  ref = C_element
FEATURE [App::DocumentObjectGroupPython] Cl_element025  label="Cl_element : 012"  # scripted group (container) (typed FeaturePython)
  n = 4
  ref = Cl_element
FEATURE [App::DocumentObjectGroupPython] G4_TETRACHLOROETHYLENE  # scripted group (container) (typed FeaturePython)
  Dunit = g/cm3
  Dvalue = 1.625
  Group = -> [C_element109,Cl_element025]
  conduct = 2
  density = 1
  expand = 3
  formula = G4_TETRACHLOROETHYLENE
  name = G4_TETRACHLOROETHYLENE
  specific = 4
FEATURE [App::DocumentObjectGroupPython] Tl_element001  label="Tl_element : 1"  # scripted group (container) (typed FeaturePython)
  n = 1
  ref = Tl_element
FEATURE [App::DocumentObjectGroupPython] Cl_element026  label="Cl_element : 013"  # scripted group (container) (typed FeaturePython)
  n = 1
  ref = Cl_element
FEATURE [App::DocumentObjectGroupPython] G4_THALLIUM_CHLORIDE  # scripted group (container) (typed FeaturePython)
  Dunit = g/cm3
  Dvalue = 7.004
  Group = -> [Tl_element001,Cl_element026]
  conduct = 2
  density = 1
  expand = 3
  formula = G4_THALLIUM_CHLORIDE
  name = G4_THALLIUM_CHLORIDE
  specific = 4
FEATURE [App::DocumentObjectGroupPython] H_element100  label="H_element : 0.147"  # scripted group (container) (typed FeaturePython)
  n = 0.105
FEATURE [App::DocumentObjectGroupPython] C_element110  label="C_element : 0.256"  # scripted group (container) (typed FeaturePython)
  n = 0.256
FEATURE [App::DocumentObjectGroupPython] N_element042  label="N_element : 0.760"  # scripted group (container) (typed FeaturePython)
  n = 0.027
FEATURE [App::DocumentObjectGroupPython] O_element094  label="O_element : 0.602"  # scripted group (container) (typed FeaturePython)
  n = 0.602
FEATURE [App::DocumentObjectGroupPython] Na_element019  label="Na_element : 0.102"  # scripted group (container) (typed FeaturePython)
  n = 0.001
FEATURE [App::DocumentObjectGroupPython] P_element011  label="P_element : 0.109"  # scripted group (container) (typed FeaturePython)
  n = 0.002
FEATURE [App::DocumentObjectGroupPython] S_element022  label="S_element : 0.023"  # scripted group (container) (typed FeaturePython)
  n = 0.003
FEATURE [App::DocumentObjectGroupPython] Cl_element027  label="Cl_element : 0.591"  # scripted group (container) (typed FeaturePython)
  n = 0.002
FEATURE [App::DocumentObjectGroupPython] K_element012  label="K_element : 0.018"  # scripted group (container) (typed FeaturePython)
  n = 0.002
FEATURE [App::DocumentObjectGroupPython] G4_TISSUE_SOFT_ICRP  # scripted group (container) (typed FeaturePython)
  Dunit = g/cm3
  Dvalue = 1.03
  Group = -> [H_element100,C_element110,N_element042,O_element094,Na_element019,P_element011,S_element022,Cl_element027,K_element012]
  conduct = 2
  density = 1
  expand = 3
  formula = G4_TISSUE_SOFT_ICRP
  name = G4_TISSUE_SOFT_ICRP
  specific = 4
FEATURE [App::DocumentObjectGroupPython] H_element101  label="H_element : 0.148"  # scripted group (container) (typed FeaturePython)
  n = 0.101
FEATURE [App::DocumentObjectGroupPython] C_element111  label="C_element : 0.111"  # scripted group (container) (typed FeaturePython)
  n = 0.111
FEATURE [App::DocumentObjectGroupPython] N_element043  label="N_element : 0.026"  # scripted group (container) (typed FeaturePython)
  n = 0.026
FEATURE [App::DocumentObjectGroupPython] O_element095  label="O_element : 0.762"  # scripted group (container) (typed FeaturePython)
  n = 0.762
FEATURE [App::DocumentObjectGroupPython] G4_TISSUE_SOFT_ICRU_4  label="G4_TISSUE_SOFT_ICRU-4"  # scripted group (container) (typed FeaturePython)
  Dunit = g/cm3
  Dvalue = 1
  Group = -> [H_element101,C_element111,N_element043,O_element095]
  conduct = 2
  density = 1
  expand = 3
  formula = G4_TISSUE_SOFT_ICRU-4
  name = G4_TISSUE_SOFT_ICRU-4
  specific = 4
FEATURE [App::DocumentObjectGroupPython] H_element102  label="H_element : 0.149"  # scripted group (container) (typed FeaturePython)
  n = 0.101869
FEATURE [App::DocumentObjectGroupPython] C_element112  label="C_element : 0.456"  # scripted group (container) (typed FeaturePython)
  n = 0.456179
FEATURE [App::DocumentObjectGroupPython] N_element044  label="N_element : 0.761"  # scripted group (container) (typed FeaturePython)
  n = 0.035172
FEATURE [App::DocumentObjectGroupPython] O_element096  label="O_element : 0.407"  # scripted group (container) (typed FeaturePython)
  n = 0.40678
FEATURE [App::DocumentObjectGroupPython] G4_TISSUE_METHANE  label="G4_TISSUE-METHANE"  # scripted group (container) (typed FeaturePython)
  Dunit = g/cm3
  Dvalue = 0.00106409
  Group = -> [H_element102,C_element112,N_element044,O_element096]
  conduct = 2
  density = 1
  expand = 3
  formula = G4_TISSUE-METHANE
  name = G4_TISSUE-METHANE
  specific = 4
FEATURE [App::DocumentObjectGroupPython] H_element103  label="H_element : 0.103"  # scripted group (container) (typed FeaturePython)
  n = 0.102672
FEATURE [App::DocumentObjectGroupPython] C_element113  label="C_element : 0.569"  # scripted group (container) (typed FeaturePython)
  n = 0.56894
FEATURE [App::DocumentObjectGroupPython] N_element045  label="N_element : 0.762"  # scripted group (container) (typed FeaturePython)
  n = 0.035022
FEATURE [App::DocumentObjectGroupPython] O_element097  label="O_element : 0.293"  # scripted group (container) (typed FeaturePython)
  n = 0.293366
FEATURE [App::DocumentObjectGroupPython] G4_TISSUE_PROPANE  label="G4_TISSUE-PROPANE"  # scripted group (container) (typed FeaturePython)
  Dunit = g/cm3
  Dvalue = 0.00182628
  Group = -> [H_element103,C_element113,N_element045,O_element097]
  conduct = 2
  density = 1
  expand = 3
  formula = G4_TISSUE-PROPANE
  name = G4_TISSUE-PROPANE
  specific = 4
FEATURE [App::DocumentObjectGroupPython] Ti_element003  label="Ti_element : 1"  # scripted group (container) (typed FeaturePython)
  n = 1
  ref = Ti_element
FEATURE [App::DocumentObjectGroupPython] O_element098  label="O_element : 052"  # scripted group (container) (typed FeaturePython)
  n = 2
  ref = O_element
FEATURE [App::DocumentObjectGroupPython] G4_TITANIUM_DIOXIDE  # scripted group (container) (typed FeaturePython)
  Dunit = g/cm3
  Dvalue = 4.26
  Group = -> [Ti_element003,O_element098]
  conduct = 2
  density = 1
  expand = 3
  formula = G4_TITANIUM_DIOXIDE
  name = G4_TITANIUM_DIOXIDE
  specific = 4
FEATURE [App::DocumentObjectGroupPython] C_element114  label="C_element : 061"  # scripted group (container) (typed FeaturePython)
  n = 7
  ref = C_element
FEATURE [App::DocumentObjectGroupPython] H_element104  label="H_element : 055"  # scripted group (container) (typed FeaturePython)
  n = 8
  ref = H_element
FEATURE [App::DocumentObjectGroupPython] G4_TOLUENE  # scripted group (container) (typed FeaturePython)
  Dunit = g/cm3
  Dvalue = 0.8669
  Group = -> [C_element114,H_element104]
  conduct = 2
  density = 1
  expand = 3
  formula = G4_TOLUENE
  name = G4_TOLUENE
  specific = 4
FEATURE [App::DocumentObjectGroupPython] C_element115  label="C_element : 062"  # scripted group (container) (typed FeaturePython)
  n = 2
  ref = C_element
FEATURE [App::DocumentObjectGroupPython] H_element105  label="H_element : 056"  # scripted group (container) (typed FeaturePython)
  n = 1
  ref = H_element
FEATURE [App::DocumentObjectGroupPython] Cl_element028  label="Cl_element : 014"  # scripted group (container) (typed FeaturePython)
  n = 3
  ref = Cl_element
FEATURE [App::DocumentObjectGroupPython] G4_TRICHLOROETHYLENE  # scripted group (container) (typed FeaturePython)
  Dunit = g/cm3
  Dvalue = 1.46
  Group = -> [C_element115,H_element105,Cl_element028]
  conduct = 2
  density = 1
  expand = 3
  formula = G4_TRICHLOROETHYLENE
  name = G4_TRICHLOROETHYLENE
  specific = 4
FEATURE [App::DocumentObjectGroupPython] C_element116  label="C_element : 063"  # scripted group (container) (typed FeaturePython)
  n = 6
  ref = C_element
FEATURE [App::DocumentObjectGroupPython] H_element106  label="H_element : 15"  # scripted group (container) (typed FeaturePython)
  n = 15
  ref = H_element
FEATURE [App::DocumentObjectGroupPython] O_element099  label="O_element : 053"  # scripted group (container) (typed FeaturePython)
  n = 4
  ref = O_element
FEATURE [App::DocumentObjectGroupPython] P_element012  label="P_element : 1"  # scripted group (container) (typed FeaturePython)
  n = 1
  ref = P_element
FEATURE [App::DocumentObjectGroupPython] G4_TRIETHYL_PHOSPHATE  # scripted group (container) (typed FeaturePython)
  Dunit = g/cm3
  Dvalue = 1.07
  Group = -> [C_element116,H_element106,O_element099,P_element012]
  conduct = 2
  density = 1
  expand = 3
  formula = G4_TRIETHYL_PHOSPHATE
  name = G4_TRIETHYL_PHOSPHATE
  specific = 4
FEATURE [App::DocumentObjectGroupPython] W_element003  label="W_element : 003"  # scripted group (container) (typed FeaturePython)
  n = 1
  ref = W_element
FEATURE [App::DocumentObjectGroupPython] F_element017  label="F_element : 6"  # scripted group (container) (typed FeaturePython)
  n = 6
  ref = F_element
FEATURE [App::DocumentObjectGroupPython] G4_TUNGSTEN_HEXAFLUORIDE  # scripted group (container) (typed FeaturePython)
  Dunit = g/cm3
  Dvalue = 2.4
  Group = -> [W_element003,F_element017]
  conduct = 2
  density = 1
  expand = 3
  formula = G4_TUNGSTEN_HEXAFLUORIDE
  name = G4_TUNGSTEN_HEXAFLUORIDE
  specific = 4
FEATURE [App::DocumentObjectGroupPython] U_element001  label="U_element : 1"  # scripted group (container) (typed FeaturePython)
  n = 1
  ref = U_element
FEATURE [App::DocumentObjectGroupPython] C_element117  label="C_element : 064"  # scripted group (container) (typed FeaturePython)
  n = 2
  ref = C_element
FEATURE [App::DocumentObjectGroupPython] G4_URANIUM_DICARBIDE  # scripted group (container) (typed FeaturePython)
  Dunit = g/cm3
  Dvalue = 11.28
  Group = -> [U_element001,C_element117]
  conduct = 2
  density = 1
  expand = 3
  formula = G4_URANIUM_DICARBIDE
  name = G4_URANIUM_DICARBIDE
  specific = 4
FEATURE [App::DocumentObjectGroupPython] U_element002  label="U_element : 002"  # scripted group (container) (typed FeaturePython)
  n = 1
  ref = U_element
FEATURE [App::DocumentObjectGroupPython] C_element118  label="C_element : 065"  # scripted group (container) (typed FeaturePython)
  n = 1
  ref = C_element
FEATURE [App::DocumentObjectGroupPython] G4_URANIUM_MONOCARBIDE  # scripted group (container) (typed FeaturePython)
  Dunit = g/cm3
  Dvalue = 13.63
  Group = -> [U_element002,C_element118]
  conduct = 2
  density = 1
  expand = 3
  formula = G4_URANIUM_MONOCARBIDE
  name = G4_URANIUM_MONOCARBIDE
  specific = 4
FEATURE [App::DocumentObjectGroupPython] U_element003  label="U_element : 003"  # scripted group (container) (typed FeaturePython)
  n = 1
  ref = U_element
FEATURE [App::DocumentObjectGroupPython] O_element100  label="O_element : 054"  # scripted group (container) (typed FeaturePython)
  n = 2
  ref = O_element
FEATURE [App::DocumentObjectGroupPython] G4_URANIUM_OXIDE  # scripted group (container) (typed FeaturePython)
  Dunit = g/cm3
  Dvalue = 10.96
  Group = -> [U_element003,O_element100]
  conduct = 2
  density = 1
  expand = 3
  formula = G4_URANIUM_OXIDE
  name = G4_URANIUM_OXIDE
  specific = 4
FEATURE [App::DocumentObjectGroupPython] C_element119  label="C_element : 066"  # scripted group (container) (typed FeaturePython)
  n = 1
  ref = C_element
FEATURE [App::DocumentObjectGroupPython] H_element107  label="H_element : 057"  # scripted group (container) (typed FeaturePython)
  n = 4
  ref = H_element
FEATURE [App::DocumentObjectGroupPython] N_element046  label="N_element : 019"  # scripted group (container) (typed FeaturePython)
  n = 2
  ref = N_element
FEATURE [App::DocumentObjectGroupPython] O_element101  label="O_element : 055"  # scripted group (container) (typed FeaturePython)
  n = 1
  ref = O_element
FEATURE [App::DocumentObjectGroupPython] G4_UREA  # scripted group (container) (typed FeaturePython)
  Dunit = g/cm3
  Dvalue = 1.323
  Group = -> [C_element119,H_element107,N_element046,O_element101]
  conduct = 2
  density = 1
  expand = 3
  formula = G4_UREA
  name = G4_UREA
  specific = 4
FEATURE [App::DocumentObjectGroupPython] C_element120  label="C_element : 067"  # scripted group (container) (typed FeaturePython)
  n = 5
  ref = C_element
FEATURE [App::DocumentObjectGroupPython] H_element108  label="H_element : 058"  # scripted group (container) (typed FeaturePython)
  n = 11
  ref = H_element
FEATURE [App::DocumentObjectGroupPython] N_element047  label="N_element : 020"  # scripted group (container) (typed FeaturePython)
  n = 1
  ref = N_element
FEATURE [App::DocumentObjectGroupPython] O_element102  label="O_element : 056"  # scripted group (container) (typed FeaturePython)
  n = 2
  ref = O_element
FEATURE [App::DocumentObjectGroupPython] G4_VALINE  # scripted group (container) (typed FeaturePython)
  Dunit = g/cm3
  Dvalue = 1.23
  Group = -> [C_element120,H_element108,N_element047,O_element102]
  conduct = 2
  density = 1
  expand = 3
  formula = G4_VALINE
  name = G4_VALINE
  specific = 4
FEATURE [App::DocumentObjectGroupPython] H_element109  label="H_element : 0.009"  # scripted group (container) (typed FeaturePython)
  n = 0.009417
FEATURE [App::DocumentObjectGroupPython] C_element121  label="C_element : 0.281"  # scripted group (container) (typed FeaturePython)
  n = 0.280555
FEATURE [App::DocumentObjectGroupPython] F_element018  label="F_element : 0.710"  # scripted group (container) (typed FeaturePython)
  n = 0.710028
FEATURE [App::DocumentObjectGroupPython] G4_VITON  # scripted group (container) (typed FeaturePython)
  Dunit = g/cm3
  Dvalue = 1.8
  Group = -> [H_element109,C_element121,F_element018]
  conduct = 2
  density = 1
  expand = 3
  formula = G4_VITON
  name = G4_VITON
  specific = 4
FEATURE [App::DocumentObjectGroupPython] H_element110  label="H_element : 059"  # scripted group (container) (typed FeaturePython)
  n = 2
  ref = H_element
FEATURE [App::DocumentObjectGroupPython] O_element103  label="O_element : 057"  # scripted group (container) (typed FeaturePython)
  n = 1
  ref = O_element
FEATURE [App::DocumentObjectGroupPython] G4_WATER  # scripted group (container) (typed FeaturePython)
  Dunit = g/cm3
  Dvalue = 1
  Group = -> [H_element110,O_element103]
  conduct = 2
  density = 1
  expand = 3
  formula = G4_WATER
  name = G4_WATER
  specific = 4
FEATURE [App::DocumentObjectGroupPython] H_element111  label="H_element : 060"  # scripted group (container) (typed FeaturePython)
  n = 2
  ref = H_element
FEATURE [App::DocumentObjectGroupPython] O_element104  label="O_element : 058"  # scripted group (container) (typed FeaturePython)
  n = 1
  ref = O_element
FEATURE [App::DocumentObjectGroupPython] G4_WATER_VAPOR  # scripted group (container) (typed FeaturePython)
  Dunit = g/cm3
  Dvalue = 0.000756182
  Group = -> [H_element111,O_element104]
  conduct = 2
  density = 1
  expand = 3
  formula = G4_WATER_VAPOR
  name = G4_WATER_VAPOR
  specific = 4
FEATURE [App::DocumentObjectGroupPython] C_element122  label="C_element : 068"  # scripted group (container) (typed FeaturePython)
  n = 8
  ref = C_element
FEATURE [App::DocumentObjectGroupPython] H_element112  label="H_element : 061"  # scripted group (container) (typed FeaturePython)
  n = 10
  ref = H_element
FEATURE [App::DocumentObjectGroupPython] G4_XYLENE  # scripted group (container) (typed FeaturePython)
  Dunit = g/cm3
  Dvalue = 0.87
  Group = -> [C_element122,H_element112]
  conduct = 2
  density = 1
  expand = 3
  formula = G4_XYLENE
  name = G4_XYLENE
  specific = 4
FEATURE [App::DocumentObjectGroupPython] C_element123  label="C_element : 069"  # scripted group (container) (typed FeaturePython)
  n = 1
  ref = C_element
FEATURE [App::DocumentObjectGroupPython] G4_GRAPHITE  # scripted group (container) (typed FeaturePython)
  Dunit = g/cm3
  Dvalue = 2.21
  Group = -> [C_element123]
  conduct = 2
  density = 1
  expand = 3
  formula = G4_GRAPHITE
  name = G4_GRAPHITE
  specific = 4
FEATURE [App::DocumentObjectGroupPython] NIST  # scripted group (container) (typed FeaturePython)
  Group = -> [G4_A_150_TISSUE,G4_ACETONE,G4_ACETYLENE,G4_ADENINE,G4_ADIPOSE_TISSUE_ICRP,G4_AIR,G4_ALANINE,G4_ALUMINUM_OXIDE,G4_AMBER,G4_AMMONIA,G4_ANILINE,G4_ANTHRACENE,G4_B_100_BONE,G4_BAKELITE,G4_BARIUM_FLUORIDE,G4_BARIUM_SULFATE,G4_BENZENE,G4_BERYLLIUM_OXIDE,G4_BGO,G4_BLOOD_ICRP,G4_BONE_COMPACT_ICRU,G4_BONE_CORTICAL_ICRP,G4_BORON_CARBIDE,G4_BORON_OXIDE,G4_BRAIN_ICRP,G4_BUTANE,G4_N_BUTYL_ALCOHOL,G4_C_552,+152 more]
FEATURE [App::DocumentObjectGroupPython] H_element113  label="H_element : 062"  # scripted group (container) (typed FeaturePython)
  n = 1
  ref = H_element
FEATURE [App::DocumentObjectGroupPython] G4_H  # scripted group (container) (typed FeaturePython)
  Dunit = g/cm3
  Dvalue = 8.3748e-05
  Group = -> [H_element113]
  conduct = 2
  density = 1
  expand = 3
  formula = H
  name = G4_H
  specific = 4
FEATURE [App::DocumentObjectGroupPython] He_element001  label="He_element : 1"  # scripted group (container) (typed FeaturePython)
  n = 1
  ref = He_element
FEATURE [App::DocumentObjectGroupPython] G4_He  # scripted group (container) (typed FeaturePython)
  Dunit = g/cm3
  Dvalue = 0.000166322
  Group = -> [He_element001]
  conduct = 2
  density = 1
  expand = 3
  formula = He
  name = G4_He
  specific = 4
FEATURE [App::DocumentObjectGroupPython] Li_element008  label="Li_element : 008"  # scripted group (container) (typed FeaturePython)
  n = 1
  ref = Li_element
FEATURE [App::DocumentObjectGroupPython] G4_Li  # scripted group (container) (typed FeaturePython)
  Dunit = g/cm3
  Dvalue = 0.534
  Group = -> [Li_element008]
  conduct = 2
  density = 1
  expand = 3
  formula = Li
  name = G4_Li
  specific = 4
FEATURE [App::DocumentObjectGroupPython] Be_element002  label="Be_element : 002"  # scripted group (container) (typed FeaturePython)
  n = 1
  ref = Be_element
FEATURE [App::DocumentObjectGroupPython] G4_Be  # scripted group (container) (typed FeaturePython)
  Dunit = g/cm3
  Dvalue = 1.848
  Group = -> [Be_element002]
  conduct = 2
  density = 1
  expand = 3
  formula = Be
  name = G4_Be
  specific = 4
FEATURE [App::DocumentObjectGroupPython] B_element007  label="B_element : 007"  # scripted group (container) (typed FeaturePython)
  n = 1
  ref = B_element
FEATURE [App::DocumentObjectGroupPython] G4_B  # scripted group (container) (typed FeaturePython)
  Dunit = g/cm3
  Dvalue = 2.37
  Group = -> [B_element007]
  conduct = 2
  density = 1
  expand = 3
  formula = B
  name = G4_B
  specific = 4
FEATURE [App::DocumentObjectGroupPython] C_element124  label="C_element : 070"  # scripted group (container) (typed FeaturePython)
  n = 1
  ref = C_element
FEATURE [App::DocumentObjectGroupPython] G4_C  # scripted group (container) (typed FeaturePython)
  Dunit = g/cm3
  Dvalue = 2
  Group = -> [C_element124]
  conduct = 2
  density = 1
  expand = 3
  formula = C
  name = G4_C
  specific = 4
FEATURE [App::DocumentObjectGroupPython] N_element048  label="N_element : 021"  # scripted group (container) (typed FeaturePython)
  n = 1
  ref = N_element
FEATURE [App::DocumentObjectGroupPython] G4_N  # scripted group (container) (typed FeaturePython)
  Dunit = g/cm3
  Dvalue = 0.0011652
  Group = -> [N_element048]
  conduct = 2
  density = 1
  expand = 3
  formula = N
  name = G4_N
  specific = 4
FEATURE [App::DocumentObjectGroupPython] O_element105  label="O_element : 059"  # scripted group (container) (typed FeaturePython)
  n = 1
  ref = O_element
FEATURE [App::DocumentObjectGroupPython] G4_O  # scripted group (container) (typed FeaturePython)
  Dunit = g/cm3
  Dvalue = 0.00133151
  Group = -> [O_element105]
  conduct = 2
  density = 1
  expand = 3
  formula = O
  name = G4_O
  specific = 4
FEATURE [App::DocumentObjectGroupPython] F_element019  label="F_element : 008"  # scripted group (container) (typed FeaturePython)
  n = 1
  ref = F_element
FEATURE [App::DocumentObjectGroupPython] G4_F  # scripted group (container) (typed FeaturePython)
  Dunit = g/cm3
  Dvalue = 0.00158029
  Group = -> [F_element019]
  conduct = 2
  density = 1
  expand = 3
  formula = F
  name = G4_F
  specific = 4
FEATURE [App::DocumentObjectGroupPython] Ne_element001  label="Ne_element : 1"  # scripted group (container) (typed FeaturePython)
  n = 1
  ref = Ne_element
FEATURE [App::DocumentObjectGroupPython] G4_Ne  # scripted group (container) (typed FeaturePython)
  Dunit = g/cm3
  Dvalue = 0.000838505
  Group = -> [Ne_element001]
  conduct = 2
  density = 1
  expand = 3
  formula = Ne
  name = G4_Ne
  specific = 4
FEATURE [App::DocumentObjectGroupPython] Na_element020  label="Na_element : 005"  # scripted group (container) (typed FeaturePython)
  n = 1
  ref = Na_element
FEATURE [App::DocumentObjectGroupPython] G4_Na  # scripted group (container) (typed FeaturePython)
  Dunit = g/cm3
  Dvalue = 0.971
  Group = -> [Na_element020]
  conduct = 2
  density = 1
  expand = 3
  formula = Na
  name = G4_Na
  specific = 4
FEATURE [App::DocumentObjectGroupPython] Mg_element011  label="Mg_element : 005"  # scripted group (container) (typed FeaturePython)
  n = 1
  ref = Mg_element
FEATURE [App::DocumentObjectGroupPython] G4_Mg  # scripted group (container) (typed FeaturePython)
  Dunit = g/cm3
  Dvalue = 1.74
  Group = -> [Mg_element011]
  conduct = 2
  density = 1
  expand = 3
  formula = Mg
  name = G4_Mg
  specific = 4
FEATURE [App::DocumentObjectGroupPython] Al_element004  label="Al_element : 1"  # scripted group (container) (typed FeaturePython)
  n = 1
  ref = Al_element
FEATURE [App::DocumentObjectGroupPython] G4_Al  # scripted group (container) (typed FeaturePython)
  Dunit = g/cm3
  Dvalue = 2.699
  Group = -> [Al_element004]
  conduct = 2
  density = 1
  expand = 3
  formula = Al
  name = G4_Al
  specific = 4
FEATURE [App::DocumentObjectGroupPython] Si_element007  label="Si_element : 002"  # scripted group (container) (typed FeaturePython)
  n = 1
  ref = Si_element
FEATURE [App::DocumentObjectGroupPython] G4_Si  # scripted group (container) (typed FeaturePython)
  Dunit = g/cm3
  Dvalue = 2.33
  Group = -> [Si_element007]
  conduct = 2
  density = 1
  expand = 3
  formula = Si
  name = G4_Si
  specific = 4
FEATURE [App::DocumentObjectGroupPython] P_element013  label="P_element : 002"  # scripted group (container) (typed FeaturePython)
  n = 1
  ref = P_element
FEATURE [App::DocumentObjectGroupPython] G4_P  # scripted group (container) (typed FeaturePython)
  Dunit = g/cm3
  Dvalue = 2.2
  Group = -> [P_element013]
  conduct = 2
  density = 1
  expand = 3
  formula = P
  name = G4_P
  specific = 4
FEATURE [App::DocumentObjectGroupPython] S_element023  label="S_element : 007"  # scripted group (container) (typed FeaturePython)
  n = 1
  ref = S_element
FEATURE [App::DocumentObjectGroupPython] G4_S  # scripted group (container) (typed FeaturePython)
  Dunit = g/cm3
  Dvalue = 2
  Group = -> [S_element023]
  conduct = 2
  density = 1
  expand = 3
  formula = S
  name = G4_S
  specific = 4
FEATURE [App::DocumentObjectGroupPython] Cl_element029  label="Cl_element : 015"  # scripted group (container) (typed FeaturePython)
  n = 1
  ref = Cl_element
FEATURE [App::DocumentObjectGroupPython] G4_Cl  # scripted group (container) (typed FeaturePython)
  Dunit = g/cm3
  Dvalue = 0.00299473
  Group = -> [Cl_element029]
  conduct = 2
  density = 1
  expand = 3
  formula = Cl
  name = G4_Cl
  specific = 4
FEATURE [App::DocumentObjectGroupPython] Ar_element002  label="Ar_element : 1"  # scripted group (container) (typed FeaturePython)
  n = 1
  ref = Ar_element
FEATURE [App::DocumentObjectGroupPython] G4_Ar  # scripted group (container) (typed FeaturePython)
  Dunit = g/cm3
  Dvalue = 0.00166201
  Group = -> [Ar_element002]
  conduct = 2
  density = 1
  expand = 3
  formula = Ar
  name = G4_Ar
  specific = 4
FEATURE [App::DocumentObjectGroupPython] K_element013  label="K_element : 003"  # scripted group (container) (typed FeaturePython)
  n = 1
  ref = K_element
FEATURE [App::DocumentObjectGroupPython] G4_K  # scripted group (container) (typed FeaturePython)
  Dunit = g/cm3
  Dvalue = 0.862
  Group = -> [K_element013]
  conduct = 2
  density = 1
  expand = 3
  formula = K
  name = G4_K
  specific = 4
FEATURE [App::DocumentObjectGroupPython] Ca_element014  label="Ca_element : 007"  # scripted group (container) (typed FeaturePython)
  n = 1
  ref = Ca_element
FEATURE [App::DocumentObjectGroupPython] G4_Ca  # scripted group (container) (typed FeaturePython)
  Dunit = g/cm3
  Dvalue = 1.55
  Group = -> [Ca_element014]
  conduct = 2
  density = 1
  expand = 3
  formula = Ca
  name = G4_Ca
  specific = 4
FEATURE [App::DocumentObjectGroupPython] Sc_element001  label="Sc_element : 1"  # scripted group (container) (typed FeaturePython)
  n = 1
  ref = Sc_element
FEATURE [App::DocumentObjectGroupPython] G4_Sc  # scripted group (container) (typed FeaturePython)
  Dunit = g/cm3
  Dvalue = 2.989
  Group = -> [Sc_element001]
  conduct = 2
  density = 1
  expand = 3
  formula = Sc
  name = G4_Sc
  specific = 4
FEATURE [App::DocumentObjectGroupPython] Ti_element004  label="Ti_element : 002"  # scripted group (container) (typed FeaturePython)
  n = 1
  ref = Ti_element
FEATURE [App::DocumentObjectGroupPython] G4_Ti  # scripted group (container) (typed FeaturePython)
  Dunit = g/cm3
  Dvalue = 4.54
  Group = -> [Ti_element004]
  conduct = 2
  density = 1
  expand = 3
  formula = Ti
  name = G4_Ti
  specific = 4
FEATURE [App::DocumentObjectGroupPython] V_element001  label="V_element : 1"  # scripted group (container) (typed FeaturePython)
  n = 1
  ref = V_element
FEATURE [App::DocumentObjectGroupPython] G4_V  # scripted group (container) (typed FeaturePython)
  Dunit = g/cm3
  Dvalue = 6.11
  Group = -> [V_element001]
  conduct = 2
  density = 1
  expand = 3
  formula = V
  name = G4_V
  specific = 4
FEATURE [App::DocumentObjectGroupPython] Cr_element001  label="Cr_element : 1"  # scripted group (container) (typed FeaturePython)
  n = 1
  ref = Cr_element
FEATURE [App::DocumentObjectGroupPython] G4_Cr  # scripted group (container) (typed FeaturePython)
  Dunit = g/cm3
  Dvalue = 7.18
  Group = -> [Cr_element001]
  conduct = 2
  density = 1
  expand = 3
  formula = Cr
  name = G4_Cr
  specific = 4
FEATURE [App::DocumentObjectGroupPython] Mn_element001  label="Mn_element : 1"  # scripted group (container) (typed FeaturePython)
  n = 1
  ref = Mn_element
FEATURE [App::DocumentObjectGroupPython] G4_Mn  # scripted group (container) (typed FeaturePython)
  Dunit = g/cm3
  Dvalue = 7.44
  Group = -> [Mn_element001]
  conduct = 2
  density = 1
  expand = 3
  formula = Mn
  name = G4_Mn
  specific = 4
FEATURE [App::DocumentObjectGroupPython] Fe_element007  label="Fe_element : 004"  # scripted group (container) (typed FeaturePython)
  n = 1
  ref = Fe_element
FEATURE [App::DocumentObjectGroupPython] G4_Fe  # scripted group (container) (typed FeaturePython)
  Dunit = g/cm3
  Dvalue = 7.874
  Group = -> [Fe_element007]
  conduct = 2
  density = 1
  expand = 3
  formula = Fe
  name = G4_Fe
  specific = 4
FEATURE [App::DocumentObjectGroupPython] Co_element001  label="Co_element : 1"  # scripted group (container) (typed FeaturePython)
  n = 1
  ref = Co_element
FEATURE [App::DocumentObjectGroupPython] G4_Co  # scripted group (container) (typed FeaturePython)
  Dunit = g/cm3
  Dvalue = 8.9
  Group = -> [Co_element001]
  conduct = 2
  density = 1
  expand = 3
  formula = Co
  name = G4_Co
  specific = 4
FEATURE [App::DocumentObjectGroupPython] Ni_element001  label="Ni_element : 1"  # scripted group (container) (typed FeaturePython)
  n = 1
  ref = Ni_element
FEATURE [App::DocumentObjectGroupPython] G4_Ni  # scripted group (container) (typed FeaturePython)
  Dunit = g/cm3
  Dvalue = 8.902
  Group = -> [Ni_element001]
  conduct = 2
  density = 1
  expand = 3
  formula = Ni
  name = G4_Ni
  specific = 4
FEATURE [App::DocumentObjectGroupPython] Cu_element001  label="Cu_element : 1"  # scripted group (container) (typed FeaturePython)
  n = 1
  ref = Cu_element
FEATURE [App::DocumentObjectGroupPython] G4_Cu  # scripted group (container) (typed FeaturePython)
  Dunit = g/cm3
  Dvalue = 8.96
  Group = -> [Cu_element001]
  conduct = 2
  density = 1
  expand = 3
  formula = Cu
  name = G4_Cu
  specific = 4
FEATURE [App::DocumentObjectGroupPython] Zn_element001  label="Zn_element : 1"  # scripted group (container) (typed FeaturePython)
  n = 1
  ref = Zn_element
FEATURE [App::DocumentObjectGroupPython] G4_Zn  # scripted group (container) (typed FeaturePython)
  Dunit = g/cm3
  Dvalue = 7.133
  Group = -> [Zn_element001]
  conduct = 2
  density = 1
  expand = 3
  formula = Zn
  name = G4_Zn
  specific = 4
FEATURE [App::DocumentObjectGroupPython] Ga_element002  label="Ga_element : 002"  # scripted group (container) (typed FeaturePython)
  n = 1
  ref = Ga_element
FEATURE [App::DocumentObjectGroupPython] G4_Ga  # scripted group (container) (typed FeaturePython)
  Dunit = g/cm3
  Dvalue = 5.904
  Group = -> [Ga_element002]
  conduct = 2
  density = 1
  expand = 3
  formula = Ga
  name = G4_Ga
  specific = 4
FEATURE [App::DocumentObjectGroupPython] Ge_element002  label="Ge_element : 1"  # scripted group (container) (typed FeaturePython)
  n = 1
  ref = Ge_element
FEATURE [App::DocumentObjectGroupPython] G4_Ge  # scripted group (container) (typed FeaturePython)
  Dunit = g/cm3
  Dvalue = 5.323
  Group = -> [Ge_element002]
  conduct = 2
  density = 1
  expand = 3
  formula = Ge
  name = G4_Ge
  specific = 4
FEATURE [App::DocumentObjectGroupPython] As_element003  label="As_element : 002"  # scripted group (container) (typed FeaturePython)
  n = 1
  ref = As_element
FEATURE [App::DocumentObjectGroupPython] G4_As  # scripted group (container) (typed FeaturePython)
  Dunit = g/cm3
  Dvalue = 5.73
  Group = -> [As_element003]
  conduct = 2
  density = 1
  expand = 3
  formula = As
  name = G4_As
  specific = 4
FEATURE [App::DocumentObjectGroupPython] Se_element001  label="Se_element : 1"  # scripted group (container) (typed FeaturePython)
  n = 1
  ref = Se_element
FEATURE [App::DocumentObjectGroupPython] G4_Se  # scripted group (container) (typed FeaturePython)
  Dunit = g/cm3
  Dvalue = 4.5
  Group = -> [Se_element001]
  conduct = 2
  density = 1
  expand = 3
  formula = Se
  name = G4_Se
  specific = 4
FEATURE [App::DocumentObjectGroupPython] Br_element007  label="Br_element : 004"  # scripted group (container) (typed FeaturePython)
  n = 1
  ref = Br_element
FEATURE [App::DocumentObjectGroupPython] G4_Br  # scripted group (container) (typed FeaturePython)
  Dunit = g/cm3
  Dvalue = 0.0070721
  Group = -> [Br_element007]
  conduct = 2
  density = 1
  expand = 3
  formula = Br
  name = G4_Br
  specific = 4
FEATURE [App::DocumentObjectGroupPython] Kr_element001  label="Kr_element : 1"  # scripted group (container) (typed FeaturePython)
  n = 1
  ref = Kr_element
FEATURE [App::DocumentObjectGroupPython] G4_Kr  # scripted group (container) (typed FeaturePython)
  Dunit = g/cm3
  Dvalue = 0.00347832
  Group = -> [Kr_element001]
  conduct = 2
  density = 1
  expand = 3
  formula = Kr
  name = G4_Kr
  specific = 4
FEATURE [App::DocumentObjectGroupPython] Rb_element001  label="Rb_element : 1"  # scripted group (container) (typed FeaturePython)
  n = 1
  ref = Rb_element
FEATURE [App::DocumentObjectGroupPython] G4_Rb  # scripted group (container) (typed FeaturePython)
  Dunit = g/cm3
  Dvalue = 1.532
  Group = -> [Rb_element001]
  conduct = 2
  density = 1
  expand = 3
  formula = Rb
  name = G4_Rb
  specific = 4
FEATURE [App::DocumentObjectGroupPython] Sr_element001  label="Sr_element : 1"  # scripted group (container) (typed FeaturePython)
  n = 1
  ref = Sr_element
FEATURE [App::DocumentObjectGroupPython] G4_Sr  # scripted group (container) (typed FeaturePython)
  Dunit = g/cm3
  Dvalue = 2.54
  Group = -> [Sr_element001]
  conduct = 2
  density = 1
  expand = 3
  formula = Sr
  name = G4_Sr
  specific = 4
FEATURE [App::DocumentObjectGroupPython] Y_element001  label="Y_element : 1"  # scripted group (container) (typed FeaturePython)
  n = 1
  ref = Y_element
FEATURE [App::DocumentObjectGroupPython] G4_Y  # scripted group (container) (typed FeaturePython)
  Dunit = g/cm3
  Dvalue = 4.469
  Group = -> [Y_element001]
  conduct = 2
  density = 1
  expand = 3
  formula = Y
  name = G4_Y
  specific = 4
FEATURE [App::DocumentObjectGroupPython] Zr_element001  label="Zr_element : 1"  # scripted group (container) (typed FeaturePython)
  n = 1
  ref = Zr_element
FEATURE [App::DocumentObjectGroupPython] G4_Zr  # scripted group (container) (typed FeaturePython)
  Dunit = g/cm3
  Dvalue = 6.506
  Group = -> [Zr_element001]
  conduct = 2
  density = 1
  expand = 3
  formula = Zr
  name = G4_Zr
  specific = 4
FEATURE [App::DocumentObjectGroupPython] Nb_element001  label="Nb_element : 1"  # scripted group (container) (typed FeaturePython)
  n = 1
  ref = Nb_element
FEATURE [App::DocumentObjectGroupPython] G4_Nb  # scripted group (container) (typed FeaturePython)
  Dunit = g/cm3
  Dvalue = 8.57
  Group = -> [Nb_element001]
  conduct = 2
  density = 1
  expand = 3
  formula = Nb
  name = G4_Nb
  specific = 4
FEATURE [App::DocumentObjectGroupPython] Mo_element001  label="Mo_element : 1"  # scripted group (container) (typed FeaturePython)
  n = 1
  ref = Mo_element
FEATURE [App::DocumentObjectGroupPython] G4_Mo  # scripted group (container) (typed FeaturePython)
  Dunit = g/cm3
  Dvalue = 10.22
  Group = -> [Mo_element001]
  conduct = 2
  density = 1
  expand = 3
  formula = Mo
  name = G4_Mo
  specific = 4
FEATURE [App::DocumentObjectGroupPython] Tc_element001  label="Tc_element : 1"  # scripted group (container) (typed FeaturePython)
  n = 1
  ref = Tc_element
FEATURE [App::DocumentObjectGroupPython] G4_Tc  # scripted group (container) (typed FeaturePython)
  Dunit = g/cm3
  Dvalue = 11.5
  Group = -> [Tc_element001]
  conduct = 2
  density = 1
  expand = 3
  formula = Tc
  name = G4_Tc
  specific = 4
FEATURE [App::DocumentObjectGroupPython] Ru_element001  label="Ru_element : 1"  # scripted group (container) (typed FeaturePython)
  n = 1
  ref = Ru_element
FEATURE [App::DocumentObjectGroupPython] G4_Ru  # scripted group (container) (typed FeaturePython)
  Dunit = g/cm3
  Dvalue = 12.41
  Group = -> [Ru_element001]
  conduct = 2
  density = 1
  expand = 3
  formula = Ru
  name = G4_Ru
  specific = 4
FEATURE [App::DocumentObjectGroupPython] Rh_element001  label="Rh_element : 1"  # scripted group (container) (typed FeaturePython)
  n = 1
  ref = Rh_element
FEATURE [App::DocumentObjectGroupPython] G4_Rh  # scripted group (container) (typed FeaturePython)
  Dunit = g/cm3
  Dvalue = 12.41
  Group = -> [Rh_element001]
  conduct = 2
  density = 1
  expand = 3
  formula = Rh
  name = G4_Rh
  specific = 4
FEATURE [App::DocumentObjectGroupPython] Pd_element001  label="Pd_element : 1"  # scripted group (container) (typed FeaturePython)
  n = 1
  ref = Pd_element
FEATURE [App::DocumentObjectGroupPython] G4_Pd  # scripted group (container) (typed FeaturePython)
  Dunit = g/cm3
  Dvalue = 12.02
  Group = -> [Pd_element001]
  conduct = 2
  density = 1
  expand = 3
  formula = Pd
  name = G4_Pd
  specific = 4
FEATURE [App::DocumentObjectGroupPython] Ag_element006  label="Ag_element : 004"  # scripted group (container) (typed FeaturePython)
  n = 1
  ref = Ag_element
FEATURE [App::DocumentObjectGroupPython] G4_Ag  # scripted group (container) (typed FeaturePython)
  Dunit = g/cm3
  Dvalue = 10.5
  Group = -> [Ag_element006]
  conduct = 2
  density = 1
  expand = 3
  formula = Ag
  name = G4_Ag
  specific = 4
FEATURE [App::DocumentObjectGroupPython] Cd_element003  label="Cd_element : 003"  # scripted group (container) (typed FeaturePython)
  n = 1
  ref = Cd_element
FEATURE [App::DocumentObjectGroupPython] G4_Cd  # scripted group (container) (typed FeaturePython)
  Dunit = g/cm3
  Dvalue = 8.65
  Group = -> [Cd_element003]
  conduct = 2
  density = 1
  expand = 3
  formula = Cd
  name = G4_Cd
  specific = 4
FEATURE [App::DocumentObjectGroupPython] In_element001  label="In_element : 1"  # scripted group (container) (typed FeaturePython)
  n = 1
  ref = In_element
FEATURE [App::DocumentObjectGroupPython] G4_In  # scripted group (container) (typed FeaturePython)
  Dunit = g/cm3
  Dvalue = 7.31
  Group = -> [In_element001]
  conduct = 2
  density = 1
  expand = 3
  formula = In
  name = G4_In
  specific = 4
FEATURE [App::DocumentObjectGroupPython] Sn_element001  label="Sn_element : 1"  # scripted group (container) (typed FeaturePython)
  n = 1
  ref = Sn_element
FEATURE [App::DocumentObjectGroupPython] G4_Sn  # scripted group (container) (typed FeaturePython)
  Dunit = g/cm3
  Dvalue = 7.31
  Group = -> [Sn_element001]
  conduct = 2
  density = 1
  expand = 3
  formula = Sn
  name = G4_Sn
  specific = 4
FEATURE [App::DocumentObjectGroupPython] Sb_element001  label="Sb_element : 1"  # scripted group (container) (typed FeaturePython)
  n = 1
  ref = Sb_element
FEATURE [App::DocumentObjectGroupPython] G4_Sb  # scripted group (container) (typed FeaturePython)
  Dunit = g/cm3
  Dvalue = 6.691
  Group = -> [Sb_element001]
  conduct = 2
  density = 1
  expand = 3
  formula = Sb
  name = G4_Sb
  specific = 4
FEATURE [App::DocumentObjectGroupPython] Te_element002  label="Te_element : 002"  # scripted group (container) (typed FeaturePython)
  n = 1
  ref = Te_element
FEATURE [App::DocumentObjectGroupPython] G4_Te  # scripted group (container) (typed FeaturePython)
  Dunit = g/cm3
  Dvalue = 6.24
  Group = -> [Te_element002]
  conduct = 2
  density = 1
  expand = 3
  formula = Te
  name = G4_Te
  specific = 4
FEATURE [App::DocumentObjectGroupPython] I_element010  label="I_element : 006"  # scripted group (container) (typed FeaturePython)
  n = 1
  ref = I_element
FEATURE [App::DocumentObjectGroupPython] G4_I  # scripted group (container) (typed FeaturePython)
  Dunit = g/cm3
  Dvalue = 4.93
  Group = -> [I_element010]
  conduct = 2
  density = 1
  expand = 3
  formula = I
  name = G4_I
  specific = 4
FEATURE [App::DocumentObjectGroupPython] Xe_element001  label="Xe_element : 1"  # scripted group (container) (typed FeaturePython)
  n = 1
  ref = Xe_element
FEATURE [App::DocumentObjectGroupPython] G4_Xe  # scripted group (container) (typed FeaturePython)
  Dunit = g/cm3
  Dvalue = 0.00548536
  Group = -> [Xe_element001]
  conduct = 2
  density = 1
  expand = 3
  formula = Xe
  name = G4_Xe
  specific = 4
FEATURE [App::DocumentObjectGroupPython] Cs_element003  label="Cs_element : 003"  # scripted group (container) (typed FeaturePython)
  n = 1
  ref = Cs_element
FEATURE [App::DocumentObjectGroupPython] G4_Cs  # scripted group (container) (typed FeaturePython)
  Dunit = g/cm3
  Dvalue = 1.873
  Group = -> [Cs_element003]
  conduct = 2
  density = 1
  expand = 3
  formula = Cs
  name = G4_Cs
  specific = 4
FEATURE [App::DocumentObjectGroupPython] Ba_element003  label="Ba_element : 003"  # scripted group (container) (typed FeaturePython)
  n = 1
  ref = Ba_element
FEATURE [App::DocumentObjectGroupPython] G4_Ba  # scripted group (container) (typed FeaturePython)
  Dunit = g/cm3
  Dvalue = 3.5
  Group = -> [Ba_element003]
  conduct = 2
  density = 1
  expand = 3
  formula = Ba
  name = G4_Ba
  specific = 4
FEATURE [App::DocumentObjectGroupPython] La_element003  label="La_element : 003"  # scripted group (container) (typed FeaturePython)
  n = 1
  ref = La_element
FEATURE [App::DocumentObjectGroupPython] G4_La  # scripted group (container) (typed FeaturePython)
  Dunit = g/cm3
  Dvalue = 6.154
  Group = -> [La_element003]
  conduct = 2
  density = 1
  expand = 3
  formula = La
  name = G4_La
  specific = 4
FEATURE [App::DocumentObjectGroupPython] Ce_element002  label="Ce_element : 1"  # scripted group (container) (typed FeaturePython)
  n = 1
  ref = Ce_element
FEATURE [App::DocumentObjectGroupPython] G4_Ce  # scripted group (container) (typed FeaturePython)
  Dunit = g/cm3
  Dvalue = 6.657
  Group = -> [Ce_element002]
  conduct = 2
  density = 1
  expand = 3
  formula = Ce
  name = G4_Ce
  specific = 4
FEATURE [App::DocumentObjectGroupPython] Pr_element001  label="Pr_element : 1"  # scripted group (container) (typed FeaturePython)
  n = 1
  ref = Pr_element
FEATURE [App::DocumentObjectGroupPython] G4_Pr  # scripted group (container) (typed FeaturePython)
  Dunit = g/cm3
  Dvalue = 6.71
  Group = -> [Pr_element001]
  conduct = 2
  density = 1
  expand = 3
  formula = Pr
  name = G4_Pr
  specific = 4
FEATURE [App::DocumentObjectGroupPython] Nd_element001  label="Nd_element : 1"  # scripted group (container) (typed FeaturePython)
  n = 1
  ref = Nd_element
FEATURE [App::DocumentObjectGroupPython] G4_Nd  # scripted group (container) (typed FeaturePython)
  Dunit = g/cm3
  Dvalue = 6.9
  Group = -> [Nd_element001]
  conduct = 2
  density = 1
  expand = 3
  formula = Nd
  name = G4_Nd
  specific = 4
FEATURE [App::DocumentObjectGroupPython] Pm_element001  label="Pm_element : 1"  # scripted group (container) (typed FeaturePython)
  n = 1
  ref = Pm_element
FEATURE [App::DocumentObjectGroupPython] G4_Pm  # scripted group (container) (typed FeaturePython)
  Dunit = g/cm3
  Dvalue = 7.22
  Group = -> [Pm_element001]
  conduct = 2
  density = 1
  expand = 3
  formula = Pm
  name = G4_Pm
  specific = 4
FEATURE [App::DocumentObjectGroupPython] Sm_element001  label="Sm_element : 1"  # scripted group (container) (typed FeaturePython)
  n = 1
  ref = Sm_element
FEATURE [App::DocumentObjectGroupPython] G4_Sm  # scripted group (container) (typed FeaturePython)
  Dunit = g/cm3
  Dvalue = 7.46
  Group = -> [Sm_element001]
  conduct = 2
  density = 1
  expand = 3
  formula = Sm
  name = G4_Sm
  specific = 4
FEATURE [App::DocumentObjectGroupPython] Eu_element001  label="Eu_element : 1"  # scripted group (container) (typed FeaturePython)
  n = 1
  ref = Eu_element
FEATURE [App::DocumentObjectGroupPython] G4_Eu  # scripted group (container) (typed FeaturePython)
  Dunit = g/cm3
  Dvalue = 5.243
  Group = -> [Eu_element001]
  conduct = 2
  density = 1
  expand = 3
  formula = Eu
  name = G4_Eu
  specific = 4
FEATURE [App::DocumentObjectGroupPython] Gd_element002  label="Gd_element : 1"  # scripted group (container) (typed FeaturePython)
  n = 1
  ref = Gd_element
FEATURE [App::DocumentObjectGroupPython] G4_Gd  # scripted group (container) (typed FeaturePython)
  Dunit = g/cm3
  Dvalue = 7.9004
  Group = -> [Gd_element002]
  conduct = 2
  density = 1
  expand = 3
  formula = Gd
  name = G4_Gd
  specific = 4
FEATURE [App::DocumentObjectGroupPython] Tb_element001  label="Tb_element : 1"  # scripted group (container) (typed FeaturePython)
  n = 1
  ref = Tb_element
FEATURE [App::DocumentObjectGroupPython] G4_Tb  # scripted group (container) (typed FeaturePython)
  Dunit = g/cm3
  Dvalue = 8.229
  Group = -> [Tb_element001]
  conduct = 2
  density = 1
  expand = 3
  formula = Tb
  name = G4_Tb
  specific = 4
FEATURE [App::DocumentObjectGroupPython] Dy_element001  label="Dy_element : 1"  # scripted group (container) (typed FeaturePython)
  n = 1
  ref = Dy_element
FEATURE [App::DocumentObjectGroupPython] G4_Dy  # scripted group (container) (typed FeaturePython)
  Dunit = g/cm3
  Dvalue = 8.55
  Group = -> [Dy_element001]
  conduct = 2
  density = 1
  expand = 3
  formula = Dy
  name = G4_Dy
  specific = 4
FEATURE [App::DocumentObjectGroupPython] Ho_element001  label="Ho_element : 1"  # scripted group (container) (typed FeaturePython)
  n = 1
  ref = Ho_element
FEATURE [App::DocumentObjectGroupPython] G4_Ho  # scripted group (container) (typed FeaturePython)
  Dunit = g/cm3
  Dvalue = 8.795
  Group = -> [Ho_element001]
  conduct = 2
  density = 1
  expand = 3
  formula = Ho
  name = G4_Ho
  specific = 4
FEATURE [App::DocumentObjectGroupPython] Er_element001  label="Er_element : 1"  # scripted group (container) (typed FeaturePython)
  n = 1
  ref = Er_element
FEATURE [App::DocumentObjectGroupPython] G4_Er  # scripted group (container) (typed FeaturePython)
  Dunit = g/cm3
  Dvalue = 9.066
  Group = -> [Er_element001]
  conduct = 2
  density = 1
  expand = 3
  formula = Er
  name = G4_Er
  specific = 4
FEATURE [App::DocumentObjectGroupPython] Tm_element001  label="Tm_element : 1"  # scripted group (container) (typed FeaturePython)
  n = 1
  ref = Tm_element
FEATURE [App::DocumentObjectGroupPython] G4_Tm  # scripted group (container) (typed FeaturePython)
  Dunit = g/cm3
  Dvalue = 9.321
  Group = -> [Tm_element001]
  conduct = 2
  density = 1
  expand = 3
  formula = Tm
  name = G4_Tm
  specific = 4
FEATURE [App::DocumentObjectGroupPython] Yb_element001  label="Yb_element : 1"  # scripted group (container) (typed FeaturePython)
  n = 1
  ref = Yb_element
FEATURE [App::DocumentObjectGroupPython] G4_Yb  # scripted group (container) (typed FeaturePython)
  Dunit = g/cm3
  Dvalue = 6.73
  Group = -> [Yb_element001]
  conduct = 2
  density = 1
  expand = 3
  formula = Yb
  name = G4_Yb
  specific = 4
FEATURE [App::DocumentObjectGroupPython] Lu_element001  label="Lu_element : 1"  # scripted group (container) (typed FeaturePython)
  n = 1
  ref = Lu_element
FEATURE [App::DocumentObjectGroupPython] G4_Lu  # scripted group (container) (typed FeaturePython)
  Dunit = g/cm3
  Dvalue = 9.84
  Group = -> [Lu_element001]
  conduct = 2
  density = 1
  expand = 3
  formula = Lu
  name = G4_Lu
  specific = 4
FEATURE [App::DocumentObjectGroupPython] Hf_element001  label="Hf_element : 1"  # scripted group (container) (typed FeaturePython)
  n = 1
  ref = Hf_element
FEATURE [App::DocumentObjectGroupPython] G4_Hf  # scripted group (container) (typed FeaturePython)
  Dunit = g/cm3
  Dvalue = 13.31
  Group = -> [Hf_element001]
  conduct = 2
  density = 1
  expand = 3
  formula = Hf
  name = G4_Hf
  specific = 4
FEATURE [App::DocumentObjectGroupPython] Ta_element001  label="Ta_element : 1"  # scripted group (container) (typed FeaturePython)
  n = 1
  ref = Ta_element
FEATURE [App::DocumentObjectGroupPython] G4_Ta  # scripted group (container) (typed FeaturePython)
  Dunit = g/cm3
  Dvalue = 16.654
  Group = -> [Ta_element001]
  conduct = 2
  density = 1
  expand = 3
  formula = Ta
  name = G4_Ta
  specific = 4
FEATURE [App::DocumentObjectGroupPython] W_element004  label="W_element : 004"  # scripted group (container) (typed FeaturePython)
  n = 1
  ref = W_element
FEATURE [App::DocumentObjectGroupPython] G4_W  # scripted group (container) (typed FeaturePython)
  Dunit = g/cm3
  Dvalue = 19.3
  Group = -> [W_element004]
  conduct = 2
  density = 1
  expand = 3
  formula = W
  name = G4_W
  specific = 4
FEATURE [App::DocumentObjectGroupPython] Re_element001  label="Re_element : 1"  # scripted group (container) (typed FeaturePython)
  n = 1
  ref = Re_element
FEATURE [App::DocumentObjectGroupPython] G4_Re  # scripted group (container) (typed FeaturePython)
  Dunit = g/cm3
  Dvalue = 21.02
  Group = -> [Re_element001]
  conduct = 2
  density = 1
  expand = 3
  formula = Re
  name = G4_Re
  specific = 4
FEATURE [App::DocumentObjectGroupPython] Os_element001  label="Os_element : 1"  # scripted group (container) (typed FeaturePython)
  n = 1
  ref = Os_element
FEATURE [App::DocumentObjectGroupPython] G4_Os  # scripted group (container) (typed FeaturePython)
  Dunit = g/cm3
  Dvalue = 22.57
  Group = -> [Os_element001]
  conduct = 2
  density = 1
  expand = 3
  formula = Os
  name = G4_Os
  specific = 4
FEATURE [App::DocumentObjectGroupPython] Ir_element001  label="Ir_element : 1"  # scripted group (container) (typed FeaturePython)
  n = 1
  ref = Ir_element
FEATURE [App::DocumentObjectGroupPython] G4_Ir  # scripted group (container) (typed FeaturePython)
  Dunit = g/cm3
  Dvalue = 22.42
  Group = -> [Ir_element001]
  conduct = 2
  density = 1
  expand = 3
  formula = Ir
  name = G4_Ir
  specific = 4
FEATURE [App::DocumentObjectGroupPython] Pt_element001  label="Pt_element : 1"  # scripted group (container) (typed FeaturePython)
  n = 1
  ref = Pt_element
FEATURE [App::DocumentObjectGroupPython] G4_Pt  # scripted group (container) (typed FeaturePython)
  Dunit = g/cm3
  Dvalue = 21.45
  Group = -> [Pt_element001]
  conduct = 2
  density = 1
  expand = 3
  formula = Pt
  name = G4_Pt
  specific = 4
FEATURE [App::DocumentObjectGroupPython] Au_element001  label="Au_element : 1"  # scripted group (container) (typed FeaturePython)
  n = 1
  ref = Au_element
FEATURE [App::DocumentObjectGroupPython] G4_Au  # scripted group (container) (typed FeaturePython)
  Dunit = g/cm3
  Dvalue = 19.32
  Group = -> [Au_element001]
  conduct = 2
  density = 1
  expand = 3
  formula = Au
  name = G4_Au
  specific = 4
FEATURE [App::DocumentObjectGroupPython] Hg_element002  label="Hg_element : 002"  # scripted group (container) (typed FeaturePython)
  n = 1
  ref = Hg_element
FEATURE [App::DocumentObjectGroupPython] G4_Hg  # scripted group (container) (typed FeaturePython)
  Dunit = g/cm3
  Dvalue = 13.546
  Group = -> [Hg_element002]
  conduct = 2
  density = 1
  expand = 3
  formula = Hg
  name = G4_Hg
  specific = 4
FEATURE [App::DocumentObjectGroupPython] Tl_element002  label="Tl_element : 002"  # scripted group (container) (typed FeaturePython)
  n = 1
  ref = Tl_element
FEATURE [App::DocumentObjectGroupPython] G4_Tl  # scripted group (container) (typed FeaturePython)
  Dunit = g/cm3
  Dvalue = 11.72
  Group = -> [Tl_element002]
  conduct = 2
  density = 1
  expand = 3
  formula = Tl
  name = G4_Tl
  specific = 4
FEATURE [App::DocumentObjectGroupPython] Pb_element003  label="Pb_element : 1"  # scripted group (container) (typed FeaturePython)
  n = 1
  ref = Pb_element
FEATURE [App::DocumentObjectGroupPython] G4_Pb  # scripted group (container) (typed FeaturePython)
  Dunit = g/cm3
  Dvalue = 11.35
  Group = -> [Pb_element003]
  conduct = 2
  density = 1
  expand = 3
  formula = Pb
  name = G4_Pb
  specific = 4
FEATURE [App::DocumentObjectGroupPython] Bi_element002  label="Bi_element : 1"  # scripted group (container) (typed FeaturePython)
  n = 1
  ref = Bi_element
FEATURE [App::DocumentObjectGroupPython] G4_Bi  # scripted group (container) (typed FeaturePython)
  Dunit = g/cm3
  Dvalue = 9.747
  Group = -> [Bi_element002]
  conduct = 2
  density = 1
  expand = 3
  formula = Bi
  name = G4_Bi
  specific = 4
FEATURE [App::DocumentObjectGroupPython] Po_element001  label="Po_element : 1"  # scripted group (container) (typed FeaturePython)
  n = 1
  ref = Po_element
FEATURE [App::DocumentObjectGroupPython] G4_Po  # scripted group (container) (typed FeaturePython)
  Dunit = g/cm3
  Dvalue = 9.32
  Group = -> [Po_element001]
  conduct = 2
  density = 1
  expand = 3
  formula = Po
  name = G4_Po
  specific = 4
FEATURE [App::DocumentObjectGroupPython] At_element001  label="At_element : 1"  # scripted group (container) (typed FeaturePython)
  n = 1
  ref = At_element
FEATURE [App::DocumentObjectGroupPython] G4_At  # scripted group (container) (typed FeaturePython)
  Dunit = g/cm3
  Dvalue = 9.32
  Group = -> [At_element001]
  conduct = 2
  density = 1
  expand = 3
  formula = At
  name = G4_At
  specific = 4
FEATURE [App::DocumentObjectGroupPython] Rn_element001  label="Rn_element : 1"  # scripted group (container) (typed FeaturePython)
  n = 1
  ref = Rn_element
FEATURE [App::DocumentObjectGroupPython] G4_Rn  # scripted group (container) (typed FeaturePython)
  Dunit = g/cm3
  Dvalue = 0.00900662
  Group = -> [Rn_element001]
  conduct = 2
  density = 1
  expand = 3
  formula = Rn
  name = G4_Rn
  specific = 4
FEATURE [App::DocumentObjectGroupPython] Fr_element001  label="Fr_element : 1"  # scripted group (container) (typed FeaturePython)
  n = 1
  ref = Fr_element
FEATURE [App::DocumentObjectGroupPython] G4_Fr  # scripted group (container) (typed FeaturePython)
  Dunit = g/cm3
  Dvalue = 1
  Group = -> [Fr_element001]
  conduct = 2
  density = 1
  expand = 3
  formula = Fr
  name = G4_Fr
  specific = 4
FEATURE [App::DocumentObjectGroupPython] Ra_element001  label="Ra_element : 1"  # scripted group (container) (typed FeaturePython)
  n = 1
  ref = Ra_element
FEATURE [App::DocumentObjectGroupPython] G4_Ra  # scripted group (container) (typed FeaturePython)
  Dunit = g/cm3
  Dvalue = 5
  Group = -> [Ra_element001]
  conduct = 2
  density = 1
  expand = 3
  formula = Ra
  name = G4_Ra
  specific = 4
FEATURE [App::DocumentObjectGroupPython] Ac_element001  label="Ac_element : 1"  # scripted group (container) (typed FeaturePython)
  n = 1
  ref = Ac_element
FEATURE [App::DocumentObjectGroupPython] G4_Ac  # scripted group (container) (typed FeaturePython)
  Dunit = g/cm3
  Dvalue = 10.07
  Group = -> [Ac_element001]
  conduct = 2
  density = 1
  expand = 3
  formula = Ac
  name = G4_Ac
  specific = 4
FEATURE [App::DocumentObjectGroupPython] Th_element001  label="Th_element : 1"  # scripted group (container) (typed FeaturePython)
  n = 1
  ref = Th_element
FEATURE [App::DocumentObjectGroupPython] G4_Th  # scripted group (container) (typed FeaturePython)
  Dunit = g/cm3
  Dvalue = 11.72
  Group = -> [Th_element001]
  conduct = 2
  density = 1
  expand = 3
  formula = Th
  name = G4_Th
  specific = 4
FEATURE [App::DocumentObjectGroupPython] Pa_element001  label="Pa_element : 1"  # scripted group (container) (typed FeaturePython)
  n = 1
  ref = Pa_element
FEATURE [App::DocumentObjectGroupPython] G4_Pa  # scripted group (container) (typed FeaturePython)
  Dunit = g/cm3
  Dvalue = 15.37
  Group = -> [Pa_element001]
  conduct = 2
  density = 1
  expand = 3
  formula = Pa
  name = G4_Pa
  specific = 4
FEATURE [App::DocumentObjectGroupPython] U_element004  label="U_element : 004"  # scripted group (container) (typed FeaturePython)
  n = 1
  ref = U_element
FEATURE [App::DocumentObjectGroupPython] G4_U  # scripted group (container) (typed FeaturePython)
  Dunit = g/cm3
  Dvalue = 18.95
  Group = -> [U_element004]
  conduct = 2
  density = 1
  expand = 3
  formula = U
  name = G4_U
  specific = 4
FEATURE [App::DocumentObjectGroupPython] Np_element001  label="Np_element : 1"  # scripted group (container) (typed FeaturePython)
  n = 1
  ref = Np_element
FEATURE [App::DocumentObjectGroupPython] G4_Np  # scripted group (container) (typed FeaturePython)
  Dunit = g/cm3
  Dvalue = 20.25
  Group = -> [Np_element001]
  conduct = 2
  density = 1
  expand = 3
  formula = Np
  name = G4_Np
  specific = 4
FEATURE [App::DocumentObjectGroupPython] Pu_element002  label="Pu_element : 002"  # scripted group (container) (typed FeaturePython)
  n = 1
  ref = Pu_element
FEATURE [App::DocumentObjectGroupPython] G4_Pu  # scripted group (container) (typed FeaturePython)
  Dunit = g/cm3
  Dvalue = 19.84
  Group = -> [Pu_element002]
  conduct = 2
  density = 1
  expand = 3
  formula = Pu
  name = G4_Pu
  specific = 4
FEATURE [App::DocumentObjectGroupPython] Am_element001  label="Am_element : 1"  # scripted group (container) (typed FeaturePython)
  n = 1
  ref = Am_element
FEATURE [App::DocumentObjectGroupPython] G4_Am  # scripted group (container) (typed FeaturePython)
  Dunit = g/cm3
  Dvalue = 13.67
  Group = -> [Am_element001]
  conduct = 2
  density = 1
  expand = 3
  formula = Am
  name = G4_Am
  specific = 4
FEATURE [App::DocumentObjectGroupPython] Cm_element001  label="Cm_element : 1"  # scripted group (container) (typed FeaturePython)
  n = 1
  ref = Cm_element
FEATURE [App::DocumentObjectGroupPython] G4_Cm  # scripted group (container) (typed FeaturePython)
  Dunit = g/cm3
  Dvalue = 13.51
  Group = -> [Cm_element001]
  conduct = 2
  density = 1
  expand = 3
  formula = Cm
  name = G4_Cm
  specific = 4
FEATURE [App::DocumentObjectGroupPython] Bk_element001  label="Bk_element : 1"  # scripted group (container) (typed FeaturePython)
  n = 1
  ref = Bk_element
FEATURE [App::DocumentObjectGroupPython] G4_Bk  # scripted group (container) (typed FeaturePython)
  Dunit = g/cm3
  Dvalue = 14
  Group = -> [Bk_element001]
  conduct = 2
  density = 1
  expand = 3
  formula = Bk
  name = G4_Bk
  specific = 4
FEATURE [App::DocumentObjectGroupPython] Cf_element001  label="Cf_element : 1"  # scripted group (container) (typed FeaturePython)
  n = 1
  ref = Cf_element
FEATURE [App::DocumentObjectGroupPython] G4_Cf  # scripted group (container) (typed FeaturePython)
  Dunit = g/cm3
  Dvalue = 10
  Group = -> [Cf_element001]
  conduct = 2
  density = 1
  expand = 3
  formula = Cf
  name = G4_Cf
  specific = 4
FEATURE [App::DocumentObjectGroupPython] Element  # scripted group (container) (typed FeaturePython)
  Group = -> [G4_H,G4_He,G4_Li,G4_Be,G4_B,G4_C,G4_N,G4_O,G4_F,G4_Ne,G4_Na,G4_Mg,G4_Al,G4_Si,G4_P,G4_S,G4_Cl,G4_Ar,G4_K,G4_Ca,G4_Sc,G4_Ti,G4_V,G4_Cr,G4_Mn,G4_Fe,G4_Co,G4_Ni,G4_Cu,G4_Zn,G4_Ga,G4_Ge,G4_As,G4_Se,G4_Br,G4_Kr,G4_Rb,G4_Sr,G4_Y,G4_Zr,G4_Nb,G4_Mo,G4_Tc,G4_Ru,G4_Rh,G4_Pd,G4_Ag,G4_Cd,G4_In,G4_Sn,G4_Sb,G4_Te,G4_I,G4_Xe,G4_Cs,G4_Ba,G4_La,G4_Ce,G4_Pr,G4_Nd,G4_Pm,G4_Sm,G4_Eu,G4_Gd,G4_Tb,G4_Dy,G4_Ho,G4_Er,+30 more]
FEATURE [App::DocumentObjectGroupPython] H_element114  label="H_element : 063"  # scripted group (container) (typed FeaturePython)
  n = 2
  ref = H_element
FEATURE [App::DocumentObjectGroupPython] G4_lH2  # scripted group (container) (typed FeaturePython)
  Dunit = g/cm3
  Dvalue = 0.0708
  Group = -> [H_element114]
  conduct = 2
  density = 1
  expand = 3
  formula = G4_lH2
  name = G4_lH2
  specific = 4
FEATURE [App::DocumentObjectGroupPython] N_element049  label="N_element : 022"  # scripted group (container) (typed FeaturePython)
  n = 2
  ref = N_element
FEATURE [App::DocumentObjectGroupPython] G4_lN2  # scripted group (container) (typed FeaturePython)
  Dunit = g/cm3
  Dvalue = 0.807
  Group = -> [N_element049]
  conduct = 2
  density = 1
  expand = 3
  formula = G4_lN2
  name = G4_lN2
  specific = 4
FEATURE [App::DocumentObjectGroupPython] O_element106  label="O_element : 060"  # scripted group (container) (typed FeaturePython)
  n = 2
  ref = O_element
FEATURE [App::DocumentObjectGroupPython] G4_lO2  # scripted group (container) (typed FeaturePython)
  Dunit = g/cm3
  Dvalue = 1.141
  Group = -> [O_element106]
  conduct = 2
  density = 1
  expand = 3
  formula = G4_lO2
  name = G4_lO2
  specific = 4
FEATURE [App::DocumentObjectGroupPython] Ar  label="Ar : 1"  # scripted group (container) (typed FeaturePython)
  n = 1
  ref = Ar
FEATURE [App::DocumentObjectGroupPython] G4_lAr  # scripted group (container) (typed FeaturePython)
  Dunit = g/cm3
  Dvalue = 1.396
  Group = -> [Ar]
  conduct = 2
  density = 1
  expand = 3
  formula = G4_lAr
  name = G4_lAr
  specific = 4
FEATURE [App::DocumentObjectGroupPython] Br  label="Br : 1"  # scripted group (container) (typed FeaturePython)
  n = 1
  ref = Br
FEATURE [App::DocumentObjectGroupPython] G4_lBr  # scripted group (container) (typed FeaturePython)
  Dunit = g/cm3
  Dvalue = 3.1028
  Group = -> [Br]
  conduct = 2
  density = 1
  expand = 3
  formula = G4_lBr
  name = G4_lBr
  specific = 4
FEATURE [App::DocumentObjectGroupPython] Kr  label="Kr : 1"  # scripted group (container) (typed FeaturePython)
  n = 1
  ref = Kr
FEATURE [App::DocumentObjectGroupPython] G4_lKr  # scripted group (container) (typed FeaturePython)
  Dunit = g/cm3
  Dvalue = 2.418
  Group = -> [Kr]
  conduct = 2
  density = 1
  expand = 3
  formula = G4_lKr
  name = G4_lKr
  specific = 4
FEATURE [App::DocumentObjectGroupPython] Xe  label="Xe : 1"  # scripted group (container) (typed FeaturePython)
  n = 1
  ref = Xe
FEATURE [App::DocumentObjectGroupPython] G4_lXe  # scripted group (container) (typed FeaturePython)
  Dunit = g/cm3
  Dvalue = 2.953
  Group = -> [Xe]
  conduct = 2
  density = 1
  expand = 3
  formula = G4_lXe
  name = G4_lXe
  specific = 4
FEATURE [App::DocumentObjectGroupPython] O_element107  label="O_element : 061"  # scripted group (container) (typed FeaturePython)
  n = 4
  ref = O_element
FEATURE [App::DocumentObjectGroupPython] Pb_element004  label="Pb_element : 002"  # scripted group (container) (typed FeaturePython)
  n = 1
  ref = Pb_element
FEATURE [App::DocumentObjectGroupPython] W_element005  label="W_element : 005"  # scripted group (container) (typed FeaturePython)
  n = 1
  ref = W_element
FEATURE [App::DocumentObjectGroupPython] G4_PbWO4  # scripted group (container) (typed FeaturePython)
  Dunit = g/cm3
  Dvalue = 8.28
  Group = -> [O_element107,Pb_element004,W_element005]
  conduct = 2
  density = 1
  expand = 3
  formula = G4_PbWO4
  name = G4_PbWO4
  specific = 4
FEATURE [App::DocumentObjectGroupPython] alactic  label="alactic : 1"  # scripted group (container) (typed FeaturePython)
  n = 1
  ref = alactic
FEATURE [App::DocumentObjectGroupPython] G4_Galactic  # scripted group (container) (typed FeaturePython)
  Dunit = g/cm3
  Dvalue = 0
  Group = -> [alactic]
  conduct = 2
  density = 1
  expand = 3
  formula = G4_Galactic
  name = G4_Galactic
  specific = 4
FEATURE [App::DocumentObjectGroupPython] RAPHITE_POROUS  label="RAPHITE_POROUS : 1"  # scripted group (container) (typed FeaturePython)
  n = 1
  ref = RAPHITE_POROUS
FEATURE [App::DocumentObjectGroupPython] G4_GRAPHITE_POROUS  # scripted group (container) (typed FeaturePython)
  Dunit = g/cm3
  Dvalue = 1.7
  Group = -> [RAPHITE_POROUS]
  conduct = 2
  density = 1
  expand = 3
  formula = G4_GRAPHITE_POROUS
  name = G4_GRAPHITE_POROUS
  specific = 4
FEATURE [App::DocumentObjectGroupPython] H_element115  label="H_element : 0.150"  # scripted group (container) (typed FeaturePython)
  n = 0.080538
FEATURE [App::DocumentObjectGroupPython] C_element125  label="C_element : 0.600"  # scripted group (container) (typed FeaturePython)
  n = 0.599848
FEATURE [App::DocumentObjectGroupPython] O_element108  label="O_element : 0.320"  # scripted group (container) (typed FeaturePython)
  n = 0.319614
FEATURE [App::DocumentObjectGroupPython] G4_LUCITE  # scripted group (container) (typed FeaturePython)
  Dunit = g/cm3
  Dvalue = 1.19
  Group = -> [H_element115,C_element125,O_element108]
  conduct = 2
  density = 1
  expand = 3
  formula = G4_LUCITE
  name = G4_LUCITE
  specific = 4
FEATURE [App::DocumentObjectGroupPython] Cu_element002  label="Cu_element : 62"  # scripted group (container) (typed FeaturePython)
  n = 62
  ref = Cu_element
FEATURE [App::DocumentObjectGroupPython] Zn_element002  label="Zn_element : 35"  # scripted group (container) (typed FeaturePython)
  n = 35
  ref = Zn_element
FEATURE [App::DocumentObjectGroupPython] Pb_element005  label="Pb_element : 3"  # scripted group (container) (typed FeaturePython)
  n = 3
  ref = Pb_element
FEATURE [App::DocumentObjectGroupPython] G4_BRASS  # scripted group (container) (typed FeaturePython)
  Dunit = g/cm3
  Dvalue = 8.52
  Group = -> [Cu_element002,Zn_element002,Pb_element005]
  conduct = 2
  density = 1
  expand = 3
  formula = G4_BRASS
  name = G4_BRASS
  specific = 4
FEATURE [App::DocumentObjectGroupPython] Cu_element003  label="Cu_element : 89"  # scripted group (container) (typed FeaturePython)
  n = 89
  ref = Cu_element
FEATURE [App::DocumentObjectGroupPython] Zn_element003  label="Zn_element : 9"  # scripted group (container) (typed FeaturePython)
  n = 9
  ref = Zn_element
FEATURE [App::DocumentObjectGroupPython] Pb_element006  label="Pb_element : 2"  # scripted group (container) (typed FeaturePython)
  n = 2
  ref = Pb_element
FEATURE [App::DocumentObjectGroupPython] G4_BRONZE  # scripted group (container) (typed FeaturePython)
  Dunit = g/cm3
  Dvalue = 8.82
  Group = -> [Cu_element003,Zn_element003,Pb_element006]
  conduct = 2
  density = 1
  expand = 3
  formula = G4_BRONZE
  name = G4_BRONZE
  specific = 4
FEATURE [App::DocumentObjectGroupPython] Fe_element008  label="Fe_element : 74"  # scripted group (container) (typed FeaturePython)
  n = 74
  ref = Fe_element
FEATURE [App::DocumentObjectGroupPython] Cr_element002  label="Cr_element : 18"  # scripted group (container) (typed FeaturePython)
  n = 18
  ref = Cr_element
FEATURE [App::DocumentObjectGroupPython] Ni_element002  label="Ni_element : 8"  # scripted group (container) (typed FeaturePython)
  n = 8
  ref = Ni_element
FEATURE [App::DocumentObjectGroupPython] G4_STAINLESS_STEEL  label="G4_STAINLESS-STEEL"  # scripted group (container) (typed FeaturePython)
  Dunit = g/cm3
  Dvalue = 8
  Group = -> [Fe_element008,Cr_element002,Ni_element002]
  conduct = 2
  density = 1
  expand = 3
  formula = G4_STAINLESS-STEEL
  name = G4_STAINLESS-STEEL
  specific = 4
FEATURE [App::DocumentObjectGroupPython] H_element116  label="H_element : 064"  # scripted group (container) (typed FeaturePython)
  n = 18
  ref = H_element
FEATURE [App::DocumentObjectGroupPython] C_element126  label="C_element : 071"  # scripted group (container) (typed FeaturePython)
  n = 12
  ref = C_element
FEATURE [App::DocumentObjectGroupPython] O_element109  label="O_element : 062"  # scripted group (container) (typed FeaturePython)
  n = 7
  ref = O_element
FEATURE [App::DocumentObjectGroupPython] G4_CR39  # scripted group (container) (typed FeaturePython)
  Dunit = g/cm3
  Dvalue = 1.32
  Group = -> [H_element116,C_element126,O_element109]
  conduct = 2
  density = 1
  expand = 3
  formula = G4_CR39
  name = G4_CR39
  specific = 4
FEATURE [App::DocumentObjectGroupPython] H_element117  label="H_element : 38"  # scripted group (container) (typed FeaturePython)
  n = 38
  ref = H_element
FEATURE [App::DocumentObjectGroupPython] C_element127  label="C_element : 072"  # scripted group (container) (typed FeaturePython)
  n = 18
  ref = C_element
FEATURE [App::DocumentObjectGroupPython] O_element110  label="O_element : 063"  # scripted group (container) (typed FeaturePython)
  n = 1
  ref = O_element
FEATURE [App::DocumentObjectGroupPython] G4_OCTADECANOL  # scripted group (container) (typed FeaturePython)
  Dunit = g/cm3
  Dvalue = 0.812
  Group = -> [H_element117,C_element127,O_element110]
  conduct = 2
  density = 1
  expand = 3
  formula = G4_OCTADECANOL
  name = G4_OCTADECANOL
  specific = 4
FEATURE [App::DocumentObjectGroupPython] HEP  # scripted group (container) (typed FeaturePython)
  Group = -> [G4_lH2,G4_lN2,G4_lO2,G4_lAr,G4_lBr,G4_lKr,G4_lXe,G4_PbWO4,G4_Galactic,G4_GRAPHITE_POROUS,G4_LUCITE,G4_BRASS,G4_BRONZE,G4_STAINLESS_STEEL,G4_CR39,G4_OCTADECANOL]
FEATURE [App::DocumentObjectGroupPython] C_element128  label="C_element : 073"  # scripted group (container) (typed FeaturePython)
  n = 14
  ref = C_element
FEATURE [App::DocumentObjectGroupPython] H_element118  label="H_element : 065"  # scripted group (container) (typed FeaturePython)
  n = 10
  ref = H_element
FEATURE [App::DocumentObjectGroupPython] O_element111  label="O_element : 064"  # scripted group (container) (typed FeaturePython)
  n = 2
  ref = O_element
FEATURE [App::DocumentObjectGroupPython] N_element050  label="N_element : 023"  # scripted group (container) (typed FeaturePython)
  n = 2
  ref = N_element
FEATURE [App::DocumentObjectGroupPython] G4_KEVLAR  # scripted group (container) (typed FeaturePython)
  Dunit = g/cm3
  Dvalue = 1.44
  Group = -> [C_element128,H_element118,O_element111,N_element050]
  conduct = 2
  density = 1
  expand = 3
  formula = G4_KEVLAR
  name = G4_KEVLAR
  specific = 4
FEATURE [App::DocumentObjectGroupPython] C_element129  label="C_element : 074"  # scripted group (container) (typed FeaturePython)
  n = 10
  ref = C_element
FEATURE [App::DocumentObjectGroupPython] H_element119  label="H_element : 066"  # scripted group (container) (typed FeaturePython)
  n = 8
  ref = H_element
FEATURE [App::DocumentObjectGroupPython] O_element112  label="O_element : 065"  # scripted group (container) (typed FeaturePython)
  n = 4
  ref = O_element
FEATURE [App::DocumentObjectGroupPython] G4_DACRON  # scripted group (container) (typed FeaturePython)
  Dunit = g/cm3
  Dvalue = 1.4
  Group = -> [C_element129,H_element119,O_element112]
  conduct = 2
  density = 1
  expand = 3
  formula = G4_DACRON
  name = G4_DACRON
  specific = 4
FEATURE [App::DocumentObjectGroupPython] C_element130  label="C_element : 075"  # scripted group (container) (typed FeaturePython)
  n = 4
  ref = C_element
FEATURE [App::DocumentObjectGroupPython] H_element120  label="H_element : 067"  # scripted group (container) (typed FeaturePython)
  n = 5
  ref = H_element
FEATURE [App::DocumentObjectGroupPython] Cl_element030  label="Cl_element : 016"  # scripted group (container) (typed FeaturePython)
  n = 1
  ref = Cl_element
FEATURE [App::DocumentObjectGroupPython] G4_NEOPRENE  # scripted group (container) (typed FeaturePython)
  Dunit = g/cm3
  Dvalue = 1.23
  Group = -> [C_element130,H_element120,Cl_element030]
  conduct = 2
  density = 1
  expand = 3
  formula = G4_NEOPRENE
  name = G4_NEOPRENE
  specific = 4
FEATURE [App::DocumentObjectGroupPython] Space  # scripted group (container) (typed FeaturePython)
  Group = -> [G4_KEVLAR,G4_DACRON,G4_NEOPRENE]
FEATURE [App::DocumentObjectGroupPython] H_element121  label="H_element : 068"  # scripted group (container) (typed FeaturePython)
  n = 5
  ref = H_element
FEATURE [App::DocumentObjectGroupPython] C_element131  label="C_element : 076"  # scripted group (container) (typed FeaturePython)
  n = 4
  ref = C_element
FEATURE [App::DocumentObjectGroupPython] N_element051  label="N_element : 3"  # scripted group (container) (typed FeaturePython)
  n = 3
  ref = N_element
FEATURE [App::DocumentObjectGroupPython] O_element113  label="O_element : 066"  # scripted group (container) (typed FeaturePython)
  n = 1
  ref = O_element
FEATURE [App::DocumentObjectGroupPython] G4_CYTOSINE  # scripted group (container) (typed FeaturePython)
  Dunit = g/cm3
  Dvalue = 1.55
  Group = -> [H_element121,C_element131,N_element051,O_element113]
  conduct = 2
  density = 1
  expand = 3
  formula = G4_CYTOSINE
  name = G4_CYTOSINE
  specific = 4
FEATURE [App::DocumentObjectGroupPython] H_element122  label="H_element : 069"  # scripted group (container) (typed FeaturePython)
  n = 6
  ref = H_element
FEATURE [App::DocumentObjectGroupPython] C_element132  label="C_element : 077"  # scripted group (container) (typed FeaturePython)
  n = 5
  ref = C_element
FEATURE [App::DocumentObjectGroupPython] N_element052  label="N_element : 024"  # scripted group (container) (typed FeaturePython)
  n = 2
  ref = N_element
FEATURE [App::DocumentObjectGroupPython] O_element114  label="O_element : 067"  # scripted group (container) (typed FeaturePython)
  n = 2
  ref = O_element
FEATURE [App::DocumentObjectGroupPython] G4_THYMINE  # scripted group (container) (typed FeaturePython)
  Dunit = g/cm3
  Dvalue = 1.23
  Group = -> [H_element122,C_element132,N_element052,O_element114]
  conduct = 2
  density = 1
  expand = 3
  formula = G4_THYMINE
  name = G4_THYMINE
  specific = 4
FEATURE [App::DocumentObjectGroupPython] H_element123  label="H_element : 070"  # scripted group (container) (typed FeaturePython)
  n = 4
  ref = H_element
FEATURE [App::DocumentObjectGroupPython] C_element133  label="C_element : 078"  # scripted group (container) (typed FeaturePython)
  n = 4
  ref = C_element
FEATURE [App::DocumentObjectGroupPython] N_element053  label="N_element : 025"  # scripted group (container) (typed FeaturePython)
  n = 2
  ref = N_element
FEATURE [App::DocumentObjectGroupPython] O_element115  label="O_element : 068"  # scripted group (container) (typed FeaturePython)
  n = 2
  ref = O_element
FEATURE [App::DocumentObjectGroupPython] G4_URACIL  # scripted group (container) (typed FeaturePython)
  Dunit = g/cm3
  Dvalue = 1.32
  Group = -> [H_element123,C_element133,N_element053,O_element115]
  conduct = 2
  density = 1
  expand = 3
  formula = G4_URACIL
  name = G4_URACIL
  specific = 4
FEATURE [App::DocumentObjectGroupPython] H_element124  label="H_element : 071"  # scripted group (container) (typed FeaturePython)
  n = 4
  ref = H_element
FEATURE [App::DocumentObjectGroupPython] C_element134  label="C_element : 079"  # scripted group (container) (typed FeaturePython)
  n = 5
  ref = C_element
FEATURE [App::DocumentObjectGroupPython] N_element054  label="N_element : 026"  # scripted group (container) (typed FeaturePython)
  n = 5
  ref = N_element
FEATURE [App::DocumentObjectGroupPython] G4_DNA_ADENINE  # scripted group (container) (typed FeaturePython)
  Dunit = g/cm3
  Dvalue = 1
  Group = -> [H_element124,C_element134,N_element054]
  conduct = 2
  density = 1
  expand = 3
  formula = G4_DNA_ADENINE
  name = G4_DNA_ADENINE
  specific = 4
FEATURE [App::DocumentObjectGroupPython] H_element125  label="H_element : 072"  # scripted group (container) (typed FeaturePython)
  n = 4
  ref = H_element
FEATURE [App::DocumentObjectGroupPython] C_element135  label="C_element : 080"  # scripted group (container) (typed FeaturePython)
  n = 5
  ref = C_element
FEATURE [App::DocumentObjectGroupPython] N_element055  label="N_element : 027"  # scripted group (container) (typed FeaturePython)
  n = 5
  ref = N_element
FEATURE [App::DocumentObjectGroupPython] O_element116  label="O_element : 069"  # scripted group (container) (typed FeaturePython)
  n = 1
  ref = O_element
FEATURE [App::DocumentObjectGroupPython] G4_DNA_GUANINE  # scripted group (container) (typed FeaturePython)
  Dunit = g/cm3
  Dvalue = 1
  Group = -> [H_element125,C_element135,N_element055,O_element116]
  conduct = 2
  density = 1
  expand = 3
  formula = G4_DNA_GUANINE
  name = G4_DNA_GUANINE
  specific = 4
FEATURE [App::DocumentObjectGroupPython] H_element126  label="H_element : 073"  # scripted group (container) (typed FeaturePython)
  n = 4
  ref = H_element
FEATURE [App::DocumentObjectGroupPython] C_element136  label="C_element : 081"  # scripted group (container) (typed FeaturePython)
  n = 4
  ref = C_element
FEATURE [App::DocumentObjectGroupPython] N_element056  label="N_element : 028"  # scripted group (container) (typed FeaturePython)
  n = 3
  ref = N_element
FEATURE [App::DocumentObjectGroupPython] O_element117  label="O_element : 070"  # scripted group (container) (typed FeaturePython)
  n = 1
  ref = O_element
FEATURE [App::DocumentObjectGroupPython] G4_DNA_CYTOSINE  # scripted group (container) (typed FeaturePython)
  Dunit = g/cm3
  Dvalue = 1
  Group = -> [H_element126,C_element136,N_element056,O_element117]
  conduct = 2
  density = 1
  expand = 3
  formula = G4_DNA_CYTOSINE
  name = G4_DNA_CYTOSINE
  specific = 4
FEATURE [App::DocumentObjectGroupPython] H_element127  label="H_element : 074"  # scripted group (container) (typed FeaturePython)
  n = 5
  ref = H_element
FEATURE [App::DocumentObjectGroupPython] C_element137  label="C_element : 082"  # scripted group (container) (typed FeaturePython)
  n = 5
  ref = C_element
FEATURE [App::DocumentObjectGroupPython] N_element057  label="N_element : 029"  # scripted group (container) (typed FeaturePython)
  n = 2
  ref = N_element
FEATURE [App::DocumentObjectGroupPython] O_element118  label="O_element : 071"  # scripted group (container) (typed FeaturePython)
  n = 2
  ref = O_element
FEATURE [App::DocumentObjectGroupPython] G4_DNA_THYMINE  # scripted group (container) (typed FeaturePython)
  Dunit = g/cm3
  Dvalue = 1
  Group = -> [H_element127,C_element137,N_element057,O_element118]
  conduct = 2
  density = 1
  expand = 3
  formula = G4_DNA_THYMINE
  name = G4_DNA_THYMINE
  specific = 4
FEATURE [App::DocumentObjectGroupPython] H_element128  label="H_element : 075"  # scripted group (container) (typed FeaturePython)
  n = 3
  ref = H_element
FEATURE [App::DocumentObjectGroupPython] C_element138  label="C_element : 083"  # scripted group (container) (typed FeaturePython)
  n = 4
  ref = C_element
FEATURE [App::DocumentObjectGroupPython] N_element058  label="N_element : 030"  # scripted group (container) (typed FeaturePython)
  n = 2
  ref = N_element
FEATURE [App::DocumentObjectGroupPython] O_element119  label="O_element : 072"  # scripted group (container) (typed FeaturePython)
  n = 2
  ref = O_element
FEATURE [App::DocumentObjectGroupPython] G4_DNA_URACIL  # scripted group (container) (typed FeaturePython)
  Dunit = g/cm3
  Dvalue = 1
  Group = -> [H_element128,C_element138,N_element058,O_element119]
  conduct = 2
  density = 1
  expand = 3
  formula = G4_DNA_URACIL
  name = G4_DNA_URACIL
  specific = 4
FEATURE [App::DocumentObjectGroupPython] H_element129  label="H_element : 076"  # scripted group (container) (typed FeaturePython)
  n = 10
  ref = H_element
FEATURE [App::DocumentObjectGroupPython] C_element139  label="C_element : 084"  # scripted group (container) (typed FeaturePython)
  n = 10
  ref = C_element
FEATURE [App::DocumentObjectGroupPython] N_element059  label="N_element : 031"  # scripted group (container) (typed FeaturePython)
  n = 5
  ref = N_element
FEATURE [App::DocumentObjectGroupPython] O_element120  label="O_element : 073"  # scripted group (container) (typed FeaturePython)
  n = 4
  ref = O_element
FEATURE [App::DocumentObjectGroupPython] G4_DNA_ADENOSINE  # scripted group (container) (typed FeaturePython)
  Dunit = g/cm3
  Dvalue = 1
  Group = -> [H_element129,C_element139,N_element059,O_element120]
  conduct = 2
  density = 1
  expand = 3
  formula = G4_DNA_ADENOSINE
  name = G4_DNA_ADENOSINE
  specific = 4
FEATURE [App::DocumentObjectGroupPython] H_element130  label="H_element : 077"  # scripted group (container) (typed FeaturePython)
  n = 10
  ref = H_element
FEATURE [App::DocumentObjectGroupPython] C_element140  label="C_element : 085"  # scripted group (container) (typed FeaturePython)
  n = 10
  ref = C_element
FEATURE [App::DocumentObjectGroupPython] N_element060  label="N_element : 032"  # scripted group (container) (typed FeaturePython)
  n = 5
  ref = N_element
FEATURE [App::DocumentObjectGroupPython] O_element121  label="O_element : 074"  # scripted group (container) (typed FeaturePython)
  n = 5
  ref = O_element
FEATURE [App::DocumentObjectGroupPython] G4_DNA_GUANOSINE  # scripted group (container) (typed FeaturePython)
  Dunit = g/cm3
  Dvalue = 1
  Group = -> [H_element130,C_element140,N_element060,O_element121]
  conduct = 2
  density = 1
  expand = 3
  formula = G4_DNA_GUANOSINE
  name = G4_DNA_GUANOSINE
  specific = 4
FEATURE [App::DocumentObjectGroupPython] H_element131  label="H_element : 078"  # scripted group (container) (typed FeaturePython)
  n = 10
  ref = H_element
FEATURE [App::DocumentObjectGroupPython] C_element141  label="C_element : 086"  # scripted group (container) (typed FeaturePython)
  n = 9
  ref = C_element
FEATURE [App::DocumentObjectGroupPython] N_element061  label="N_element : 033"  # scripted group (container) (typed FeaturePython)
  n = 3
  ref = N_element
FEATURE [App::DocumentObjectGroupPython] O_element122  label="O_element : 075"  # scripted group (container) (typed FeaturePython)
  n = 5
  ref = O_element
FEATURE [App::DocumentObjectGroupPython] G4_DNA_CYTIDINE  # scripted group (container) (typed FeaturePython)
  Dunit = g/cm3
  Dvalue = 1
  Group = -> [H_element131,C_element141,N_element061,O_element122]
  conduct = 2
  density = 1
  expand = 3
  formula = G4_DNA_CYTIDINE
  name = G4_DNA_CYTIDINE
  specific = 4
FEATURE [App::DocumentObjectGroupPython] H_element132  label="H_element : 079"  # scripted group (container) (typed FeaturePython)
  n = 9
  ref = H_element
FEATURE [App::DocumentObjectGroupPython] C_element142  label="C_element : 087"  # scripted group (container) (typed FeaturePython)
  n = 9
  ref = C_element
FEATURE [App::DocumentObjectGroupPython] N_element062  label="N_element : 034"  # scripted group (container) (typed FeaturePython)
  n = 2
  ref = N_element
FEATURE [App::DocumentObjectGroupPython] O_element123  label="O_element : 076"  # scripted group (container) (typed FeaturePython)
  n = 6
  ref = O_element
FEATURE [App::DocumentObjectGroupPython] G4_DNA_URIDINE  # scripted group (container) (typed FeaturePython)
  Dunit = g/cm3
  Dvalue = 1
  Group = -> [H_element132,C_element142,N_element062,O_element123]
  conduct = 2
  density = 1
  expand = 3
  formula = G4_DNA_URIDINE
  name = G4_DNA_URIDINE
  specific = 4
FEATURE [App::DocumentObjectGroupPython] H_element133  label="H_element : 080"  # scripted group (container) (typed FeaturePython)
  n = 11
  ref = H_element
FEATURE [App::DocumentObjectGroupPython] C_element143  label="C_element : 088"  # scripted group (container) (typed FeaturePython)
  n = 10
  ref = C_element
FEATURE [App::DocumentObjectGroupPython] N_element063  label="N_element : 035"  # scripted group (container) (typed FeaturePython)
  n = 2
  ref = N_element
FEATURE [App::DocumentObjectGroupPython] O_element124  label="O_element : 077"  # scripted group (container) (typed FeaturePython)
  n = 6
  ref = O_element
FEATURE [App::DocumentObjectGroupPython] G4_DNA_METHYLURIDINE  # scripted group (container) (typed FeaturePython)
  Dunit = g/cm3
  Dvalue = 1
  Group = -> [H_element133,C_element143,N_element063,O_element124]
  conduct = 2
  density = 1
  expand = 3
  formula = G4_DNA_METHYLURIDINE
  name = G4_DNA_METHYLURIDINE
  specific = 4
FEATURE [App::DocumentObjectGroupPython] P_element014  label="P_element : 003"  # scripted group (container) (typed FeaturePython)
  n = 1
  ref = P_element
FEATURE [App::DocumentObjectGroupPython] O_element125  label="O_element : 078"  # scripted group (container) (typed FeaturePython)
  n = 3
  ref = O_element
FEATURE [App::DocumentObjectGroupPython] G4_DNA_MONOPHOSPHATE  # scripted group (container) (typed FeaturePython)
  Dunit = g/cm3
  Dvalue = 1
  Group = -> [P_element014,O_element125]
  conduct = 2
  density = 1
  expand = 3
  formula = G4_DNA_MONOPHOSPHATE
  name = G4_DNA_MONOPHOSPHATE
  specific = 4
FEATURE [App::DocumentObjectGroupPython] H_element134  label="H_element : 081"  # scripted group (container) (typed FeaturePython)
  n = 10
  ref = H_element
FEATURE [App::DocumentObjectGroupPython] C_element144  label="C_element : 089"  # scripted group (container) (typed FeaturePython)
  n = 10
  ref = C_element
FEATURE [App::DocumentObjectGroupPython] N_element064  label="N_element : 036"  # scripted group (container) (typed FeaturePython)
  n = 5
  ref = N_element
FEATURE [App::DocumentObjectGroupPython] O_element126  label="O_element : 079"  # scripted group (container) (typed FeaturePython)
  n = 7
  ref = O_element
FEATURE [App::DocumentObjectGroupPython] P_element015  label="P_element : 004"  # scripted group (container) (typed FeaturePython)
  n = 1
  ref = P_element
FEATURE [App::DocumentObjectGroupPython] G4_DNA_A  # scripted group (container) (typed FeaturePython)
  Dunit = g/cm3
  Dvalue = 1
  Group = -> [H_element134,C_element144,N_element064,O_element126,P_element015]
  conduct = 2
  density = 1
  expand = 3
  formula = G4_DNA_A
  name = G4_DNA_A
  specific = 4
FEATURE [App::DocumentObjectGroupPython] H_element135  label="H_element : 082"  # scripted group (container) (typed FeaturePython)
  n = 10
  ref = H_element
FEATURE [App::DocumentObjectGroupPython] C_element145  label="C_element : 090"  # scripted group (container) (typed FeaturePython)
  n = 10
  ref = C_element
FEATURE [App::DocumentObjectGroupPython] N_element065  label="N_element : 037"  # scripted group (container) (typed FeaturePython)
  n = 5
  ref = N_element
FEATURE [App::DocumentObjectGroupPython] O_element127  label="O_element : 8"  # scripted group (container) (typed FeaturePython)
  n = 8
  ref = O_element
FEATURE [App::DocumentObjectGroupPython] P_element016  label="P_element : 005"  # scripted group (container) (typed FeaturePython)
  n = 1
  ref = P_element
FEATURE [App::DocumentObjectGroupPython] G4_DNA_G  # scripted group (container) (typed FeaturePython)
  Dunit = g/cm3
  Dvalue = 1
  Group = -> [H_element135,C_element145,N_element065,O_element127,P_element016]
  conduct = 2
  density = 1
  expand = 3
  formula = G4_DNA_G
  name = G4_DNA_G
  specific = 4
FEATURE [App::DocumentObjectGroupPython] H_element136  label="H_element : 083"  # scripted group (container) (typed FeaturePython)
  n = 10
  ref = H_element
FEATURE [App::DocumentObjectGroupPython] C_element146  label="C_element : 091"  # scripted group (container) (typed FeaturePython)
  n = 9
  ref = C_element
FEATURE [App::DocumentObjectGroupPython] N_element066  label="N_element : 038"  # scripted group (container) (typed FeaturePython)
  n = 3
  ref = N_element
FEATURE [App::DocumentObjectGroupPython] O_element128  label="O_element : 080"  # scripted group (container) (typed FeaturePython)
  n = 8
  ref = O_element
FEATURE [App::DocumentObjectGroupPython] P_element017  label="P_element : 006"  # scripted group (container) (typed FeaturePython)
  n = 1
  ref = P_element
FEATURE [App::DocumentObjectGroupPython] G4_DNA_C  # scripted group (container) (typed FeaturePython)
  Dunit = g/cm3
  Dvalue = 1
  Group = -> [H_element136,C_element146,N_element066,O_element128,P_element017]
  conduct = 2
  density = 1
  expand = 3
  formula = G4_DNA_C
  name = G4_DNA_C
  specific = 4
FEATURE [App::DocumentObjectGroupPython] H_element137  label="H_element : 084"  # scripted group (container) (typed FeaturePython)
  n = 9
  ref = H_element
FEATURE [App::DocumentObjectGroupPython] C_element147  label="C_element : 092"  # scripted group (container) (typed FeaturePython)
  n = 9
  ref = C_element
FEATURE [App::DocumentObjectGroupPython] N_element067  label="N_element : 039"  # scripted group (container) (typed FeaturePython)
  n = 2
  ref = N_element
FEATURE [App::DocumentObjectGroupPython] O_element129  label="O_element : 9"  # scripted group (container) (typed FeaturePython)
  n = 9
  ref = O_element
FEATURE [App::DocumentObjectGroupPython] P_element018  label="P_element : 007"  # scripted group (container) (typed FeaturePython)
  n = 1
  ref = P_element
FEATURE [App::DocumentObjectGroupPython] G4_DNA_U  # scripted group (container) (typed FeaturePython)
  Dunit = g/cm3
  Dvalue = 1
  Group = -> [H_element137,C_element147,N_element067,O_element129,P_element018]
  conduct = 2
  density = 1
  expand = 3
  formula = G4_DNA_U
  name = G4_DNA_U
  specific = 4
FEATURE [App::DocumentObjectGroupPython] H_element138  label="H_element : 085"  # scripted group (container) (typed FeaturePython)
  n = 11
  ref = H_element
FEATURE [App::DocumentObjectGroupPython] C_element148  label="C_element : 093"  # scripted group (container) (typed FeaturePython)
  n = 10
  ref = C_element
FEATURE [App::DocumentObjectGroupPython] N_element068  label="N_element : 040"  # scripted group (container) (typed FeaturePython)
  n = 2
  ref = N_element
FEATURE [App::DocumentObjectGroupPython] O_element130  label="O_element : 081"  # scripted group (container) (typed FeaturePython)
  n = 9
  ref = O_element
FEATURE [App::DocumentObjectGroupPython] P_element019  label="P_element : 008"  # scripted group (container) (typed FeaturePython)
  n = 1
  ref = P_element
FEATURE [App::DocumentObjectGroupPython] G4_DNA_MU  # scripted group (container) (typed FeaturePython)
  Dunit = g/cm3
  Dvalue = 1
  Group = -> [H_element138,C_element148,N_element068,O_element130,P_element019]
  conduct = 2
  density = 1
  expand = 3
  formula = G4_DNA_MU
  name = G4_DNA_MU
  specific = 4
FEATURE [App::DocumentObjectGroupPython] BioChemical  # scripted group (container) (typed FeaturePython)
  Group = -> [G4_CYTOSINE,G4_THYMINE,G4_URACIL,G4_DNA_ADENINE,G4_DNA_GUANINE,G4_DNA_CYTOSINE,G4_DNA_THYMINE,G4_DNA_URACIL,G4_DNA_ADENOSINE,G4_DNA_GUANOSINE,G4_DNA_CYTIDINE,G4_DNA_URIDINE,G4_DNA_METHYLURIDINE,G4_DNA_MONOPHOSPHATE,G4_DNA_A,G4_DNA_G,G4_DNA_C,G4_DNA_U,G4_DNA_MU]
FEATURE [App::DocumentObjectGroupPython] G4Materials  # scripted group (container) (typed FeaturePython)
  Group = -> [NIST,Element,HEP,Space,BioChemical]
  version = 1
FEATURE [App::DocumentObjectGroupPython] Geant4  # scripted group (container) (typed FeaturePython)
  Group = -> [G4Isotopes,G4Elements,G4Materials]
FEATURE [App::DocumentObjectGroupPython] Materials  # scripted group (container) (typed FeaturePython)
  Group = -> [Geant4]
FEATURE [Part::FeaturePython] GDMLBox_WorldBox  # WARN: FeaturePython — macro-defined, semantics opaque (R4)
  lunit = 2
  material = 5
  x = 374.4
  y = 354.9
  z = 169
FEATURE [Part::FeaturePython] GDMLTube  # WARN: FeaturePython — macro-defined, semantics opaque (R4)
  Placement = pos=(17,-4,0) rot=(0,0,1;0rad)
  aunit = 1
  deltaphi = 90
  lunit = 2
  material = 0
  rmax = 7
  rmin = 5
  startphi = 0
  z = 7
FEATURE [App::Part] LV_Tube
  Group = -> [GDMLTube]
  Origin = -> Origin003
  SkinSurface = 0
FEATURE [Part::FeaturePython] GDMLSphere  # WARN: FeaturePython — macro-defined, semantics opaque (R4)
  aunit = 1
  deltaphi = 360
  deltatheta = 180
  lunit = 2
  material = 0
  rmax = 2
  rmin = 0
  startphi = 0
  starttheta = 0
FEATURE [App::Part] LV_Sphere
  Group = -> [GDMLSphere]
  Origin = -> Origin004
  Placement = pos=(15,-5,0) rot=(0,0,1;0rad)
  SkinSurface = 0
FEATURE [App::Part] LV_Box  label="Assembly"
  Group = -> [LV_Tube,LV_Sphere]
  Origin = -> Origin002
  Placement = pos=(20,0,0) rot=(0,0,1;0rad)
FEATURE [Part::FeaturePython] Array001  # Draft array (typed FeaturePython)
  AlwaysSyncPlacement = false
  Angle = 360
  ArrayType = 0
  Axis = (0,0,1)
  Base = -> LV_Box
  Center = (0,0,0)
  Count = 4
  ExpandArray = false
  Fuse = true
  IntervalAxis = (0,0,0)
  IntervalX = (30,0,0)
  IntervalY = (0,30,0)
  IntervalZ = (0,0,100)
  NumberCircles = 3
  NumberPolar = 5
  NumberX = 2
  NumberY = 2
  NumberZ = 1
  Placement = pos=(40,0,0) rot=(0,0,1;0rad)
  PlacementList = 4 placements: [(20,0,0),(20,30,0),(50,0,0),(50,30,0)]
  RadialDistance = 50
  ScaleList = (4) [(1,1,1),(1,1,1),(1,1,1),(1,1,1)]
  Symmetry = 1
  TangentialDistance = 25
FEATURE [App::Part] Part001
  Group = -> [LV_Box,Array001]
  Origin = -> Origin005
FEATURE [Part::FeaturePython] Array  # Draft array (typed FeaturePython)
  Angle = 360
  ArrayType = 1
  Axis = (0,0,1)
  Base = -> Part001
  Center = (0,0,0)
  Count = 6
  Fuse = false
  IntervalAxis = (0,0,0)
  IntervalX = (50,0,0)
  IntervalY = (0,50,0)
  IntervalZ = (0,0,50)
  NumberCircles = 3
  NumberPolar = 6
  NumberX = 2
  NumberY = 2
  NumberZ = 1
  RadialDistance = 50
  Symmetry = 1
  TangentialDistance = 25
FEATURE [App::Part] Part  label="experiment"
  Group = -> [Array,Part001]
  Origin = -> Origin001
FEATURE [App::Part] worldVOL
  Group = -> [GDMLBox_WorldBox,Part]
  Origin = -> Origin
